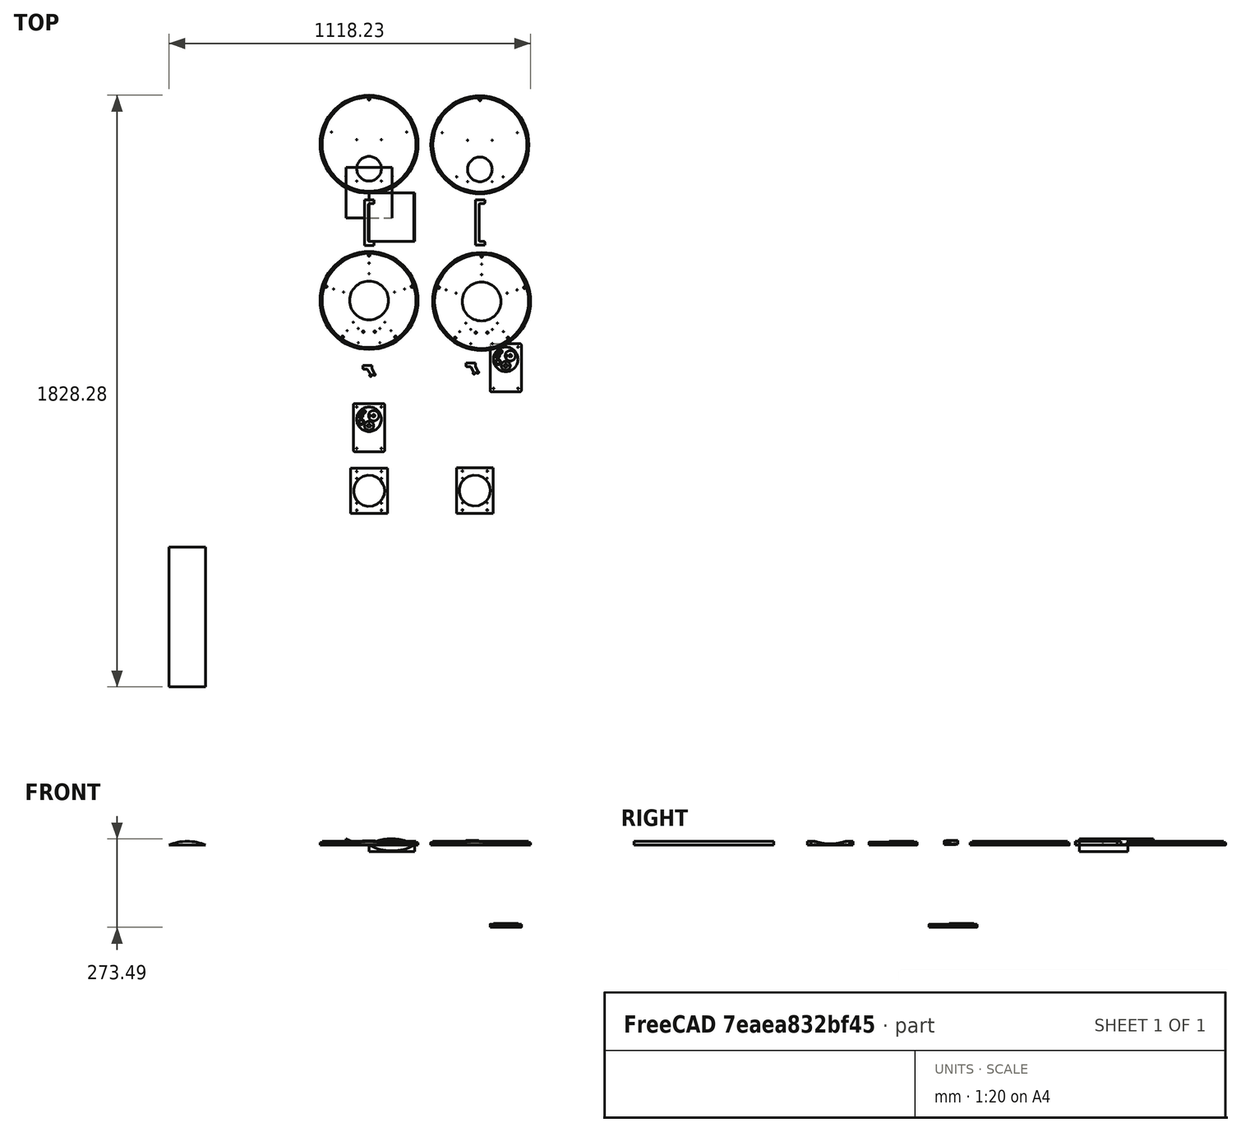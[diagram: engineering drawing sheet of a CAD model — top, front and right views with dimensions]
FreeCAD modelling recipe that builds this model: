
FCSTD DOCUMENT  (FreeCAD 0.19R24291 (Git))
Label: AnywhereAmps_Alpha_A4APR
License: All rights reserved
LicenseURL: http://en.wikipedia.org/wiki/All_rights_reserved
objects: Sketcher::SketchObject×48, Part::Part2DObjectPython×20, PartDesign::Body×18, TechDraw::DrawViewDimension×14, PartDesign::Pad×13, App::Part×8, PartDesign::Pocket×7, Part::FeaturePython×7, TechDraw::DrawProjGroupItem×4, Part::Feature×4, TechDraw::DrawSVGTemplate×2, TechDraw::DrawPage×2, Part::Mirroring×2, PartDesign::FeatureBase×2, Spreadsheet::Sheet×1, TechDraw::DrawViewPart×1, TechDraw::DrawProjGroup×1, TechDraw::DrawViewAnnotation×1, App::LinkGroup×1
note: 141 computed .brp shape members not serialized (recipe doc carries the construction recipe); baked Part::Feature solids carry a one-line shape summary decoded from their .brp
EXTERNAL_REF file=../../../../Zerspanobert/Projekte/Spoilboard/wasteplate_BL_0607.FCStd obj=Spreadsheet

FEATURE [TechDraw::DrawSVGTemplate] Template
  EditableTexts = Designed_by_Name=Designed by Name; Drawing_number=Drawing number; FC-Date=Date; FC-SC=Scale; FC-SH=Sheet; FC-Title=Title; Subtitle=Subtitle; Weight=Weight
  Height = 210
  Orientation = 1
  Width = 297
FEATURE [Sketcher::SketchObject] Sketch  label="master_top_xy"
  FullyConstrained = true
  MapMode = 5
  Support = -> [XY_Plane001]
  expr: Constraints[60] = <<Dimensions>>.predrill_3_rad
  expr: Constraints[37] = <<Dimensions>>.predrill_3_rad
  expr: Constraints[35] = <<Dimensions>>.fastener_dist
  expr: Constraints[50] = <<Dimensions>>.ampcarrier_wid - 2 * <<Dimensions>>.ampcarrier_pre_dist
  expr: Constraints[36] = <<Dimensions>>.fastener_dist
  expr: Constraints[34] = <<Dimensions>>.fastener_dist
  expr: Constraints[49] = <<Dimensions>>.ampcarrier_len - 2 * <<Dimensions>>.ampcarrier_pre_dist
  expr: Constraints[33] = <<Dimensions>>.fastener_dist
  expr: Constraints[55] = <<Dimensions>>.emboss_vdist - <<Dimensions>>.ampcarrier_pre_dist
  expr: Constraints[5] = <<Dimensions>>.shell_thick
  expr: Constraints[11] = <<Dimensions>>.ctrlcutout_rad
  expr: Constraints[64] = <<Dimensions>>.duvel_dist
  expr: Constraints[65] = <<Dimensions>>.duvel_6_rad
  expr: Constraints[1] = Spreadsheet.shell_outer_rad
  expr: Constraints[12] = <<Dimensions>>.ctrlcutout_vdist
  sketch-geometry (24):
    g0: Circle CenterX=0 CenterY=0 CenterZ=0 NormalX=0 NormalY=0 NormalZ=1 AngleXU=0 Radius=151.5
    g1: Circle CenterX=0 CenterY=0 CenterZ=0 NormalX=0 NormalY=0 NormalZ=1 AngleXU=0 Radius=145.3
    g2: LineSegment StartX=-151.5 StartY=0 StartZ=0 EndX=-145.3 EndY=0 EndZ=0
    g3: Circle CenterX=0 CenterY=-75.75 CenterZ=0 NormalX=0 NormalY=0 NormalZ=1 AngleXU=0 Radius=38
    g4: LineSegment StartX=0 StartY=0 StartZ=0 EndX=0 EndY=-75.75 EndZ=0
    g5: LineSegment StartX=0 StartY=0 StartZ=0 EndX=-138.189 EndY=44.9002 EndZ=0
    g6: LineSegment StartX=0 StartY=0 StartZ=0 EndX=0 EndY=145.3 EndZ=0
    g7: LineSegment StartX=0 StartY=0 StartZ=0 EndX=138.189 EndY=44.9002 EndZ=0
    g8: LineSegment StartX=0 StartY=0 StartZ=0 EndX=85.4052 EndY=-117.55 EndZ=0
    g9: LineSegment StartX=0 StartY=0 StartZ=0 EndX=-85.4052 EndY=-117.55 EndZ=0
    g10: Circle CenterX=0 CenterY=139.3 CenterZ=0 NormalX=0 NormalY=0 NormalZ=1 AngleXU=0 Radius=3
    g11: Circle CenterX=116.219 CenterY=37.7619 CenterZ=0 NormalX=0 NormalY=0 NormalZ=1 AngleXU=0 Radius=1
    g12: Circle CenterX=71.8274 CenterY=-98.8619 CenterZ=0 NormalX=0 NormalY=0 NormalZ=1 AngleXU=0 Radius=1
    g13: Circle CenterX=-71.8274 CenterY=-98.8619 CenterZ=0 NormalX=0 NormalY=0 NormalZ=1 AngleXU=0 Radius=1
    g14: Circle CenterX=-116.219 CenterY=37.7619 CenterZ=0 NormalX=0 NormalY=0 NormalZ=1 AngleXU=0 Radius=1
    g15: LineSegment StartX=38 StartY=14.25 StartZ=0 EndX=-38 EndY=14.25 EndZ=0
    g16: LineSegment StartX=-38 StartY=14.25 StartZ=0 EndX=-38 EndY=-113.75 EndZ=0
    g17: LineSegment StartX=-38 StartY=-113.75 StartZ=0 EndX=38 EndY=-113.75 EndZ=0
    g18: LineSegment StartX=38 StartY=-113.75 StartZ=0 EndX=38 EndY=14.25 EndZ=0
    g19: LineSegment StartX=0 StartY=14.25 StartZ=0 EndX=0 EndY=-113.75 EndZ=0
    g20: Circle CenterX=38 CenterY=-113.75 CenterZ=0 NormalX=0 NormalY=0 NormalZ=1 AngleXU=0 Radius=1
    g21: Circle CenterX=-38 CenterY=-113.75 CenterZ=0 NormalX=0 NormalY=0 NormalZ=1 AngleXU=0 Radius=1
    g22: Circle CenterX=-38 CenterY=14.25 CenterZ=0 NormalX=0 NormalY=0 NormalZ=1 AngleXU=0 Radius=1
    g23: Circle CenterX=38 CenterY=14.25 CenterZ=0 NormalX=0 NormalY=0 NormalZ=1 AngleXU=0 Radius=1
  constraints (66):
    c: Coincident(g0,g-1)
    c: Radius(g0) = 151.5
    c: Coincident(g1,g0)
    c: PointOnObject(g2,g0)
    c: PointOnObject(g2,g1)
    c: Distance(g2,g2) = 6.2
    c: PointOnObject(g2,g-1)
    c: Perpendicular(g0,g2)
    c: Coincident(g4,g0)
    c: Vertical(g4)
    c: Coincident(g3,g4)
    c: Radius(g3) = 38
    c: DistanceY(g3,g0) = 75.75
    c: Coincident(g5,g0)
    c: PointOnObject(g5,g1)
    c: Coincident(g6,g0)
    c: PointOnObject(g6,g1)
    c: Coincident(g7,g0)
    c: PointOnObject(g7,g1)
    c: Coincident(g8,g0)
    c: PointOnObject(g8,g1)
    c: Angle(g6,g5) = 1.25664
    c: Angle(g7,g6) = 1.25664
    c: Angle(g8,g7) = 1.25664
    c: PointOnObject(g6,g-2)
    c: Coincident(g9,g0)
    c: PointOnObject(g9,g1)
    c: Angle(g9,g8) = 1.25664
    c: PointOnObject(g10,g6)
    c: PointOnObject(g11,g7)
    c: PointOnObject(g12,g8)
    c: PointOnObject(g13,g9)
    c: PointOnObject(g14,g5)
    c: Distance(g14,g5) = 23.1
    c: Distance(g11,g7) = 23.1
    c: Distance(g12,g8) = 23.1
    c: Distance(g13,g9) = 23.1
    c: Radius(g14) = 1
    c: Equal(g14,g11)
    c: Equal(g14,g12)
    c: Equal(g14,g13)
    c: Coincident(g15,g16)
    c: Coincident(g16,g17)
    c: Coincident(g17,g18)
    c: Coincident(g18,g15)
    c: Horizontal(g15)
    c: Horizontal(g17)
    c: Vertical(g16)
    c: Vertical(g18)
    c: DistanceY(g16,g15) = 128
    c: DistanceX(g15,g15) = 76
    c: PointOnObject(g19,g17)
    c: Vertical(g19)
    c: Symmetric(g15,g15,g19)
    c: PointOnObject(g3,g19)
    c: DistanceY(g19,g3) = 38
    c: Coincident(g20,g17)
    c: Coincident(g21,g16)
    c: Coincident(g22,g15)
    c: Coincident(g23,g15)
    c: Radius(g23) = 1
    c: Equal(g23,g22)
    c: Equal(g23,g21)
    c: Equal(g23,g20)
    c: Distance(g10,g6) = 6
    c: Radius(g10) = 3
FEATURE [Sketcher::SketchObject] Sketch001  label="master_top_xz"
  ExternalGeometry = -> [Sketch]
  FullyConstrained = true
  MapMode = 5
  Placement = pos=(0,0,0) rot=(1,0,0;1.5708rad)
  Support = -> [XZ_Plane001]
  expr: Constraints[32] = <<Dimensions>>.bevel_thick
  expr: Constraints[21] = <<Dimensions>>.bevel_thick
  expr: Constraints[22] = <<Dimensions>>.base_thick
  expr: Constraints[17] = Spreadsheet.shell_outer_rad * 2
  expr: Constraints[19] = <<Dimensions>>.shell_thick
  expr: Constraints[20] = <<Dimensions>>.shell_thick
  sketch-geometry (32):
    g0: LineSegment StartX=-151.5 StartY=0 StartZ=0 EndX=151.5 EndY=0 EndZ=0
    g1: LineSegment StartX=151.5 StartY=0 StartZ=0 EndX=151.5 EndY=8 EndZ=0
    g2: LineSegment StartX=151.5 StartY=8 StartZ=0 EndX=-151.5 EndY=8 EndZ=0
    g3: LineSegment StartX=-151.5 StartY=8 StartZ=0 EndX=-151.5 EndY=0 EndZ=0
    g4: LineSegment StartX=-145.3 StartY=8 StartZ=0 EndX=145.3 EndY=8 EndZ=0
    g5: LineSegment StartX=145.3 StartY=8 StartZ=0 EndX=145.3 EndY=11.8 EndZ=0
    g6: LineSegment StartX=145.3 StartY=11.8 StartZ=0 EndX=-145.3 EndY=11.8 EndZ=0
    g7: LineSegment StartX=-145.3 StartY=11.8 StartZ=0 EndX=-145.3 EndY=8 EndZ=0
    g8: LineSegment StartX=-38 StartY=0 StartZ=0 EndX=-38 EndY=11.8 EndZ=0
    g9: LineSegment StartX=38 StartY=1.69e-14 StartZ=0 EndX=38 EndY=11.8 EndZ=0
    g10: LineSegment StartX=-151.5 StartY=3.8 StartZ=0 EndX=151.5 EndY=3.8 EndZ=0
    g11: LineSegment StartX=-3 StartY=3.8 StartZ=0 EndX=-3 EndY=11.8 EndZ=0
    g12: LineSegment StartX=3 StartY=3.8 StartZ=0 EndX=3 EndY=11.8 EndZ=0
    g13: LineSegment StartX=3 StartY=3.8 StartZ=0 EndX=-3 EndY=3.8 EndZ=0
    g14: LineSegment StartX=-39 StartY=11.8 StartZ=0 EndX=-39 EndY=3.8 EndZ=0
    g15: LineSegment StartX=-39 StartY=3.8 StartZ=0 EndX=-37 EndY=3.8 EndZ=0
    g16: LineSegment StartX=-37 StartY=3.8 StartZ=0 EndX=-37 EndY=11.8 EndZ=0
    g17: LineSegment StartX=37 StartY=11.8 StartZ=0 EndX=37 EndY=3.8 EndZ=0
    g18: LineSegment StartX=37 StartY=3.8 StartZ=0 EndX=39 EndY=3.8 EndZ=0
    g19: LineSegment StartX=39 StartY=3.8 StartZ=0 EndX=39 EndY=11.8 EndZ=0
    g20: LineSegment StartX=-117.219 StartY=11.8 StartZ=0 EndX=-117.219 EndY=3.8 EndZ=0
    g21: LineSegment StartX=-117.219 StartY=3.8 StartZ=0 EndX=-115.219 EndY=3.8 EndZ=0
    g22: LineSegment StartX=-115.219 StartY=3.8 StartZ=0 EndX=-115.219 EndY=11.8 EndZ=0
    g23: LineSegment StartX=-72.8274 StartY=11.8 StartZ=0 EndX=-72.8274 EndY=3.8 EndZ=0
    g24: LineSegment StartX=-70.8274 StartY=11.8 StartZ=0 EndX=-70.8274 EndY=3.8 EndZ=0
    g25: LineSegment StartX=-70.8274 StartY=3.8 StartZ=0 EndX=-72.8274 EndY=3.8 EndZ=0
    g26: LineSegment StartX=70.8274 StartY=11.8 StartZ=0 EndX=70.8274 EndY=3.8 EndZ=0
    g27: LineSegment StartX=72.8274 StartY=11.8 StartZ=0 EndX=72.8274 EndY=3.8 EndZ=0
    g28: LineSegment StartX=72.8274 StartY=3.8 StartZ=0 EndX=70.8274 EndY=3.8 EndZ=0
    g29: LineSegment StartX=115.219 StartY=11.8 StartZ=0 EndX=115.219 EndY=3.8 EndZ=0
    g30: LineSegment StartX=115.219 StartY=3.8 StartZ=0 EndX=117.219 EndY=3.8 EndZ=0
    g31: LineSegment StartX=117.219 StartY=3.8 StartZ=0 EndX=117.219 EndY=11.8 EndZ=0
  constraints (104):
    c: Coincident(g0,g1)
    c: Coincident(g1,g2)
    c: Coincident(g2,g3)
    c: Coincident(g3,g0)
    c: Horizontal(g0)
    c: Horizontal(g2)
    c: Vertical(g1)
    c: Vertical(g3)
    c: Coincident(g4,g5)
    c: Coincident(g5,g6)
    c: Coincident(g6,g7)
    c: Coincident(g7,g4)
    c: Horizontal(g4)
    c: Horizontal(g6)
    c: Vertical(g5)
    c: Vertical(g7)
    c: PointOnObject(g4,g2)
    c: DistanceX(g0,g0) = 303
    c: Symmetric(g0,g0,g-1)
    c: DistanceX(g2,g4) = 6.2
    c: DistanceX(g4,g1) = 6.2
    c: DistanceY(g0,g2) = 8
    c: DistanceY(g0,g6) = 11.8
    c: PointOnObject(g8,g6)
    c: Vertical(g8)
    c: Coincident(g9,g-3)
    c: PointOnObject(g9,g6)
    c: Coincident(g8,g-3)
    c: Vertical(g9)
    c: PointOnObject(g10,g3)
    c: PointOnObject(g10,g1)
    c: Horizontal(g10)
    c: DistanceY(g10,g6) = 8
    c: PointOnObject(g11,g10)
    c: PointOnObject(g11,g6)
    c: Vertical(g11)
    c: PointOnObject(g12,g10)
    c: PointOnObject(g12,g6)
    c: Vertical(g12)
    c: Coincident(g13,g12)
    c: Coincident(g13,g11)
    c: DistanceX(g11,g-4) = 0
    c: DistanceX(g-4,g12) = 0
    c: PointOnObject(g14,g6)
    c: PointOnObject(g14,g10)
    c: Vertical(g14)
    c: PointOnObject(g15,g14)
    c: PointOnObject(g15,g10)
    c: Horizontal(g15)
    c: Coincident(g16,g15)
    c: PointOnObject(g16,g6)
    c: Vertical(g16)
    c: DistanceX(g14,g-5) = 0
    c: DistanceX(g-5,g15) = 0
    c: PointOnObject(g17,g6)
    c: PointOnObject(g17,g10)
    c: Vertical(g17)
    c: Coincident(g18,g17)
    c: Horizontal(g18)
    c: Coincident(g19,g18)
    c: PointOnObject(g19,g6)
    c: Vertical(g19)
    c: DistanceX(g17,g-6) = 0
    c: DistanceX(g-6,g18) = 0
    c: PointOnObject(g20,g6)
    c: PointOnObject(g20,g10)
    c: Vertical(g20)
    c: Coincident(g21,g20)
    c: PointOnObject(g21,g10)
    c: Coincident(g22,g21)
    c: PointOnObject(g22,g6)
    c: Vertical(g22)
    c: DistanceX(g-8,g21) = 0
    c: DistanceX(g20,g-8) = 0
    c: PointOnObject(g23,g6)
    c: PointOnObject(g23,g10)
    c: Vertical(g23)
    c: PointOnObject(g24,g6)
    c: PointOnObject(g24,g10)
    c: Vertical(g24)
    c: Coincident(g25,g24)
    c: Coincident(g25,g23)
    c: DistanceX(g23,g-7) = 0
    c: DistanceX(g-7,g24) = 0
    c: PointOnObject(g26,g6)
    c: PointOnObject(g26,g10)
    c: Vertical(g26)
    c: PointOnObject(g27,g6)
    c: PointOnObject(g27,g10)
    c: Vertical(g27)
    c: Coincident(g28,g27)
    c: Coincident(g28,g26)
    c: DistanceX(g26,g-9) = 0
    c: DistanceX(g27,g-9) = 0
    c: PointOnObject(g29,g6)
    c: PointOnObject(g29,g10)
    c: PointOnObject(g30,g10)
    c: PointOnObject(g31,g6)
    c: Vertical(g31)
    c: Vertical(g29)
    c: Coincident(g29,g30)
    c: DistanceX(g29,g-10) = 0
    c: DistanceX(g-10,g30) = 0
    c: Coincident(g31,g30)
FEATURE [Sketcher::SketchObject] Sketch009  label="master_bottom_xy"
  FullyConstrained = true
  MapMode = 5
  Support = -> [XY_Plane002]
  expr: Constraints[51] = <<Dimensions>>.strut_wid - <<Dimensions>>.base_thick / 2
  expr: .Constraints.shell_thick = <<Dimensions>>.shell_thick
  expr: Constraints[30] = <<Dimensions>>.predrill_3_rad
  expr: Constraints[46] = <<Dimensions>>.duvel_dist
  expr: Constraints[50] = <<Dimensions>>.strut_wid - <<Dimensions>>.base_thick / 2
  expr: Constraints[36] = <<Dimensions>>.strut_wid - <<Dimensions>>.base_thick / 2
  expr: Constraints[34] = <<Dimensions>>.duvel_dist
  expr: Constraints[22] = .Constraints.fastener_angle
  expr: Constraints[70] = <<Dimensions>>.pr_fastener_rad
  expr: Constraints[9] = <<Dimensions>>.pr_cutout_rad
  expr: Constraints[27] = <<Dimensions>>.duvel_dist
  expr: Constraints[68] = <<Dimensions>>.pr_fastener_rad
  expr: Constraints[52] = <<Dimensions>>.strut_wid - <<Dimensions>>.base_thick / 2
  expr: .Constraints.outer_rad = Spreadsheet.shell_outer_rad
  expr: Constraints[23] = .Constraints.fastener_angle
  expr: Constraints[53] = <<Dimensions>>.duvel_dist
  expr: Constraints[71] = <<Dimensions>>.pr_fastener_rad
  expr: Constraints[69] = <<Dimensions>>.pr_fastener_rad
  expr: Constraints[63] = <<Dimensions>>.predrill_3_rad
  expr: Constraints[45] = <<Dimensions>>.duvel_dist
  expr: Constraints[24] = .Constraints.fastener_angle
  expr: Constraints[72] = <<Dimensions>>.pr_fastener_rad
  expr: Constraints[26] = <<Dimensions>>.duvel_6_rad
  expr: Constraints[29] = <<Dimensions>>.strut_wid - <<Dimensions>>.base_thick / 2
  sketch-geometry (25):
    g0: Circle CenterX=0 CenterY=0 CenterZ=0 NormalX=0 NormalY=0 NormalZ=1 AngleXU=0 Radius=151.5
    g1: Circle CenterX=0 CenterY=0 CenterZ=0 NormalX=0 NormalY=0 NormalZ=1 AngleXU=0 Radius=145.3
    g2: LineSegment StartX=-151.5 StartY=0 StartZ=0 EndX=-145.3 EndY=0 EndZ=0
    g3: Circle CenterX=0 CenterY=0 CenterZ=0 NormalX=0 NormalY=0 NormalZ=1 AngleXU=0 Radius=102
    g4: LineSegment StartX=0 StartY=0 StartZ=0 EndX=0 EndY=145.3 EndZ=0
    g5: LineSegment StartX=0 StartY=0 StartZ=0 EndX=138.189 EndY=44.9002 EndZ=0
    g6: LineSegment StartX=0 StartY=0 StartZ=0 EndX=85.4052 EndY=-117.55 EndZ=0
    g7: LineSegment StartX=0 StartY=0 StartZ=0 EndX=-85.4052 EndY=-117.55 EndZ=0
    g8: LineSegment StartX=0 StartY=0 StartZ=0 EndX=-138.189 EndY=44.9002 EndZ=0
    g9: Circle CenterX=0 CenterY=139.3 CenterZ=0 NormalX=0 NormalY=0 NormalZ=1 AngleXU=0 Radius=3
    g10: Circle CenterX=0 CenterY=122.2 CenterZ=0 NormalX=0 NormalY=0 NormalZ=1 AngleXU=0 Radius=1
    g11: Circle CenterX=132.482 CenterY=43.0461 CenterZ=0 NormalX=0 NormalY=0 NormalZ=1 AngleXU=0 Radius=3
    g12: Circle CenterX=116.219 CenterY=37.7619 CenterZ=0 NormalX=0 NormalY=0 NormalZ=1 AngleXU=0 Radius=1
    g13: Circle CenterX=-132.482 CenterY=43.0461 CenterZ=0 NormalX=0 NormalY=0 NormalZ=1 AngleXU=0 Radius=3
    g14: Circle CenterX=-116.219 CenterY=37.7619 CenterZ=0 NormalX=0 NormalY=0 NormalZ=1 AngleXU=0 Radius=1
    g15: Circle CenterX=-81.8785 CenterY=-112.696 CenterZ=0 NormalX=0 NormalY=0 NormalZ=1 AngleXU=0 Radius=3
    g16: Circle CenterX=-71.8274 CenterY=-98.8619 CenterZ=0 NormalX=0 NormalY=0 NormalZ=1 AngleXU=0 Radius=1
    g17: Circle CenterX=81.8785 CenterY=-112.696 CenterZ=0 NormalX=0 NormalY=0 NormalZ=1 AngleXU=0 Radius=3
    g18: Circle CenterX=71.8274 CenterY=-98.8619 CenterZ=0 NormalX=0 NormalY=0 NormalZ=1 AngleXU=0 Radius=1
    g19: LineSegment StartX=0 StartY=0 StartZ=0 EndX=0 EndY=-145.3 EndZ=0
    g20: Circle CenterX=0 CenterY=109 CenterZ=0 NormalX=0 NormalY=0 NormalZ=1 AngleXU=0 Radius=1
    g21: Circle CenterX=103.665 CenterY=33.6829 CenterZ=0 NormalX=0 NormalY=0 NormalZ=1 AngleXU=0 Radius=1
    g22: Circle CenterX=64.0686 CenterY=-88.1829 CenterZ=0 NormalX=0 NormalY=0 NormalZ=1 AngleXU=0 Radius=1
    g23: Circle CenterX=-64.0686 CenterY=-88.1829 CenterZ=0 NormalX=0 NormalY=0 NormalZ=1 AngleXU=0 Radius=1
    g24: Circle CenterX=-103.665 CenterY=33.6829 CenterZ=0 NormalX=0 NormalY=0 NormalZ=1 AngleXU=0 Radius=1
  constraints (70):
    c: Coincident(g0,g-1)
    c: Radius(g0) = 151.5  'outer_rad'
    c: Coincident(g1,g0)
    c: PointOnObject(g2,g0)
    c: PointOnObject(g2,g1)
    c: Distance(g2,g2) = 6.2  'shell_thick'
    c: PointOnObject(g2,g-1)
    c: Perpendicular(g0,g2)
    c: Coincident(g3,g0)
    c: Radius(g3) = 102
    c: Coincident(g4,g0)
    c: PointOnObject(g4,g1)
    c: Vertical(g4)
    c: Coincident(g5,g0)
    c: PointOnObject(g5,g1)
    c: Coincident(g6,g0)
    c: PointOnObject(g6,g1)
    c: Coincident(g7,g0)
    c: PointOnObject(g7,g1)
    c: Coincident(g8,g0)
    c: PointOnObject(g8,g1)
    c: Angle(g5,g4) = 1.25664  'fastener_angle'
    c: Angle(g6,g5) = 1.25664
    c: Angle(g7,g6) = 1.25664
    c: Angle(g8,g7) = 1.25664
    c: PointOnObject(g9,g4)
    c: Radius(g9) = 3
    c: Distance(g9,g4) = 6
    c: PointOnObject(g10,g4)
    c: Distance(g4,g10) = 23.1
    c: Radius(g10) = 1
    c: Equal(g10,g12) = 1.5  'fastener_dia'
    c: Equal(g10,g14) = 1.5  'fastener_dia'
    c: PointOnObject(g17,g6)
    c: Distance(g17,g6) = 6
    c: PointOnObject(g18,g6)
    c: Distance(g18,g6) = 23.1
    c: Equal(g10,g18)
    c: Equal(g9,g13)
    c: Equal(g13,g11)
    c: Equal(g11,g15)
    c: Equal(g15,g17)
    c: PointOnObject(g13,g8)
    c: PointOnObject(g15,g7)
    c: PointOnObject(g11,g5)
    c: Distance(g11,g5) = 6
    c: Distance(g13,g8) = 6
    c: PointOnObject(g14,g8)
    c: PointOnObject(g16,g7)
    c: PointOnObject(g12,g5)
    c: Distance(g14,g8) = 23.1
    c: Distance(g12,g5) = 23.1
    c: Distance(g7,g16) = 23.1
    c: Distance(g15,g7) = 6
    c: Equal(g10,g16)
    c: Coincident(g19,g0)
    c: PointOnObject(g19,g1)
    c: Vertical(g19)
    c: PointOnObject(g20,g4)
    c: PointOnObject(g21,g5)
    c: PointOnObject(g22,g6)
    c: PointOnObject(g23,g7)
    c: PointOnObject(g24,g8)
    c: Radius(g20) = 1
    c: Equal(g20, g21-g24) x4
    c: Distance(g24,g0) = 109
    c: Distance(g20,g0) = 109
    c: Distance(g21,g0) = 109
    c: Distance(g22,g0) = 109
    c: Distance(g0,g23) = 109
FEATURE [Sketcher::SketchObject] Sketch005  label="master_bottom_xz"
  ExternalGeometry = -> [Sketch009]
  FullyConstrained = false
  MapMode = 5
  Placement = pos=(0,0,0) rot=(1,0,0;1.5708rad)
  Support = -> [XZ_Plane002]
  expr: Constraints[203] = <<Dimensions>>.bevel_thick
  expr: Constraints[14] = <<Dimensions>>.base_thick
  expr: Constraints[202] = <<Dimensions>>.bevel_thick
  expr: Constraints[21] = <<Dimensions>>.pr_cutout_rad
  expr: Constraints[13] = <<Dimensions>>.bevel_thick
  expr: Constraints[12] = <<Dimensions>>.shell_thick
  expr: Constraints[195] = <<Dimensions>>.bevel_thick
  expr: Constraints[194] = <<Dimensions>>.bevel_thick
  expr: Constraints[10] = Spreadsheet.shell_outer_rad * 2
  expr: Constraints[196] = <<Dimensions>>.bevel_thick
  sketch-geometry (94):
    g0: LineSegment StartX=-151.5 StartY=0 StartZ=0 EndX=151.5 EndY=0 EndZ=0
    g1: LineSegment StartX=151.5 StartY=0 StartZ=0 EndX=151.5 EndY=8 EndZ=0
    g2: LineSegment StartX=-151.5 StartY=8 StartZ=0 EndX=-151.5 EndY=0 EndZ=0
    g3: LineSegment StartX=145.3 StartY=8 StartZ=0 EndX=145.3 EndY=11.8 EndZ=0
    g4: LineSegment StartX=145.3 StartY=11.8 StartZ=0 EndX=-145.3 EndY=11.8 EndZ=0
    g5: LineSegment StartX=-145.3 StartY=11.8 StartZ=0 EndX=-145.3 EndY=8 EndZ=0
    g6: LineSegment StartX=-102 StartY=11.8 StartZ=0 EndX=102 EndY=11.8 EndZ=0
    g7: LineSegment StartX=102 StartY=11.8 StartZ=0 EndX=102 EndY=0 EndZ=0
    g8: LineSegment StartX=-102 StartY=0 StartZ=0 EndX=-102 EndY=11.8 EndZ=0
    g9: GeomPoint X=0 Y=0 Z=0
    g10: LineSegment StartX=-151.5 StartY=8 StartZ=0 EndX=-145.3 EndY=8 EndZ=0
    g11: LineSegment StartX=145.3 StartY=8 StartZ=0 EndX=151.5 EndY=8 EndZ=0
    g12: GeomPoint X=2.82e-14 Y=11.8 Z=0
    g13: LineSegment StartX=-135.482 StartY=0 StartZ=0 EndX=-129.482 EndY=0 EndZ=0
    g14: LineSegment StartX=-129.482 StartY=0 StartZ=0 EndX=-129.482 EndY=11.8 EndZ=0
    g15: LineSegment StartX=-129.482 StartY=11.8 StartZ=0 EndX=-135.482 EndY=11.8 EndZ=0
    g16: LineSegment StartX=-135.482 StartY=11.8 StartZ=0 EndX=-135.482 EndY=0 EndZ=0
    g17: LineSegment StartX=-110.657 StartY=0 StartZ=0 EndX=-108.657 EndY=0 EndZ=0
    g18: LineSegment StartX=-108.657 StartY=0 StartZ=0 EndX=-108.657 EndY=11.8 EndZ=0
    g19: LineSegment StartX=-108.657 StartY=11.8 StartZ=0 EndX=-110.657 EndY=11.8 EndZ=0
    g20: LineSegment StartX=-110.657 StartY=11.8 StartZ=0 EndX=-110.657 EndY=0 EndZ=0
    g21: LineSegment StartX=-84.8785 StartY=0 StartZ=0 EndX=-78.8785 EndY=0 EndZ=0
    g22: LineSegment StartX=-78.8785 StartY=0 StartZ=0 EndX=-78.8785 EndY=11.8 EndZ=0
    g23: LineSegment StartX=-78.8785 StartY=11.8 StartZ=0 EndX=-84.8785 EndY=11.8 EndZ=0
    g24: LineSegment StartX=-84.8785 StartY=11.8 StartZ=0 EndX=-84.8785 EndY=0 EndZ=0
    g25: LineSegment StartX=-68.7716 StartY=0 StartZ=0 EndX=-66.7716 EndY=0 EndZ=0
    g26: LineSegment StartX=-66.7716 StartY=0 StartZ=0 EndX=-66.7716 EndY=11.8 EndZ=0
    g27: LineSegment StartX=-66.7716 StartY=11.8 StartZ=0 EndX=-68.7716 EndY=11.8 EndZ=0
    g28: LineSegment StartX=-68.7716 StartY=11.8 StartZ=0 EndX=-68.7716 EndY=0 EndZ=0
    g29: LineSegment StartX=-65.0686 StartY=0 StartZ=0 EndX=-63.0686 EndY=0 EndZ=0
    g30: LineSegment StartX=-63.0686 StartY=11.8 StartZ=0 EndX=-65.0686 EndY=11.8 EndZ=0
    g31: LineSegment StartX=-34.5 StartY=0 StartZ=0 EndX=-32.5 EndY=0 EndZ=0
    g32: LineSegment StartX=-32.5 StartY=0 StartZ=0 EndX=-32.5 EndY=11.8 EndZ=0
    g33: LineSegment StartX=-32.5 StartY=11.8 StartZ=0 EndX=-34.5 EndY=11.8 EndZ=0
    g34: LineSegment StartX=-34.5 StartY=11.8 StartZ=0 EndX=-34.5 EndY=0 EndZ=0
    g35: LineSegment StartX=-1 StartY=-1.78e-14 StartZ=0 EndX=1 EndY=-1.82e-14 EndZ=0
    g36: LineSegment StartX=1 StartY=11.8 StartZ=0 EndX=-1 EndY=11.8 EndZ=0
    g37: LineSegment StartX=-1 StartY=-2.66e-14 StartZ=0 EndX=1 EndY=-2.58e-14 EndZ=0
    g38: LineSegment StartX=1 StartY=-2.58e-14 StartZ=0 EndX=1 EndY=11.8 EndZ=0
    g39: LineSegment StartX=1 StartY=11.8 StartZ=0 EndX=-1 EndY=11.8 EndZ=0
    g40: LineSegment StartX=-1 StartY=11.8 StartZ=0 EndX=-1 EndY=-2.66e-14 EndZ=0
    g41: LineSegment StartX=-3 StartY=-3.2e-14 StartZ=0 EndX=3 EndY=-3.1e-14 EndZ=0
    g42: LineSegment StartX=3 StartY=-3.1e-14 StartZ=0 EndX=3 EndY=11.8 EndZ=0
    g43: LineSegment StartX=3 StartY=11.8 StartZ=0 EndX=-3 EndY=11.8 EndZ=0
    g44: LineSegment StartX=-3 StartY=11.8 StartZ=0 EndX=-3 EndY=-3.2e-14 EndZ=0
    g45: LineSegment StartX=15.25 StartY=0 StartZ=0 EndX=20.75 EndY=0 EndZ=0
    g46: LineSegment StartX=20.75 StartY=0 StartZ=0 EndX=20.75 EndY=11.8 EndZ=0
    g47: LineSegment StartX=20.75 StartY=11.8 StartZ=0 EndX=15.25 EndY=11.8 EndZ=0
    g48: LineSegment StartX=15.25 StartY=11.8 StartZ=0 EndX=15.25 EndY=0 EndZ=0
    g49: LineSegment StartX=32.5 StartY=0 StartZ=0 EndX=34.5 EndY=0 EndZ=0
    g50: LineSegment StartX=34.5 StartY=0 StartZ=0 EndX=34.5 EndY=11.8 EndZ=0
    g51: LineSegment StartX=34.5 StartY=11.8 StartZ=0 EndX=32.5 EndY=11.8 EndZ=0
    g52: LineSegment StartX=32.5 StartY=11.8 StartZ=0 EndX=32.5 EndY=0 EndZ=0
    g53: LineSegment StartX=63.0686 StartY=0 StartZ=0 EndX=65.0686 EndY=0 EndZ=0
    g54: LineSegment StartX=65.0686 StartY=11.8 StartZ=0 EndX=63.0686 EndY=11.8 EndZ=0
    g55: LineSegment StartX=66.7716 StartY=0 StartZ=0 EndX=68.7716 EndY=0 EndZ=0
    g56: LineSegment StartX=68.7716 StartY=0 StartZ=0 EndX=68.7716 EndY=11.8 EndZ=0
    g57: LineSegment StartX=68.7716 StartY=11.8 StartZ=0 EndX=66.7716 EndY=11.8 EndZ=0
    g58: LineSegment StartX=66.7716 StartY=11.8 StartZ=0 EndX=66.7716 EndY=0 EndZ=0
    g59: LineSegment StartX=78.8785 StartY=0 StartZ=0 EndX=84.8785 EndY=0 EndZ=0
    g60: LineSegment StartX=84.8785 StartY=0 StartZ=0 EndX=84.8785 EndY=11.8 EndZ=0
    g61: LineSegment StartX=84.8785 StartY=11.8 StartZ=0 EndX=78.8785 EndY=11.8 EndZ=0
    g62: LineSegment StartX=78.8785 StartY=11.8 StartZ=0 EndX=78.8785 EndY=0 EndZ=0
    g63: LineSegment StartX=108.657 StartY=-7.1e-15 StartZ=0 EndX=110.657 EndY=-7.9e-15 EndZ=0
    g64: LineSegment StartX=110.657 StartY=-7.9e-15 StartZ=0 EndX=110.657 EndY=11.8 EndZ=0
    g65: LineSegment StartX=110.657 StartY=11.8 StartZ=0 EndX=108.657 EndY=11.8 EndZ=0
    g66: LineSegment StartX=108.657 StartY=11.8 StartZ=0 EndX=108.657 EndY=-7.1e-15 EndZ=0
    g67: LineSegment StartX=129.482 StartY=0 StartZ=0 EndX=135.482 EndY=0 EndZ=0
    g68: LineSegment StartX=135.482 StartY=0 StartZ=0 EndX=135.482 EndY=11.8 EndZ=0
    g69: LineSegment StartX=135.482 StartY=11.8 StartZ=0 EndX=129.482 EndY=11.8 EndZ=0
    g70: LineSegment StartX=129.482 StartY=11.8 StartZ=0 EndX=129.482 EndY=0 EndZ=0
    g71: LineSegment StartX=-20.75 StartY=2.13e-14 StartZ=0 EndX=-15.25 EndY=2.13e-14 EndZ=0
    g72: LineSegment StartX=-15.25 StartY=2.13e-14 StartZ=0 EndX=-15.25 EndY=11.8 EndZ=0
    g73: LineSegment StartX=-15.25 StartY=11.8 StartZ=0 EndX=-20.75 EndY=11.8 EndZ=0
    g74: LineSegment StartX=-20.75 StartY=11.8 StartZ=0 EndX=-20.75 EndY=2.13e-14 EndZ=0
    g75: LineSegment StartX=-104.665 StartY=-5.3e-15 StartZ=0 EndX=-102.665 EndY=-5.3e-15 EndZ=0
    g76: LineSegment StartX=-102.665 StartY=11.8 StartZ=0 EndX=-104.665 EndY=11.8 EndZ=0
    g77: LineSegment StartX=102.665 StartY=-5.3e-15 StartZ=0 EndX=104.665 EndY=-5.3e-15 EndZ=0
    g78: LineSegment StartX=104.665 StartY=11.8 StartZ=0 EndX=77.9377 EndY=11.8 EndZ=0
    g79: LineSegment StartX=63.0686 StartY=11.8 StartZ=0 EndX=63.0686 EndY=3.8 EndZ=0
    g80: LineSegment StartX=65.0686 StartY=11.8 StartZ=0 EndX=65.0686 EndY=3.8 EndZ=0
    g81: LineSegment StartX=102.665 StartY=11.8 StartZ=0 EndX=102.665 EndY=3.8 EndZ=0
    g82: LineSegment StartX=102.665 StartY=3.8 StartZ=0 EndX=104.665 EndY=3.8 EndZ=0
    g83: LineSegment StartX=104.665 StartY=11.8 StartZ=0 EndX=104.665 EndY=3.8 EndZ=0
    g84: LineSegment StartX=-65.0686 StartY=11.8 StartZ=0 EndX=-65.0686 EndY=3.8 EndZ=0
    g85: LineSegment StartX=-63.0686 StartY=11.8 StartZ=0 EndX=-63.0686 EndY=3.8 EndZ=0
    g86: LineSegment StartX=-102.665 StartY=11.8 StartZ=0 EndX=-102.665 EndY=3.8 EndZ=0
    g87: LineSegment StartX=-104.665 StartY=11.8 StartZ=0 EndX=-104.665 EndY=3.8 EndZ=0
    g88: LineSegment StartX=-104.665 StartY=3.8 StartZ=0 EndX=-102.665 EndY=3.8 EndZ=0
    g89: LineSegment StartX=-1 StartY=11.8 StartZ=0 EndX=-1 EndY=3.8 EndZ=0
    g90: LineSegment StartX=-1 StartY=3.8 StartZ=0 EndX=1 EndY=3.8 EndZ=0
    g91: LineSegment StartX=1 StartY=3.8 StartZ=0 EndX=1 EndY=11.8 EndZ=0
    g92: LineSegment StartX=-65.0686 StartY=3.8 StartZ=0 EndX=-63.0686 EndY=3.8 EndZ=0
    g93: LineSegment StartX=63.0686 StartY=3.8 StartZ=0 EndX=65.0686 EndY=3.8 EndZ=0
  constraints (207):
    c: Coincident(g0,g1)
    c: Coincident(g2,g0)
    c: Horizontal(g0)
    c: Vertical(g1)
    c: Vertical(g2)
    c: Coincident(g3,g4)
    c: Coincident(g4,g5)
    c: Horizontal(g4)
    c: Vertical(g3)
    c: Vertical(g5)
    c: DistanceX(g0,g0) = 303
    c: Symmetric(g0,g0,g-1)
    c: DistanceX(g2,g5) = 6.2
    c: DistanceY(g0,g2) = 8
    c: DistanceY(g0,g4) = 11.8
    c: Coincident(g6,g7)
    c: Coincident(g8,g6)
    c: Horizontal(g6)
    c: Vertical(g7)
    c: Vertical(g8)
    c: Symmetric(g8,g7,g9)
    c: DistanceX(g8,g-1) = 102
    c: PointOnObject(g6,g4)
    c: PointOnObject(g9,g-2)
    c: Coincident(g10,g2)
    c: Coincident(g10,g5)
    c: Horizontal(g10)
    c: Coincident(g11,g3)
    c: Coincident(g11,g1)
    c: Horizontal(g11)
    c: Symmetric(g4,g3,g12)
    c: Equal(g2,g1)
    c: Equal(g11,g10)
    c: Coincident(g13,g14)
    c: Coincident(g14,g15)
    c: Coincident(g15,g16)
    c: Coincident(g16,g13)
    c: Horizontal(g15)
    c: Vertical(g14)
    c: Vertical(g16)
    c: PointOnObject(g14,g4)
    c: Coincident(g17,g18)
    c: Coincident(g18,g19)
    c: Coincident(g19,g20)
    c: Coincident(g20,g17)
    c: Horizontal(g19)
    c: Vertical(g18)
    c: Vertical(g20)
    c: PointOnObject(g18,g4)
    c: Coincident(g21,g22)
    c: Coincident(g22,g23)
    c: Coincident(g23,g24)
    c: Coincident(g24,g21)
    c: Horizontal(g23)
    c: Vertical(g22)
    c: Vertical(g24)
    c: PointOnObject(g22,g4)
    c: Coincident(g25,g26)
    c: Coincident(g26,g27)
    c: Coincident(g27,g28)
    c: Coincident(g28,g25)
    c: Horizontal(g27)
    c: Vertical(g26)
    c: Vertical(g28)
    c: PointOnObject(g26,g4)
    c: Horizontal(g30)
    c: PointOnObject(g30,g4)
    c: Coincident(g31,g32)
    c: Coincident(g32,g33)
    c: Coincident(g33,g34)
    c: Coincident(g34,g31)
    c: Horizontal(g33)
    c: Vertical(g32)
    c: Vertical(g34)
    c: PointOnObject(g32,g4)
    c: Horizontal(g36)
    c: Coincident(g37,g38)
    c: Coincident(g38,g39)
    c: Coincident(g39,g40)
    c: Coincident(g40,g37)
    c: Horizontal(g39)
    c: Vertical(g38)
    c: Vertical(g40)
    c: Coincident(g41,g42)
    c: Coincident(g42,g43)
    c: Coincident(g43,g44)
    c: Coincident(g44,g41)
    c: Horizontal(g43)
    c: Vertical(g42)
    c: Vertical(g44)
    c: PointOnObject(g42,g4)
    c: PointOnObject(g38,g4)
    c: PointOnObject(g36,g4)
    c: Coincident(g45,g46)
    c: Coincident(g46,g47)
    c: Coincident(g47,g48)
    c: Coincident(g48,g45)
    c: Horizontal(g47)
    c: Vertical(g46)
    c: Vertical(g48)
    c: PointOnObject(g46,g4)
    c: Coincident(g49,g50)
    c: Coincident(g50,g51)
    c: Coincident(g51,g52)
    c: Coincident(g52,g49)
    c: Horizontal(g51)
    c: Vertical(g50)
    c: Vertical(g52)
    c: PointOnObject(g50,g4)
    c: Horizontal(g54)
    c: PointOnObject(g54,g4)
    c: Coincident(g55,g56)
    c: Coincident(g56,g57)
    c: Coincident(g57,g58)
    c: Coincident(g58,g55)
    c: Horizontal(g57)
    c: Vertical(g56)
    c: Vertical(g58)
    c: PointOnObject(g56,g4)
    c: Coincident(g59,g60)
    c: Coincident(g60,g61)
    c: Coincident(g61,g62)
    c: Coincident(g62,g59)
    c: Horizontal(g61)
    c: Vertical(g60)
    c: Vertical(g62)
    c: PointOnObject(g60,g4)
    c: Coincident(g63,g64)
    c: Coincident(g64,g65)
    c: Coincident(g65,g66)
    c: Coincident(g66,g63)
    c: Horizontal(g65)
    c: Vertical(g64)
    c: Vertical(g66)
    c: PointOnObject(g64,g4)
    c: Coincident(g67,g68)
    c: Coincident(g68,g69)
    c: Coincident(g69,g70)
    c: Coincident(g70,g67)
    c: Horizontal(g69)
    c: Vertical(g68)
    c: Vertical(g70)
    c: PointOnObject(g68,g4)
    c: Coincident(g71,g72)
    c: Coincident(g72,g73)
    c: Coincident(g73,g74)
    c: Coincident(g74,g71)
    c: Horizontal(g73)
    c: Vertical(g72)
    c: Vertical(g74)
    c: PointOnObject(g72,g4)
    c: Horizontal(g76)
    c: PointOnObject(g76,g4)
    c: Horizontal(g78)
    c: PointOnObject(g78,g4)
    c: Coincident(g79,g54)
    c: Vertical(g79)
    c: Coincident(g80,g54)
    c: Vertical(g80)
    c: DistanceX(g53,g79) = 0
    c: DistanceX(g53,g80) = 0
    c: PointOnObject(g81,g4)
    c: Vertical(g81)
    c: Coincident(g82,g81)
    c: Horizontal(g82)
    c: Coincident(g83,g78)
    c: Coincident(g83,g82)
    c: Vertical(g83)
    c: DistanceX(g77,g81) = 0
    c: DistanceX(g82,g77) = 0
    c: Coincident(g84,g30)
    c: Vertical(g84)
    c: Coincident(g85,g30)
    c: Vertical(g85)
    c: DistanceX(g29,g84) = 0
    c: DistanceX(g29,g85) = 0
    c: Coincident(g86,g76)
    c: Vertical(g86)
    c: Coincident(g87,g76)
    c: Vertical(g87)
    c: Coincident(g88,g87)
    c: Coincident(g88,g86)
    c: Horizontal(g88)
    c: DistanceX(g75,g87) = 0
    c: DistanceX(g75,g86) = 0
    c: Coincident(g89,g36)
    c: Vertical(g89)
    c: Coincident(g90,g89)
    c: Horizontal(g90)
    c: Coincident(g91,g90)
    c: Coincident(g91,g36)
    c: Vertical(g91)
    c: DistanceX(g89,g35) = 0
    c: DistanceX(g90,g35) = 0
    c: DistanceY(g89,g36) = 8
    c: DistanceY(g87,g76) = 8
    c: DistanceY(g81,g78) = 8
    c: PointOnObject(g7,g0)
    c: PointOnObject(g8,g0)
    c: Coincident(g92,g84)
    c: Coincident(g92,g85)
    c: Horizontal(g92)
    c: DistanceY(g84,g30) = 8
    c: DistanceY(g79,g54) = 8
    c: Coincident(g93,g79)
    c: Coincident(g93,g80)
    c: Horizontal(g93)
FEATURE [Sketcher::SketchObject] Sketch011  label="master_bottom_yz"
  ExternalGeometry = -> [Sketch009,Sketch005]
  FullyConstrained = false
  MapMode = 5
  Placement = pos=(0,0,0) rot=(0.57735,0.57735,0.57735;2.0944rad)
  expr: Constraints[137] = <<Dimensions>>.bevel_thick
  expr: Constraints[127] = <<Dimensions>>.bevel_thick
  expr: Constraints[117] = <<Dimensions>>.bevel_thick
  sketch-geometry (66):
    g0: LineSegment StartX=-151.5 StartY=-4.23e-14 StartZ=0 EndX=151.5 EndY=4.23e-14 EndZ=0
    g1: LineSegment StartX=151.5 StartY=4.23e-14 StartZ=0 EndX=151.5 EndY=8 EndZ=0
    g2: LineSegment StartX=151.5 StartY=8 StartZ=0 EndX=145.3 EndY=8 EndZ=0
    g3: LineSegment StartX=145.3 StartY=8 StartZ=0 EndX=145.3 EndY=12 EndZ=0
    g4: LineSegment StartX=-151.5 StartY=-4.23e-14 StartZ=0 EndX=-151.5 EndY=8 EndZ=0
    g5: LineSegment StartX=-151.5 StartY=8 StartZ=0 EndX=-145.3 EndY=8 EndZ=0
    g6: LineSegment StartX=-145.3 StartY=8 StartZ=0 EndX=-145.3 EndY=12 EndZ=0
    g7: LineSegment StartX=-145.3 StartY=12 StartZ=0 EndX=145.3 EndY=12 EndZ=0
    g8: LineSegment StartX=-145.3 StartY=-4.04e-14 StartZ=0 EndX=-145.3 EndY=8 EndZ=0
    g9: LineSegment StartX=145.3 StartY=4.04e-14 StartZ=0 EndX=145.3 EndY=8 EndZ=0
    g10: LineSegment StartX=-145.3 StartY=8 StartZ=0 EndX=145.3 EndY=8 EndZ=0
    g11: LineSegment StartX=-99.1354 StartY=-4.62e-14 StartZ=0 EndX=-93.6354 EndY=-4.62e-14 EndZ=0
    g12: LineSegment StartX=-93.6354 StartY=-4.62e-14 StartZ=0 EndX=-93.6354 EndY=12 EndZ=0
    g13: LineSegment StartX=-93.6354 StartY=12 StartZ=0 EndX=-99.1354 EndY=12 EndZ=0
    g14: LineSegment StartX=-99.1354 StartY=12 StartZ=0 EndX=-99.1354 EndY=-4.62e-14 EndZ=0
    g15: LineSegment StartX=-115.696 StartY=-5.51e-14 StartZ=0 EndX=-109.696 EndY=-5.51e-14 EndZ=0
    g16: LineSegment StartX=-109.696 StartY=-5.51e-14 StartZ=0 EndX=-109.696 EndY=12 EndZ=0
    g17: LineSegment StartX=-109.696 StartY=12 StartZ=0 EndX=-115.696 EndY=12 EndZ=0
    g18: LineSegment StartX=-115.696 StartY=12 StartZ=0 EndX=-115.696 EndY=-5.51e-14 EndZ=0
    g19: LineSegment StartX=32.6829 StartY=-3.2e-14 StartZ=0 EndX=34.6829 EndY=-3.2e-14 EndZ=0
    g20: LineSegment StartX=34.6829 StartY=-3.2e-14 StartZ=0 EndX=34.6829 EndY=12 EndZ=0
    g21: LineSegment StartX=34.6829 StartY=12 StartZ=0 EndX=32.6829 EndY=12 EndZ=0
    g22: LineSegment StartX=32.6829 StartY=12 StartZ=0 EndX=32.6829 EndY=-3.2e-14 EndZ=0
    g23: LineSegment StartX=-94.2797 StartY=-4.44e-14 StartZ=0 EndX=-92.2797 EndY=-4.44e-14 EndZ=0
    g24: LineSegment StartX=-92.2797 StartY=-4.44e-14 StartZ=0 EndX=-92.2797 EndY=12 EndZ=0
    g25: LineSegment StartX=-92.2797 StartY=12 StartZ=0 EndX=-94.2797 EndY=12 EndZ=0
    g26: LineSegment StartX=-94.2797 StartY=12 StartZ=0 EndX=-94.2797 EndY=-4.44e-14 EndZ=0
    g27: LineSegment StartX=-99.1354 StartY=-3.38e-14 StartZ=0 EndX=-93.6354 EndY=-3.38e-14 EndZ=0
    g28: LineSegment StartX=-93.6354 StartY=-3.38e-14 StartZ=0 EndX=-93.6354 EndY=12 EndZ=0
    g29: LineSegment StartX=-93.6354 StartY=12 StartZ=0 EndX=-99.1354 EndY=12 EndZ=0
    g30: LineSegment StartX=-99.1354 StartY=12 StartZ=0 EndX=-99.1354 EndY=-3.38e-14 EndZ=0
    g31: LineSegment StartX=-102 StartY=-2.13e-14 StartZ=0 EndX=102 EndY=-2.13e-14 EndZ=0
    g32: LineSegment StartX=102 StartY=-2.13e-14 StartZ=0 EndX=102 EndY=12 EndZ=0
    g33: LineSegment StartX=102 StartY=12 StartZ=0 EndX=-102 EndY=12 EndZ=0
    g34: LineSegment StartX=-102 StartY=12 StartZ=0 EndX=-102 EndY=-2.13e-14 EndZ=0
    g35: LineSegment StartX=32.6829 StartY=-3.2e-14 StartZ=0 EndX=34.6829 EndY=-3.25e-14 EndZ=0
    g36: LineSegment StartX=34.6829 StartY=12 StartZ=0 EndX=-68.1484 EndY=12 EndZ=0
    g37: LineSegment StartX=-89.1829 StartY=-1.42e-14 StartZ=0 EndX=-87.1829 EndY=-1.42e-14 EndZ=0
    g38: LineSegment StartX=-87.1829 StartY=12 StartZ=0 EndX=-89.1829 EndY=12 EndZ=0
    g39: LineSegment StartX=34.6297 StartY=-2.13e-14 StartZ=0 EndX=36.6297 EndY=-2.13e-14 EndZ=0
    g40: LineSegment StartX=36.6297 StartY=-2.13e-14 StartZ=0 EndX=36.6297 EndY=12 EndZ=0
    g41: LineSegment StartX=36.6297 StartY=12 StartZ=0 EndX=34.6297 EndY=12 EndZ=0
    g42: LineSegment StartX=34.6297 StartY=12 StartZ=0 EndX=34.6297 EndY=-2.13e-14 EndZ=0
    g43: LineSegment StartX=40.0461 StartY=-2.49e-14 StartZ=0 EndX=46.0461 EndY=-2.49e-14 EndZ=0
    g44: LineSegment StartX=46.0461 StartY=-2.49e-14 StartZ=0 EndX=46.0461 EndY=12 EndZ=0
    g45: LineSegment StartX=46.0461 StartY=12 StartZ=0 EndX=40.0461 EndY=12 EndZ=0
    g46: LineSegment StartX=40.0461 StartY=12 StartZ=0 EndX=40.0461 EndY=-2.49e-14 EndZ=0
    g47: LineSegment StartX=-89.1829 StartY=2.31e-14 StartZ=0 EndX=-87.1829 EndY=2.31e-14 EndZ=0
    g48: LineSegment StartX=-87.1829 StartY=12 StartZ=0 EndX=-89.1829 EndY=12 EndZ=0
    g49: LineSegment StartX=114.3 StartY=3.2e-14 StartZ=0 EndX=116.3 EndY=3.2e-14 EndZ=0
    g50: LineSegment StartX=116.3 StartY=3.2e-14 StartZ=0 EndX=116.3 EndY=12 EndZ=0
    g51: LineSegment StartX=116.3 StartY=12 StartZ=0 EndX=114.3 EndY=12 EndZ=0
    g52: LineSegment StartX=114.3 StartY=12 StartZ=0 EndX=114.3 EndY=3.2e-14 EndZ=0
    g53: LineSegment StartX=136.3 StartY=3.73e-14 StartZ=0 EndX=142.3 EndY=3.73e-14 EndZ=0
    g54: LineSegment StartX=142.3 StartY=3.73e-14 StartZ=0 EndX=142.3 EndY=12 EndZ=0
    g55: LineSegment StartX=142.3 StartY=12 StartZ=0 EndX=136.3 EndY=12 EndZ=0
    g56: LineSegment StartX=136.3 StartY=12 StartZ=0 EndX=136.3 EndY=3.73e-14 EndZ=0
    g57: LineSegment StartX=32.6829 StartY=12 StartZ=0 EndX=32.6829 EndY=4 EndZ=0
    g58: LineSegment StartX=34.6829 StartY=12 StartZ=0 EndX=34.6829 EndY=4 EndZ=0
    g59: LineSegment StartX=32.6829 StartY=4 StartZ=0 EndX=34.6829 EndY=4 EndZ=0
    g60: LineSegment StartX=-89.1829 StartY=12 StartZ=0 EndX=-89.1829 EndY=4 EndZ=0
    g61: LineSegment StartX=-87.1829 StartY=12 StartZ=0 EndX=-87.1829 EndY=4 EndZ=0
    g62: LineSegment StartX=-87.1829 StartY=4 StartZ=0 EndX=-89.1829 EndY=4 EndZ=0
    g63: LineSegment StartX=-89.1829 StartY=12 StartZ=0 EndX=-89.1829 EndY=4 EndZ=0
    g64: LineSegment StartX=-87.1829 StartY=12 StartZ=0 EndX=-87.1829 EndY=4 EndZ=0
    g65: LineSegment StartX=-87.1829 StartY=4 StartZ=0 EndX=-89.1829 EndY=4 EndZ=0
  constraints (138):
    c: Vertical(g1)
    c: Coincident(g2,g1)
    c: Horizontal(g2)
    c: Coincident(g3,g2)
    c: Vertical(g3)
    c: Coincident(g4,g0)
    c: Vertical(g4)
    c: Coincident(g5,g4)
    c: Horizontal(g5)
    c: Vertical(g6)
    c: Coincident(g7,g6)
    c: Coincident(g7,g3)
    c: Horizontal(g7)
    c: Vertical(g8)
    c: Coincident(g8,g5)
    c: Coincident(g6,g5)
    c: Vertical(g9)
    c: Coincident(g9,g2)
    c: Horizontal(g10)
    c: Coincident(g2,g10)
    c: Coincident(g5,g10)
    c: Coincident(g0,g1)
    c: Coincident(g11,g12)
    c: Coincident(g12,g13)
    c: Coincident(g13,g14)
    c: Coincident(g14,g11)
    c: Horizontal(g13)
    c: Vertical(g12)
    c: Vertical(g14)
    c: PointOnObject(g12,g7)
    c: Coincident(g15,g16)
    c: Coincident(g16,g17)
    c: Coincident(g17,g18)
    c: Coincident(g18,g15)
    c: Horizontal(g17)
    c: Vertical(g16)
    c: Vertical(g18)
    c: Coincident(g19,g20)
    c: Coincident(g20,g21)
    c: Coincident(g21,g22)
    c: Coincident(g22,g19)
    c: Horizontal(g21)
    c: Vertical(g20)
    c: Vertical(g22)
    c: Coincident(g23,g24)
    c: Coincident(g24,g25)
    c: Coincident(g25,g26)
    c: Coincident(g26,g23)
    c: Horizontal(g25)
    c: Vertical(g24)
    c: Vertical(g26)
    c: PointOnObject(g24,g7)
    c: Coincident(g27,g28)
    c: Coincident(g28,g29)
    c: Coincident(g29,g30)
    c: Coincident(g30,g27)
    c: Horizontal(g29)
    c: Vertical(g28)
    c: Vertical(g30)
    c: PointOnObject(g28,g7)
    c: PointOnObject(g16,g7)
    c: PointOnObject(g20,g7)
    c: Coincident(g31,g32)
    c: Coincident(g32,g33)
    c: Coincident(g33,g34)
    c: Coincident(g34,g31)
    c: Horizontal(g33)
    c: Vertical(g32)
    c: Vertical(g34)
    c: PointOnObject(g32,g7)
    c: Horizontal(g36)
    c: PointOnObject(g36,g7)
    c: Horizontal(g38)
    c: PointOnObject(g38,g7)
    c: Coincident(g39,g40)
    c: Coincident(g40,g41)
    c: Coincident(g41,g42)
    c: Coincident(g42,g39)
    c: Horizontal(g41)
    c: Vertical(g40)
    c: Vertical(g42)
    c: PointOnObject(g40,g7)
    c: Coincident(g43,g44)
    c: Coincident(g44,g45)
    c: Coincident(g45,g46)
    c: Coincident(g46,g43)
    c: Horizontal(g45)
    c: Vertical(g44)
    c: Vertical(g46)
    c: PointOnObject(g44,g7)
    c: Horizontal(g48)
    c: PointOnObject(g48,g7)
    c: Coincident(g49,g50)
    c: Coincident(g50,g51)
    c: Coincident(g51,g52)
    c: Coincident(g52,g49)
    c: Horizontal(g51)
    c: Vertical(g50)
    c: Vertical(g52)
    c: PointOnObject(g50,g7)
    c: Coincident(g53,g54)
    c: Coincident(g54,g55)
    c: Coincident(g55,g56)
    c: Coincident(g56,g53)
    c: Horizontal(g55)
    c: Vertical(g54)
    c: Vertical(g56)
    c: PointOnObject(g54,g7)
    c: PointOnObject(g57,g7)
    c: Vertical(g57)
    c: Coincident(g58,g36)
    c: Vertical(g58)
    c: Coincident(g59,g57)
    c: Coincident(g59,g58)
    c: Horizontal(g59)
    c: DistanceX(g35,g57) = 0
    c: DistanceX(g58,g35) = 0
    c: DistanceY(g57,g36) = 8
    c: Coincident(g60,g38)
    c: Vertical(g60)
    c: Coincident(g61,g38)
    c: Vertical(g61)
    c: Coincident(g62,g61)
    c: Coincident(g62,g60)
    c: Horizontal(g62)
    c: DistanceX(g60,g37) = 0
    c: DistanceX(g61,g37) = 0
    c: DistanceY(g60,g38) = 8
    c: Coincident(g63,g48)
    c: Vertical(g63)
    c: Coincident(g64,g48)
    c: Vertical(g64)
    c: Coincident(g65,g64)
    c: Coincident(g65,g63)
    c: Horizontal(g65)
    c: DistanceX(g63,g47) = 0
    c: DistanceX(g64,g47) = 0
    c: DistanceY(g63,g48) = 8
FEATURE [Spreadsheet::Sheet] Spreadsheet  label="Dimensions"
  cells = A1=Part; B1=Description; C1=Attribute; D1=DimensionName; E1=DimensionValue; A2=any; B2=fastener_3mm_predrill; C2=rad; D2=predrill_3_rad; E2(predrill_3_rad)=1; A3=any; B3=fastener_3mm_drill; C3=rad; D3=drill_3_rad; E3(drill_3_rad)=1.5; A4=any; B4=wood_duvel_drill; C4=rad; D4=duvel_6_rad; E4(duvel_6_rad)=3; A5=bottom; B5=strut_fastener; C5=dist; D5=fastener_dist; E5(fastener_dist)==strut_wid - base_thick / 2; F5=30; A6=bottom; B6=strut_duvel; C6=dist; D6=duvel_dist; E6(duvel_dist)=6; A7=bottom; B7=pr_hole; C7=rad; D7=pr_cutout_rad; E7(pr_cutout_rad)=102; F7=daytonaudio_pm; G7=75; H7=WS200; I7=102; J7=hans_pm; K7=60; A8=bottom; B8=pr_fastener_circle; C8=rad; D8=pr_fastener_rad; E8(pr_fastener_rad)=109; F8=daytonaudio_pm; G8=83; H8=WS200; I8=109; A9=bottom; B9=batcontact; C9=dia; D9=batcontact_dia; E9(batcontact_dia)=5.5; A10=bottom; B10=batholder; C10=length; D10=batholder_len; E10(batholder_len)=70; A11=shell; B11=outer; C11=rad; D11=shell_outer_rad; E11(shell_outer_rad)=151.5; A12=shell; B12=shell; C12=thickness; D12=shell_thick; E12(shell_thick)=6.2; A13=bottom; B13=batholder_fastener; C13=hdist; D13=batholder_fast_hdist; E13(batholder_fast_hdist)=33.5; A14=bottom; B14=batholder_hole; C14=vdist; D14=batholder_fast_vdist; E14(batholder_fast_vdist)=15; A15=bottom; B15=batcontact; C15=vdist; D15=batcontact_vdist; E15(batcontact_vdist)=45; A16=bottom; B16=batcontact; C16=hdist; D16=batcontact_hdist; E16(batcontact_hdist)=18; A17=top; B17=ctrlcutout; C17=vdist; D17=ctrlcutout_vdist; E17(ctrlcutout_vdist)==shell_outer_rad / 2; A18=top; B18=ctrlcutout; C18=rad; D18=ctrlcutout_rad; E18(ctrlcutout_rad)=38; A19=any; B19=base; C19=thickness; D19=base_thick; E19(base_thick)=11.8; A20=top/bottom; B20=bevel; C20=thickness; D20=bevel_thick; E20(bevel_thick)=8; A21=top; B21=drill; C21=depth; D21=drill_depth; E21(drill_depth)=8; A22=bottom; B22=prcutout; C22=depth; D22=prcutout_depth; E22(prcutout_depth)=8; A23=ampcarrier; B23=ampcarrier; C23=length; D23=ampcarrier_len; E23(ampcarrier_len)=148; A24=ampcarrier; B24=ampcarrier; C24=width; D24=ampcarrier_wid; E24(ampcarrier_wid)=96; A25=ampcarrier; B25=emboss; C25=rad; D25=emboss_rad; E25(emboss_rad)==ctrlcutout_rad - 0.05; A26=ampcarrier; B26=emboss; C26=vdist; D26=emboss_vdist; E26(emboss_vdist)=48; A27=ampcarrier; B27=predrill; C27=dist; D27=ampcarrier_pre_dist; E27(ampcarrier_pre_dist)=10; A28=ampcarrier; B28=volume_bevel; C28=rad; D28=volume_bevel_rad; E28(volume_bevel_rad)=16; A29=ampcarrier; B29=volume_hole; C29=rad; D29=volume_hole_rad; E29(volume_hole_rad)=4; A30=ampcarrier; B30=input_bevel; C30=rad; D30=input_bevel_rad; E30(input_bevel_rad)=8.5; A31=ampcarrier; B31=input_hole; C31=rad; D31=input_hole_rad; E31(input_hole_rad)=6; A32=ampcarrier; B32=vout_bevel; C32=rad; D32=vout_bevel_rad; E32(vout_bevel_rad)=6.5; A33=ampcarrier; B33=vout_hole; C33=rad; D33=vout_hole_rad; E33(vout_hole_rad)=4; A34=ampcarrier; B34=auxin_bevel; C34=rad; D34=auxin_bevel_rad; E34(auxin_bevel_rad)=5.5; A35=ampcarrier; B35=auxin_hole; C35=rad; D35=auxin_hole_rad; E35(auxin_hole_rad)=3; A36=ampcarrier; B36=mode_bevel; C36=rad; D36=mode_bevel_rad; E36(mode_bevel_rad)=14; A37=ampcarrier; B37=mode_hole; C37=rad; D37=mode_hole_rad; E37(mode_hole_rad)=5; A38=ampcarrier; B38=controls; C38=dist; D38=controls_dist; +158 more cells
FEATURE [TechDraw::DrawViewPart] View
  CoarseView = false
  Direction = (0,0,1)
  Focus = 100
  HardHidden = false
  IsoCount = 0
  IsoHidden = false
  IsoVisible = false
  LockPosition = false
  Perspective = false
  Rotation = 0
  ScaleType = 0
  SeamHidden = false
  SeamVisible = true
  SmoothHidden = false
  SmoothVisible = true
  Source = -> [Sketch009]
  X = 148.5
  XDirection = (1,0,0)
  Y = 105
FEATURE [TechDraw::DrawPage] Page
  KeepUpdated = true
  NextBalloonIndex = 1
  ProjectionType = 0
  Template = -> Template
  Views = -> [View]
FEATURE [Sketcher::SketchObject] Sketch036  label="master_ampcarrier_xy"
  FullyConstrained = true
  MapMode = 5
  expr: Constraints[114] = <<Dimensions>>.drill_3_rad
  expr: Constraints[112] = <<Dimensions>>.ampcarrier_wid
  expr: Constraints[23] = <<Dimensions>>.ampcarrier_pre_dist
  expr: Constraints[101] = <<Dimensions>>.fillet_rad
  expr: .Constraints.width = <<Dimensions>>.ampcarrier_len
  expr: .Constraints.emboss_dist = <<Dimensions>>.emboss_vdist
  expr: Constraints[111] = <<Dimensions>>.ampcarrier_pre_dist
  expr: Constraints[44] = <<Dimensions>>.vout_hole_rad
  expr: Constraints[47] = <<Dimensions>>.mode_hole_rad
  expr: Constraints[24] = <<Dimensions>>.ampcarrier_pre_dist
  expr: Constraints[43] = <<Dimensions>>.vout_bevel_rad
  expr: Constraints[34] = <<Dimensions>>.volume_bevel_rad
  expr: Constraints[96] = <<Dimensions>>.volume_bevel_rad - 2 * <<Dimensions>>.led_rad
  expr: Constraints[42] = <<Dimensions>>.input_hole_rad
  expr: Constraints[95] = <<Dimensions>>.led_rad
  expr: Constraints[29] = <<Dimensions>>.drill_3_rad
  expr: Constraints[46] = <<Dimensions>>.mode_bevel_rad
  expr: Constraints[39] = <<Dimensions>>.auxin_bevel_rad
  expr: Constraints[110] = <<Dimensions>>.ampcarrier_pre_dist
  expr: Constraints[5] = <<Dimensions>>.emboss_rad
  expr: Constraints[84] = <<Dimensions>>.controls_dist
  expr: Constraints[41] = <<Dimensions>>.input_bevel_rad
  expr: Constraints[40] = <<Dimensions>>.auxin_hole_rad
  expr: .Constraints.InstrumentPot = <<Dimensions>>.volume_hole_rad
  expr: .Constraints.SwitchingPot = <<Dimensions>>.mode_hole_rad
  expr: Constraints[68] = <<Dimensions>>.controls_dist
  sketch-geometry (41):
    g0: LineSegment StartX=-45 StartY=148 StartZ=0 EndX=45 EndY=148 EndZ=0
    g1: LineSegment StartX=48 StartY=145 StartZ=0 EndX=48 EndY=3 EndZ=0
    g2: LineSegment StartX=45 StartY=0 StartZ=0 EndX=-45 EndY=0 EndZ=0
    g3: LineSegment StartX=-48 StartY=3 StartZ=0 EndX=-48 EndY=145 EndZ=0
    g4: Circle CenterX=0 CenterY=100 CenterZ=0 NormalX=0 NormalY=0 NormalZ=1 AngleXU=0 Radius=37.95
    g5: LineSegment StartX=0 StartY=148 StartZ=0 EndX=0 EndY=0 EndZ=0
    g6: LineSegment StartX=-38 StartY=148 StartZ=0 EndX=-38 EndY=0 EndZ=0
    g7: LineSegment StartX=38 StartY=148 StartZ=0 EndX=38 EndY=0 EndZ=0
    g8: LineSegment StartX=-38 StartY=138 StartZ=0 EndX=38 EndY=138 EndZ=0
    g9: LineSegment StartX=-38 StartY=10 StartZ=0 EndX=38 EndY=10 EndZ=0
    g10: Circle CenterX=-38 CenterY=138 CenterZ=0 NormalX=0 NormalY=0 NormalZ=1 AngleXU=0 Radius=1.5
    g11: Circle CenterX=38 CenterY=138 CenterZ=0 NormalX=0 NormalY=0 NormalZ=1 AngleXU=0 Radius=1.5
    g12: Circle CenterX=-38 CenterY=10 CenterZ=0 NormalX=0 NormalY=0 NormalZ=1 AngleXU=0 Radius=1.5
    g13: Circle CenterX=38 CenterY=10 CenterZ=0 NormalX=0 NormalY=0 NormalZ=1 AngleXU=0 Radius=1.5
    g14: Circle CenterX=14.2446 CenterY=110.922 CenterZ=0 NormalX=0 NormalY=0 NormalZ=1 AngleXU=0 Radius=16
    g15: Circle CenterX=14.2446 CenterY=110.922 CenterZ=0 NormalX=0 NormalY=0 NormalZ=1 AngleXU=0 Radius=4
    g16: Circle CenterX=-16.1884 CenterY=123.395 CenterZ=0 NormalX=0 NormalY=0 NormalZ=1 AngleXU=0 Radius=5.5
    g17: Circle CenterX=-16.1884 CenterY=123.395 CenterZ=0 NormalX=0 NormalY=0 NormalZ=1 AngleXU=0 Radius=3
    g18: Circle CenterX=-23.9501 CenterY=91.3921 CenterZ=0 NormalX=0 NormalY=0 NormalZ=1 AngleXU=0 Radius=8.5
    g19: Circle CenterX=-23.9501 CenterY=91.3921 CenterZ=0 NormalX=0 NormalY=0 NormalZ=1 AngleXU=0 Radius=6
    g20: Circle CenterX=-25.4304 CenterY=110.334 CenterZ=0 NormalX=0 NormalY=0 NormalZ=1 AngleXU=0 Radius=6.5
    g21: Circle CenterX=-25.4304 CenterY=110.334 CenterZ=0 NormalX=0 NormalY=0 NormalZ=1 AngleXU=0 Radius=4
    g22: Circle CenterX=0 CenterY=80.05 CenterZ=0 NormalX=0 NormalY=0 NormalZ=1 AngleXU=0 Radius=14
    g23: Circle CenterX=0 CenterY=80.05 CenterZ=0 NormalX=0 NormalY=0 NormalZ=1 AngleXU=0 Radius=5
    g24: LineSegment StartX=-21.5941 StartY=131.207 StartZ=0 EndX=-19.318 EndY=127.918 EndZ=0
    g25: LineSegment StartX=-31.4521 StartY=112.781 StartZ=0 EndX=-35.1578 EndY=114.287 EndZ=0
    g26: LineSegment StartX=26.9417 StartY=120.658 StartZ=0 EndX=30.116 EndY=123.092 EndZ=0
    g27: LineSegment StartX=-31.9491 StartY=88.5172 StartZ=0 EndX=-35.7134 EndY=87.1643 EndZ=0
    g28: LineSegment StartX=0 StartY=66.05 StartZ=0 EndX=0 EndY=62.05 EndZ=0
    g29: LineSegment StartX=-19.3653 StartY=118.906 StartZ=0 EndX=-21.6758 EndY=115.64 EndZ=0
    g30: LineSegment StartX=-24.924 StartY=103.854 StartZ=0 EndX=-24.6123 EndY=99.8663 EndZ=0
    g31: LineSegment StartX=-16.268 StartY=87.7541 StartZ=0 EndX=-12.6529 EndY=86.0421 EndZ=0
    g32: LineSegment StartX=5.86542 StartY=92.7621 StartZ=0 EndX=7.54126 EndY=96.3941 EndZ=0
    g33: Circle CenterX=14.2446 CenterY=110.922 CenterZ=0 NormalX=0 NormalY=0 NormalZ=1 AngleXU=0 Radius=5
    g34: LineSegment StartX=3.04459 StartY=110.922 StartZ=0 EndX=14.2446 EndY=110.922 EndZ=0
    g35: Circle CenterX=3.04459 CenterY=110.922 CenterZ=0 NormalX=0 NormalY=0 NormalZ=1 AngleXU=0 Radius=2.4
    g36: ArcOfCircle CenterX=-45 CenterY=145 CenterZ=0 NormalX=0 NormalY=0 NormalZ=1 AngleXU=0 Radius=3 StartAngle=1.5708 EndAngle=3.14159
    g37: ArcOfCircle CenterX=-45 CenterY=3 CenterZ=0 NormalX=0 NormalY=0 NormalZ=1 AngleXU=0 Radius=3 StartAngle=3.14159 EndAngle=4.71239
    g38: ArcOfCircle CenterX=45 CenterY=3 CenterZ=0 NormalX=0 NormalY=0 NormalZ=1 AngleXU=0 Radius=3 StartAngle=4.71239 EndAngle=6.28319
    g39: ArcOfCircle CenterX=45 CenterY=145 CenterZ=0 NormalX=0 NormalY=0 NormalZ=1 AngleXU=0 Radius=3 StartAngle=4.7e-15 EndAngle=1.5708
    g40: Circle CenterX=0 CenterY=70.55 CenterZ=0 NormalX=0 NormalY=0 NormalZ=1 AngleXU=0 Radius=1.5
  constraints (116):
    c: Horizontal(g0)
    c: Horizontal(g2)
    c: Vertical(g1)
    c: Vertical(g3)
    c: DistanceY(g2,g0) = 148  'width'
    c: Radius(g4) = 37.95
    c: PointOnObject(g5,g2)
    c: Vertical(g5)
    c: Symmetric(g0,g0,g5)
    c: PointOnObject(g4,g5)
    c: DistanceY(g4,g0) = 48  'emboss_dist'
    c: PointOnObject(g6,g0)
    c: Vertical(g6)
    c: PointOnObject(g7,g0)
    c: PointOnObject(g7,g2)
    c: Vertical(g7)
    c: PointOnObject(g8,g6)
    c: PointOnObject(g8,g7)
    c: Horizontal(g8)
    c: PointOnObject(g9,g6)
    c: PointOnObject(g9,g7)
    c: Horizontal(g9)
    c: PointOnObject(g6,g2)
    c: DistanceY(g8,g6) = 10
    c: DistanceY(g6,g9) = 10
    c: Coincident(g10,g8)
    c: Coincident(g11,g8)
    c: Coincident(g12,g9)
    c: Coincident(g13,g9)
    c: Radius(g10) = 1.5
    c: Equal(g10,g11)
    c: Equal(g10,g13)
    c: Equal(g10,g12)
    c: Coincident(g15,g14)
    c: Radius(g14) = 16
    c: Radius(g15) = 4  'InstrumentPot'
    c: Coincident(g17,g16)
    c: Coincident(g19,g18)
    c: Coincident(g21,g20)
    c: Radius(g16) = 5.5
    c: Radius(g17) = 3
    c: Radius(g18) = 8.5
    c: Radius(g19) = 6
    c: Radius(g20) = 6.5
    c: Radius(g21) = 4
    c: Coincident(g23,g22)
    c: Radius(g22) = 14
    c: Radius(g23) = 5
    c: PointOnObject(g24,g4)
    c: Perpendicular(g4,g24)
    c: Perpendicular(g24,g16) = 4.71239
    c: PointOnObject(g26,g14)
    c: PointOnObject(g27,g4)
    c: PointOnObject(g28,g22)
    c: PointOnObject(g28,g4)
    c: PointOnObject(g26,g4)
    c: Perpendicular(g25,g4) = 1.5708
    c: Perpendicular(g25,g20) = 1.5708
    c: Perpendicular(g4,g27)
    c: Perpendicular(g4,g28)
    c: Perpendicular(g27,g18) = 1.5708
    c: Perpendicular(g22,g28)
    c: Perpendicular(g4,g26)
    c: Perpendicular(g14,g26)
    c: Equal(g24,g25)
    c: Equal(g25,g26)
    c: Equal(g26,g27)
    c: Equal(g27,g28)
    c: Distance(g24,g24) = 4
    c: PointOnObject(g29,g16)
    c: PointOnObject(g29,g20)
    c: PointOnObject(g30,g20)
    c: PointOnObject(g30,g18)
    c: Perpendicular(g16,g29)
    c: Perpendicular(g20,g30)
    c: PointOnObject(g31,g18)
    c: PointOnObject(g31,g22)
    c: Perpendicular(g18,g31)
    c: PointOnObject(g32,g22)
    c: PointOnObject(g32,g14)
    c: Perpendicular(g22,g32)
    c: Equal(g29,g30)
    c: Equal(g30,g31)
    c: Equal(g31,g32)
    c: Distance(g29,g29) = 4
    c: Perpendicular(g18,g30)
    c: Perpendicular(g20,g29)
    c: Perpendicular(g22,g31)
    c: Perpendicular(g14,g32)
    c: PointOnObject(g22,g5)
    c: Coincident(g5,g-1)
    c: Coincident(g33,g14)
    c: Radius(g33) = 5  'SwitchingPot'
    c: Coincident(g34,g14)
    c: Horizontal(g34)
    c: Radius(g35) = 2.4
    c: DistanceX(g34,g14) = 11.2
    c: Coincident(g35,g34)
    c: Equal(g39,g36)
    c: Equal(g36,g37)
    c: Equal(g37,g38)
    c: Radius(g38) = 3
    c: Tangent(g38,g2) = 1.5708
    c: Tangent(g38,g1) = 1.5708
    c: Tangent(g37,g2) = 1.5708
    c: Tangent(g37,g3) = 1.5708
    c: Tangent(g36,g3) = 1.5708
    c: Tangent(g36,g0) = 1.5708
    c: Tangent(g39,g1) = 1.5708
    c: Tangent(g39,g0) = 1.5708
    c: DistanceX(g3,g6) = 10
    c: DistanceX(g7,g1) = 10
    c: DistanceX(g3,g1) = 96
    c: PointOnObject(g40,g5)
    c: Radius(g40) = 1.5
    c: DistanceY(g40,g22) = 9.5
FEATURE [Sketcher::SketchObject] Sketch037  label="master_ampcarrier_xz"
  ExternalGeometry = -> [Sketch036]
  FullyConstrained = true
  MapMode = 5
  Placement = pos=(0,0,0) rot=(1,0,0;1.5708rad)
  Support = -> [XZ_Plane003]
  expr: Constraints[9] = <<Dimensions>>.base_thick
  sketch-geometry (4):
    g0: LineSegment StartX=-48 StartY=-1.6e-14 StartZ=0 EndX=48 EndY=-1.42e-14 EndZ=0
    g1: LineSegment StartX=48 StartY=-1.42e-14 StartZ=0 EndX=48 EndY=11.8 EndZ=0
    g2: LineSegment StartX=48 StartY=11.8 StartZ=0 EndX=-48 EndY=11.8 EndZ=0
    g3: LineSegment StartX=-48 StartY=11.8 StartZ=0 EndX=-48 EndY=-1.6e-14 EndZ=0
  constraints (10):
    c: Coincident(g0,g1)
    c: Coincident(g1,g2)
    c: Coincident(g2,g3)
    c: Coincident(g3,g0)
    c: Horizontal(g2)
    c: Vertical(g1)
    c: Vertical(g3)
    c: Coincident(g0,g-4)
    c: Coincident(g0,g-5)
    c: DistanceY(g0,g2) = 11.8
FEATURE [Sketcher::SketchObject] Sketch038  label="master_ampcarrier_yz"
  ExternalGeometry = -> [Sketch036]
  FullyConstrained = true
  MapMode = 5
  Placement = pos=(0,0,0) rot=(0.57735,0.57735,0.57735;2.0944rad)
  Support = -> [YZ_Plane003]
  expr: Constraints[9] = <<Dimensions>>.base_thick
  sketch-geometry (4):
    g0: LineSegment StartX=0 StartY=0 StartZ=0 EndX=148 EndY=0 EndZ=0
    g1: LineSegment StartX=148 StartY=0 StartZ=0 EndX=148 EndY=-11.8 EndZ=0
    g2: LineSegment StartX=148 StartY=-11.8 StartZ=0 EndX=0 EndY=-11.8 EndZ=0
    g3: LineSegment StartX=0 StartY=-11.8 StartZ=0 EndX=0 EndY=0 EndZ=0
  constraints (10):
    c: Coincident(g0,g1)
    c: Coincident(g1,g2)
    c: Coincident(g2,g3)
    c: Coincident(g3,g0)
    c: Horizontal(g2)
    c: Vertical(g1)
    c: Vertical(g3)
    c: Coincident(g0,g-1)
    c: Coincident(g0,g-4)
    c: DistanceY(g2,g0) = 11.8
FEATURE [Sketcher::SketchObject] Sketch039  label="master_top_yz"
  ExternalGeometry = -> [Sketch,Sketch001]
  FullyConstrained = true
  MapMode = 5
  Placement = pos=(0,0,0) rot=(0.57735,0.57735,0.57735;2.0944rad)
  Support = -> [YZ_Plane001]
  expr: Constraints[27] = <<Dimensions>>.bevel_thick
  sketch-geometry (25):
    g0: LineSegment StartX=-151.5 StartY=-4.26e-14 StartZ=0 EndX=151.5 EndY=4.2e-14 EndZ=0
    g1: LineSegment StartX=151.5 StartY=4.2e-14 StartZ=0 EndX=151.5 EndY=8 EndZ=0
    g2: LineSegment StartX=145.3 StartY=8 StartZ=0 EndX=145.3 EndY=11.8 EndZ=0
    g3: LineSegment StartX=145.3 StartY=11.8 StartZ=0 EndX=-145.3 EndY=11.8 EndZ=0
    g4: LineSegment StartX=-145.3 StartY=11.8 StartZ=0 EndX=-145.3 EndY=8 EndZ=0
    g5: LineSegment StartX=-151.5 StartY=8 StartZ=0 EndX=-151.5 EndY=-4.26e-14 EndZ=0
    g6: LineSegment StartX=-151.5 StartY=8 StartZ=0 EndX=151.5 EndY=8 EndZ=0
    g7: LineSegment StartX=-113.75 StartY=-3.17e-14 StartZ=0 EndX=-113.75 EndY=11.8 EndZ=0
    g8: LineSegment StartX=-37.75 StartY=-1.06e-14 StartZ=0 EndX=-37.75 EndY=11.8 EndZ=0
    g9: LineSegment StartX=-151.5 StartY=3.8 StartZ=0 EndX=151.5 EndY=3.8 EndZ=0
    g10: LineSegment StartX=-114.75 StartY=11.8 StartZ=0 EndX=-114.75 EndY=3.8 EndZ=0
    g11: LineSegment StartX=-114.75 StartY=3.8 StartZ=0 EndX=-112.75 EndY=3.8 EndZ=0
    g12: LineSegment StartX=-112.75 StartY=3.8 StartZ=0 EndX=-112.75 EndY=11.8 EndZ=0
    g13: LineSegment StartX=-99.8619 StartY=11.8 StartZ=0 EndX=-99.8619 EndY=3.8 EndZ=0
    g14: LineSegment StartX=-99.8619 StartY=3.8 StartZ=0 EndX=-97.8619 EndY=3.8 EndZ=0
    g15: LineSegment StartX=-97.8619 StartY=3.8 StartZ=0 EndX=-97.8619 EndY=11.8 EndZ=0
    g16: LineSegment StartX=36.7619 StartY=11.8 StartZ=0 EndX=36.7619 EndY=3.8 EndZ=0
    g17: LineSegment StartX=36.7619 StartY=3.8 StartZ=0 EndX=38.7619 EndY=3.8 EndZ=0
    g18: LineSegment StartX=38.7619 StartY=3.8 StartZ=0 EndX=38.7619 EndY=11.8 EndZ=0
    g19: LineSegment StartX=136.3 StartY=3.8 StartZ=0 EndX=136.3 EndY=11.8 EndZ=0
    g20: LineSegment StartX=136.3 StartY=3.8 StartZ=0 EndX=142.3 EndY=3.8 EndZ=0
    g21: LineSegment StartX=142.3 StartY=3.8 StartZ=0 EndX=142.3 EndY=11.8 EndZ=0
    g22: LineSegment StartX=13.25 StartY=11.8 StartZ=0 EndX=13.25 EndY=3.8 EndZ=0
    g23: LineSegment StartX=13.25 StartY=3.8 StartZ=0 EndX=15.25 EndY=3.8 EndZ=0
    g24: LineSegment StartX=15.25 StartY=3.8 StartZ=0 EndX=15.25 EndY=11.8 EndZ=0
  constraints (80):
    c: Coincident(g0,g-3)
    c: Coincident(g0,g-3)
    c: Coincident(g1,g0)
    c: Coincident(g3,g2)
    c: Horizontal(g3)
    c: Coincident(g4,g3)
    c: Vertical(g4)
    c: Coincident(g5,g0)
    c: Vertical(g5)
    c: Coincident(g6,g5)
    c: Coincident(g6,g1)
    c: Horizontal(g6)
    c: PointOnObject(g2,g6)
    c: Vertical(g2)
    c: Vertical(g1)
    c: PointOnObject(g4,g6)
    c: DistanceX(g-4,g4) = 0
    c: DistanceX(g2,g-4) = 0
    c: Coincident(g7,g-5)
    c: PointOnObject(g7,g3)
    c: Vertical(g7)
    c: Coincident(g8,g-5)
    c: PointOnObject(g8,g3)
    c: Vertical(g8)
    c: PointOnObject(g9,g5)
    c: PointOnObject(g9,g1)
    c: Horizontal(g9)
    c: DistanceY(g9,g3) = 8
    c: PointOnObject(g10,g3)
    c: PointOnObject(g10,g9)
    c: Vertical(g10)
    c: PointOnObject(g11,g9)
    c: PointOnObject(g12,g3)
    c: Vertical(g12)
    c: PointOnObject(g13,g3)
    c: PointOnObject(g13,g9)
    c: Vertical(g13)
    c: PointOnObject(g14,g9)
    c: Coincident(g15,g14)
    c: PointOnObject(g15,g3)
    c: Vertical(g15)
    c: PointOnObject(g16,g3)
    c: PointOnObject(g16,g9)
    c: Vertical(g16)
    c: Coincident(g17,g16)
    c: PointOnObject(g17,g9)
    c: PointOnObject(g18,g3)
    c: PointOnObject(g19,g9)
    c: PointOnObject(g19,g3)
    c: Vertical(g19)
    c: Coincident(g20,g19)
    c: PointOnObject(g20,g9)
    c: Coincident(g21,g20)
    c: PointOnObject(g21,g3)
    c: Vertical(g21)
    c: DistanceX(g20,g-9) = 0
    c: DistanceX(g19,g-9) = 0
    c: Vertical(g18)
    c: DistanceX(g16,g-8) = 0
    c: DistanceX(g17,g-8) = 0
    c: Coincident(g18,g17)
    c: DistanceX(g13,g-7) = 0
    c: DistanceX(g14,g-7) = 0
    c: Coincident(g14,g13)
    c: DistanceX(g10,g-6) = 0
    c: DistanceX(g11,g-6) = 0
    c: Coincident(g11,g10)
    c: Coincident(g12,g11)
    c: PointOnObject(g22,g3)
    c: PointOnObject(g22,g9)
    c: Vertical(g22)
    c: Coincident(g23,g22)
    c: PointOnObject(g23,g9)
    c: Coincident(g24,g23)
    c: PointOnObject(g24,g3)
    c: Vertical(g24)
    c: DistanceX(g-10,g22) = 0
    c: DistanceX(g-10,g23) = 0
    c: PointOnObject(g-12,g3)
    c: PointOnObject(g-11,g6)
FEATURE [Sketcher::SketchObject] Sketch041
  ExternalGeometry = -> [Sketch037,Sketch036]
  FullyConstrained = true
  MapMode = 5
  Support = -> [XY_Plane003]
  expr: Constraints[7] = <<Dimensions>>.fillet_rad
  sketch-geometry (8):
    g0: LineSegment StartX=-48 StartY=145 StartZ=0 EndX=-48 EndY=3 EndZ=0
    g1: LineSegment StartX=-45 StartY=148 StartZ=0 EndX=45 EndY=148 EndZ=0
    g2: LineSegment StartX=-45 StartY=0 StartZ=0 EndX=45 EndY=0 EndZ=0
    g3: LineSegment StartX=48 StartY=145 StartZ=0 EndX=48 EndY=3 EndZ=0
    g4: ArcOfCircle CenterX=-45 CenterY=3 CenterZ=0 NormalX=0 NormalY=0 NormalZ=1 AngleXU=0 Radius=3 StartAngle=3.14159 EndAngle=4.71239
    g5: ArcOfCircle CenterX=45 CenterY=3 CenterZ=0 NormalX=0 NormalY=0 NormalZ=1 AngleXU=0 Radius=3 StartAngle=4.71239 EndAngle=6.28319
    g6: ArcOfCircle CenterX=45 CenterY=145 CenterZ=0 NormalX=0 NormalY=0 NormalZ=1 AngleXU=0 Radius=3 StartAngle=-4.4e-15 EndAngle=1.5708
    g7: ArcOfCircle CenterX=-45 CenterY=145 CenterZ=0 NormalX=0 NormalY=0 NormalZ=1 AngleXU=0 Radius=3 StartAngle=1.5708 EndAngle=3.14159
  constraints (18):
    c: Vertical(g0)
    c: Horizontal(g1)
    c: Vertical(g3)
    c: Horizontal(g2)
    c: Equal(g7,g6)
    c: Equal(g6,g5)
    c: Equal(g5,g4)
    c: Radius(g7) = 3
    c: Tangent(g7,g1) = 1.5708
    c: Tangent(g7,g0) = -1.5708
    c: Tangent(g6,g1) = 1.5708
    c: Tangent(g6,g3) = 1.5708
    c: Tangent(g4,g0) = -1.5708
    c: Tangent(g4,g2) = -1.5708
    c: Tangent(g5,g3) = 1.5708
    c: Tangent(g5,g2) = -1.5708
    c: Coincident(g7,g-4)
    c: Coincident(g5,g-5)
FEATURE [PartDesign::Pad] Pad004  label="ampc_plate"
  Direction = (1,1,1)
  Length = 9.8
  Length2 = 100
  Profile = -> Sketch041
  Type = 0
  expr: Length = <<Dimensions>>.base_thick - <<Dimensions>>.emboss_depth
FEATURE [Sketcher::SketchObject] Sketch045  label="b_plate"
  ExternalGeometry = -> [Sketch009]
  FullyConstrained = true
  MapMode = 5
  Support = -> [XY_Plane002]
  sketch-geometry (1):
    g0: Circle CenterX=0 CenterY=0 CenterZ=0 NormalX=0 NormalY=0 NormalZ=1 AngleXU=0 Radius=151.5
  constraints (2):
    c: Coincident(g0,g-1)
    c: Tangent(g0,g-3)
FEATURE [PartDesign::Pad] Pad006  label="bottom_plate"
  Direction = (1,1,1)
  Length = 8
  Length2 = 100
  Profile = -> Sketch045
  Type = 0
  expr: Length = <<Dimensions>>.bevel_thick
FEATURE [Sketcher::SketchObject] Sketch046
  ExternalGeometry = -> [Sketch009]
  FullyConstrained = true
  MapMode = 5
  Placement = pos=(0,0,8) rot=(0,0,1;0rad)
  Support = -> [Pad006]
  sketch-geometry (1):
    g0: Circle CenterX=0 CenterY=0 CenterZ=0 NormalX=0 NormalY=0 NormalZ=1 AngleXU=0 Radius=145.3
  constraints (2):
    c: Coincident(g0,g-1)
    c: Tangent(g0,g-3)
FEATURE [PartDesign::Pad] Pad007  label="bottom_bevel"
  BaseFeature = -> Pad006
  Direction = (1,1,1)
  Length = 3.8
  Length2 = 100
  Profile = -> Sketch046
  Type = 0
  expr: Length = <<Dimensions>>.base_thick - <<Dimensions>>.bevel_thick
FEATURE [Sketcher::SketchObject] Sketch047
  ExternalGeometry = -> [Sketch009]
  FullyConstrained = false
  MapMode = 5
  Placement = pos=(0,0,11.8) rot=(0,0,1;0rad)
  Support = -> [Pad007]
  sketch-geometry (17):
    g0: Circle CenterX=0 CenterY=139.3 CenterZ=0 NormalX=0 NormalY=0 NormalZ=1 AngleXU=0 Radius=3
    g1: Circle CenterX=0 CenterY=115.3 CenterZ=0 NormalX=0 NormalY=0 NormalZ=1 AngleXU=0 Radius=1
    g2: Circle CenterX=-132.482 CenterY=43.0461 CenterZ=0 NormalX=0 NormalY=0 NormalZ=1 AngleXU=0 Radius=3
    g3: Circle CenterX=-109.657 CenterY=35.6297 CenterZ=0 NormalX=0 NormalY=0 NormalZ=1 AngleXU=0 Radius=1
    g4: Circle CenterX=-81.8785 CenterY=-112.696 CenterZ=0 NormalX=0 NormalY=0 NormalZ=1 AngleXU=0 Radius=3
    g5: Circle CenterX=-67.7716 CenterY=-93.2797 CenterZ=0 NormalX=0 NormalY=0 NormalZ=1 AngleXU=0 Radius=1
    g6: Circle CenterX=18 CenterY=-96.3854 CenterZ=0 NormalX=0 NormalY=0 NormalZ=1 AngleXU=0 Radius=2.75
    g7: Circle CenterX=-64.0686 CenterY=-88.1829 CenterZ=0 NormalX=0 NormalY=0 NormalZ=1 AngleXU=0 Radius=1
    g8: Circle CenterX=0 CenterY=109 CenterZ=0 NormalX=0 NormalY=0 NormalZ=1 AngleXU=0 Radius=1
    g9: Circle CenterX=-103.665 CenterY=33.6829 CenterZ=0 NormalX=0 NormalY=0 NormalZ=1 AngleXU=0 Radius=1
    g10: Circle CenterX=103.665 CenterY=33.6829 CenterZ=0 NormalX=0 NormalY=0 NormalZ=1 AngleXU=0 Radius=1
    g11: Circle CenterX=64.0686 CenterY=-88.1829 CenterZ=0 NormalX=0 NormalY=0 NormalZ=1 AngleXU=0 Radius=1
    g12: Circle CenterX=67.7716 CenterY=-93.2797 CenterZ=0 NormalX=0 NormalY=0 NormalZ=1 AngleXU=0 Radius=1
    g13: Circle CenterX=81.8785 CenterY=-112.696 CenterZ=0 NormalX=0 NormalY=0 NormalZ=1 AngleXU=0 Radius=3
    g14: Circle CenterX=109.657 CenterY=35.6297 CenterZ=0 NormalX=0 NormalY=0 NormalZ=1 AngleXU=0 Radius=1
    g15: Circle CenterX=132.482 CenterY=43.0461 CenterZ=0 NormalX=0 NormalY=0 NormalZ=1 AngleXU=0 Radius=3
    g16: Circle CenterX=0 CenterY=0 CenterZ=0 NormalX=0 NormalY=0 NormalZ=1 AngleXU=0 Radius=102
  constraints (1):
    c: Coincident(g16,g-1)
FEATURE [PartDesign::Pocket] Pocket003  label="bottom_holes"
  BaseFeature = -> Pad007
  Length = 5
  Length2 = 100
  Profile = -> Sketch047
  Type = 1
FEATURE [Sketcher::SketchObject] Sketch048
  FullyConstrained = false
  MapMode = 5
  Placement = pos=(0,0,11.8) rot=(0,0,1;0rad)
  Support = -> [Pad007]
  sketch-geometry (5):
    g0: Circle CenterX=0 CenterY=109 CenterZ=0 NormalX=0 NormalY=0 NormalZ=1 AngleXU=0 Radius=1
    g1: Circle CenterX=-103.665 CenterY=33.6829 CenterZ=0 NormalX=0 NormalY=0 NormalZ=1 AngleXU=0 Radius=1
    g2: Circle CenterX=-64.0686 CenterY=-88.1829 CenterZ=0 NormalX=0 NormalY=0 NormalZ=1 AngleXU=0 Radius=1
    g3: Circle CenterX=64.0686 CenterY=-88.1829 CenterZ=0 NormalX=0 NormalY=0 NormalZ=1 AngleXU=0 Radius=1
    g4: Circle CenterX=103.665 CenterY=33.6829 CenterZ=0 NormalX=0 NormalY=0 NormalZ=1 AngleXU=0 Radius=1
FEATURE [PartDesign::Pocket] Pocket004  label="bottom_pockets"
  BaseFeature = -> Pocket003
  Length = 8
  Length2 = 100
  Profile = -> Sketch048
  Type = 0
  expr: Length = <<Dimensions>>.bevel_thick
FEATURE [Sketcher::SketchObject] Sketch049
  ExternalGeometry = -> [Sketch]
  FullyConstrained = true
  MapMode = 5
  Support = -> [XY_Plane001]
  sketch-geometry (1):
    g0: Circle CenterX=0 CenterY=0 CenterZ=0 NormalX=0 NormalY=0 NormalZ=1 AngleXU=0 Radius=151.5
  constraints (2):
    c: Coincident(g0,g-1)
    c: Equal(g-3,g0)
FEATURE [PartDesign::Pad] Pad  label="top_plate"
  Direction = (1,1,1)
  Length = 8
  Length2 = 100
  Profile = -> Sketch049
  Type = 0
  expr: Length = <<Dimensions>>.bevel_thick
FEATURE [Sketcher::SketchObject] Sketch050
  ExternalGeometry = -> [Sketch]
  FullyConstrained = true
  MapMode = 5
  Placement = pos=(0,0,8) rot=(0,0,1;0rad)
  Support = -> [Pad]
  sketch-geometry (1):
    g0: Circle CenterX=0 CenterY=0 CenterZ=0 NormalX=0 NormalY=0 NormalZ=1 AngleXU=0 Radius=145.3
  constraints (2):
    c: Coincident(g0,g-1)
    c: Equal(g0,g-3)
FEATURE [PartDesign::Pad] Pad008  label="top_bevel"
  BaseFeature = -> Pad
  Direction = (1,1,1)
  Length = 3.8
  Length2 = 100
  Profile = -> Sketch050
  Type = 0
  expr: Length = <<Dimensions>>.base_thick - <<Dimensions>>.bevel_thick
FEATURE [Sketcher::SketchObject] Sketch051
  ExternalGeometry = -> [Sketch]
  FullyConstrained = true
  MapMode = 5
  Placement = pos=(0,0,11.8) rot=(0,0,1;0rad)
  Support = -> [Pad008]
  sketch-geometry (9):
    g0: Circle CenterX=-38 CenterY=-113.75 CenterZ=0 NormalX=0 NormalY=0 NormalZ=1 AngleXU=0 Radius=1
    g1: Circle CenterX=-71.8274 CenterY=-98.8619 CenterZ=0 NormalX=0 NormalY=0 NormalZ=1 AngleXU=0 Radius=1
    g2: Circle CenterX=38 CenterY=-113.75 CenterZ=0 NormalX=0 NormalY=0 NormalZ=1 AngleXU=0 Radius=1
    g3: Circle CenterX=71.8274 CenterY=-98.8619 CenterZ=0 NormalX=0 NormalY=0 NormalZ=1 AngleXU=0 Radius=1
    g4: Circle CenterX=38 CenterY=14.25 CenterZ=0 NormalX=0 NormalY=0 NormalZ=1 AngleXU=0 Radius=1
    g5: Circle CenterX=-38 CenterY=14.25 CenterZ=0 NormalX=0 NormalY=0 NormalZ=1 AngleXU=0 Radius=1
    g6: Circle CenterX=-116.219 CenterY=37.7619 CenterZ=0 NormalX=0 NormalY=0 NormalZ=1 AngleXU=0 Radius=1
    g7: Circle CenterX=116.219 CenterY=37.7619 CenterZ=0 NormalX=0 NormalY=0 NormalZ=1 AngleXU=0 Radius=1
    g8: Circle CenterX=0 CenterY=139.3 CenterZ=0 NormalX=0 NormalY=0 NormalZ=1 AngleXU=0 Radius=3
  constraints (18):
    c: Coincident(g0,g-9)
    c: Coincident(g1,g-8)
    c: Coincident(g2,g-10)
    c: Coincident(g3,g-11)
    c: Coincident(g4,g-5)
    c: Coincident(g5,g-6)
    c: Coincident(g6,g-7)
    c: Coincident(g7,g-4)
    c: Coincident(g8,g-3)
    c: Equal(g6,g-7)
    c: Equal(g-3,g8)
    c: Equal(g-6,g5)
    c: Equal(g-5,g4)
    c: Equal(g-4,g7)
    c: Equal(g-8,g1)
    c: Equal(g0,g-9)
    c: Equal(g2,g-10)
    c: Equal(g-11,g3)
FEATURE [PartDesign::Pocket] Pocket  label="top_pockets"
  BaseFeature = -> Pad008
  Length = 8
  Length2 = 100
  Profile = -> Sketch051
  Type = 0
  expr: Length = <<Dimensions>>.bevel_thick
FEATURE [Sketcher::SketchObject] Sketch052
  ExternalGeometry = -> [Sketch]
  FullyConstrained = true
  MapMode = 5
  Placement = pos=(0,0,11.8) rot=(0,0,1;0rad)
  Support = -> [Pad008]
  sketch-geometry (1):
    g0: Circle CenterX=0 CenterY=-75.75 CenterZ=0 NormalX=0 NormalY=0 NormalZ=1 AngleXU=0 Radius=38
  constraints (2):
    c: Coincident(g0,g-3)
    c: Equal(g0,g-3)
FEATURE [PartDesign::Pocket] Pocket005  label="top_holes"
  BaseFeature = -> Pocket
  Length = 5
  Length2 = 100
  Profile = -> Sketch052
  Type = 1
FEATURE [Part::FeaturePython] Clone001  label="part_top"  # Draft clone (typed FeaturePython)
  AttacherType = Attacher::AttachEngine3D
  Fuse = false
  Objects = -> [Pocket005]
  Placement = pos=(342.547,148.129,0) rot=(0,0,1;0rad)
  Scale = (1,1,1)
FEATURE [Part::FeaturePython] Clone002  label="part_bottom"  # Draft clone (typed FeaturePython)
  AttacherType = Attacher::AttachEngine3D
  Fuse = false
  Objects = -> [Pocket004]
  Placement = pos=(347.838,-335.934,0) rot=(0,0,1;0rad)
  Scale = (1,1,1)
FEATURE [Sketcher::SketchObject] Sketch053  label="master_sc_xy"
  FullyConstrained = true
  MapMode = 5
  Support = -> [XY_Plane004]
  expr: Constraints[79] = <<Dimensions>>.sc_pz_grl_wid
  expr: Constraints[59] = <<Dimensions>>.predrill_3_rad
  expr: Constraints[42] = <<Dimensions>>.sc_mounting_rad
  expr: Constraints[20] = <<Dimensions>>.sc_cutout_rad
  expr: Constraints[10] = <<Dimensions>>.sc_wid
  expr: Constraints[37] = <<Dimensions>>.drill_3_rad
  expr: Constraints[9] = <<Dimensions>>.sc_len
  expr: Constraints[65] = <<Dimensions>>.ampcarrier_pre_dist
  expr: Constraints[81] = <<Dimensions>>.predrill_3_rad + <<Dimensions>>.sc_pz_grl_wid
  expr: Constraints[66] = <<Dimensions>>.ampcarrier_pre_dist
  sketch-geometry (43):
    g0: LineSegment StartX=57 StartY=0 StartZ=0 EndX=-57 EndY=0 EndZ=0
    g1: LineSegment StartX=-57 StartY=0 StartZ=0 EndX=-57 EndY=140.4 EndZ=0
    g2: LineSegment StartX=-57 StartY=140.4 StartZ=0 EndX=57 EndY=140.4 EndZ=0
    g3: LineSegment StartX=57 StartY=140.4 StartZ=0 EndX=57 EndY=0 EndZ=0
    g4: LineSegment StartX=2.9e-15 StartY=140.4 StartZ=0 EndX=2.9e-15 EndY=0 EndZ=0
    g5: LineSegment StartX=-57 StartY=70.2 StartZ=0 EndX=57 EndY=70.2 EndZ=0
    g6: GeomPoint X=2.9e-15 Y=70.2 Z=0
    g7: Circle CenterX=2.9e-15 CenterY=70.2 CenterZ=0 NormalX=0 NormalY=0 NormalZ=1 AngleXU=0 Radius=48
    g8: LineSegment StartX=-38.1838 StartY=140.4 StartZ=0 EndX=-38.1838 EndY=0 EndZ=0
    g9: LineSegment StartX=38.1838 StartY=140.4 StartZ=0 EndX=38.1838 EndY=0 EndZ=0
    g10: LineSegment StartX=38.1838 StartY=130.4 StartZ=0 EndX=-38.1838 EndY=130.4 EndZ=0
    g11: LineSegment StartX=-38.1838 StartY=10 StartZ=0 EndX=38.1838 EndY=10 EndZ=0
    g12: Circle CenterX=-38.1838 CenterY=130.4 CenterZ=0 NormalX=0 NormalY=0 NormalZ=1 AngleXU=0 Radius=1.5
    g13: Circle CenterX=38.1838 CenterY=130.4 CenterZ=0 NormalX=0 NormalY=0 NormalZ=1 AngleXU=0 Radius=1.5
    g14: Circle CenterX=-38.1838 CenterY=10 CenterZ=0 NormalX=0 NormalY=0 NormalZ=1 AngleXU=0 Radius=1.5
    g15: Circle CenterX=38.1838 CenterY=10 CenterZ=0 NormalX=0 NormalY=0 NormalZ=1 AngleXU=0 Radius=1.5
    g16: Circle CenterX=2.9e-15 CenterY=70.2 CenterZ=0 NormalX=0 NormalY=0 NormalZ=1 AngleXU=0 Radius=54
    g17: LineSegment StartX=-38.1838 StartY=108.384 StartZ=0 EndX=38.1838 EndY=108.384 EndZ=0
    g18: LineSegment StartX=38.1838 StartY=108.384 StartZ=0 EndX=38.1838 EndY=32.0162 EndZ=0
    g19: LineSegment StartX=38.1838 StartY=32.0162 StartZ=0 EndX=-38.1838 EndY=32.0162 EndZ=0
    g20: LineSegment StartX=-38.1838 StartY=32.0162 StartZ=0 EndX=-38.1838 EndY=108.384 EndZ=0
    g21: Circle CenterX=-38.1838 CenterY=108.384 CenterZ=0 NormalX=0 NormalY=0 NormalZ=1 AngleXU=0 Radius=1
    g22: Circle CenterX=38.1838 CenterY=108.384 CenterZ=0 NormalX=0 NormalY=0 NormalZ=1 AngleXU=0 Radius=1
    g23: Circle CenterX=38.1838 CenterY=32.0162 CenterZ=0 NormalX=0 NormalY=0 NormalZ=1 AngleXU=0 Radius=1
    g24: Circle CenterX=-38.1838 CenterY=32.0162 CenterZ=0 NormalX=0 NormalY=0 NormalZ=1 AngleXU=0 Radius=1
    g25: LineSegment StartX=-38.1838 StartY=32.0162 StartZ=0 EndX=38.1838 EndY=108.384 EndZ=0
    g26: LineSegment StartX=-38.1838 StartY=108.384 StartZ=0 EndX=38.1838 EndY=32.0162 EndZ=0
    g27: LineSegment StartX=-34.6409 StartY=36.9733 StartZ=0 EndX=-36.7696 EndY=34.8447 EndZ=0
    g28: LineSegment StartX=-36.7696 StartY=34.8447 StartZ=0 EndX=-35.3553 EndY=33.4304 EndZ=0
    g29: LineSegment StartX=-35.3553 StartY=33.4304 StartZ=0 EndX=-33.2267 EndY=35.5591 EndZ=0
    g30: GeomPoint X=-36.0624 Y=34.1376 Z=0
    g31: LineSegment StartX=34.6409 StartY=36.9733 StartZ=0 EndX=36.7696 EndY=34.8447 EndZ=0
    g32: LineSegment StartX=33.2267 StartY=35.5591 StartZ=0 EndX=35.3553 EndY=33.4304 EndZ=0
    g33: LineSegment StartX=35.3553 StartY=33.4304 StartZ=0 EndX=36.7696 EndY=34.8447 EndZ=0
    g34: GeomPoint X=36.0624 Y=34.1376 Z=0
    g35: LineSegment StartX=-34.6409 StartY=103.427 StartZ=0 EndX=-36.7696 EndY=105.555 EndZ=0
    g36: LineSegment StartX=-33.2267 StartY=104.841 StartZ=0 EndX=-35.3553 EndY=106.97 EndZ=0
    g37: LineSegment StartX=-35.3553 StartY=106.97 StartZ=0 EndX=-36.7696 EndY=105.555 EndZ=0
    g38: GeomPoint X=-36.0624 Y=106.262 Z=0
    g39: LineSegment StartX=33.2267 StartY=104.841 StartZ=0 EndX=35.3553 EndY=106.97 EndZ=0
    g40: LineSegment StartX=34.6409 StartY=103.427 StartZ=0 EndX=36.7696 EndY=105.555 EndZ=0
    g41: LineSegment StartX=36.7696 StartY=105.555 StartZ=0 EndX=35.3553 EndY=106.97 EndZ=0
    g42: GeomPoint X=36.0624 Y=106.262 Z=0
  constraints (115):
    c: Coincident(g0,g1)
    c: Coincident(g1,g2)
    c: Coincident(g2,g3)
    c: Coincident(g3,g0)
    c: Horizontal(g0)
    c: Horizontal(g2)
    c: Vertical(g1)
    c: Vertical(g3)
    c: Symmetric(g0,g0,g-1)
    c: DistanceY(g0,g1) = 140.4
    c: DistanceX(g1,g2) = 114
    c: PointOnObject(g4,g0)
    c: Vertical(g4)
    c: Symmetric(g1,g2,g4)
    c: PointOnObject(g5,g3)
    c: Horizontal(g5)
    c: Symmetric(g1,g0,g5)
    c: PointOnObject(g6,g5)
    c: PointOnObject(g6,g4)
    c: Coincident(g7,g6)
    c: Radius(g7) = 48
    c: PointOnObject(g8,g2)
    c: PointOnObject(g8,g0)
    c: Vertical(g8)
    c: PointOnObject(g9,g2)
    c: PointOnObject(g9,g0)
    c: Vertical(g9)
    c: PointOnObject(g10,g9)
    c: PointOnObject(g10,g8)
    c: Horizontal(g10)
    c: PointOnObject(g11,g8)
    c: PointOnObject(g11,g9)
    c: Horizontal(g11)
    c: Coincident(g12,g10)
    c: Coincident(g13,g10)
    c: Coincident(g14,g11)
    c: Coincident(g15,g11)
    c: Radius(g12) = 1.5
    c: Equal(g12,g13)
    c: Equal(g12,g15)
    c: Equal(g12,g14)
    c: Coincident(g16,g7)
    c: Radius(g16) = 54
    c: Coincident(g17,g18)
    c: Coincident(g18,g19)
    c: Coincident(g19,g20)
    c: Coincident(g20,g17)
    c: Horizontal(g17)
    c: Horizontal(g19)
    c: Vertical(g18)
    c: Vertical(g20)
    c: PointOnObject(g17,g16)
    c: PointOnObject(g18,g16)
    c: PointOnObject(g17,g16)
    c: Equal(g17,g20)
    c: Coincident(g21,g17)
    c: Coincident(g22,g17)
    c: Coincident(g23,g18)
    c: Coincident(g24,g19)
    c: Radius(g22) = 1
    c: Equal(g22,g21)
    c: Equal(g22,g24)
    c: Equal(g22,g23)
    c: PointOnObject(g21,g8)
    c: PointOnObject(g22,g9)
    c: DistanceY(g12,g8) = 10
    c: DistanceY(g8,g14) = 10
    c: Coincident(g25,g24)
    c: Coincident(g25,g22)
    c: Coincident(g26,g21)
    c: Coincident(g26,g23)
    c: PointOnObject(g27,g7)
    c: Coincident(g28,g27)
    c: Coincident(g29,g28)
    c: PointOnObject(g29,g7)
    c: PointOnObject(g30,g25)
    c: Symmetric(g27,g28,g30)
    c: Parallel(g29,g25)
    c: Parallel(g25,g27)
    c: Distance(g28,g27) = 2
    c: Equal(g29,g27)
    c: Distance(g24,g30) = 3
    c: PointOnObject(g31,g7)
    c: PointOnObject(g32,g7)
    c: Coincident(g33,g32)
    c: Coincident(g33,g31)
    c: PointOnObject(g34,g26)
    c: Symmetric(g32,g31,g34)
    c: Parallel(g31,g32)
    c: Parallel(g32,g26)
    c: Equal(g31,g32)
    c: Equal(g32,g29)
    c: Equal(g28,g33)
    c: PointOnObject(g35,g7)
    c: PointOnObject(g36,g7)
    c: Coincident(g37,g36)
    c: Coincident(g37,g35)
    c: Parallel(g35,g36)
    c: Parallel(g36,g26)
    c: PointOnObject(g38,g26)
    c: Symmetric(g35,g36,g38)
    c: Equal(g35,g36)
    c: Equal(g36,g27)
    c: Equal(g28,g37)
    c: PointOnObject(g39,g7)
    c: PointOnObject(g40,g7)
    c: Coincident(g41,g40)
    c: Coincident(g41,g39)
    c: PointOnObject(g42,g25)
    c: Parallel(g39,g40)
    c: Parallel(g40,g25)
    c: Symmetric(g39,g40,g42)
    c: Equal(g39,g40)
    c: Equal(g40,g29)
    c: Equal(g28,g41)
FEATURE [Sketcher::SketchObject] Sketch054  label="master_sc_xz"
  ExternalGeometry = -> [Sketch053]
  FullyConstrained = true
  MapMode = 5
  Placement = pos=(0,0,0) rot=(1,0,0;1.5708rad)
  Support = -> [XZ_Plane004]
  expr: Constraints[5] = Spreadsheet.shell_outer_rad - <<Dimensions>>.shell_thick
  expr: Constraints[4] = <<Dimensions>>.base_thick
  sketch-geometry (15):
    g0: LineSegment StartX=-57 StartY=0 StartZ=0 EndX=57 EndY=0 EndZ=0
    g1: LineSegment StartX=0 StartY=11.8 StartZ=0 EndX=0 EndY=-133.5 EndZ=0
    g2: ArcOfCircle CenterX=0 CenterY=-133.5 CenterZ=0 NormalX=0 NormalY=0 NormalZ=1 AngleXU=0 Radius=145.3 StartAngle=1.16767 EndAngle=1.97392
    g3: LineSegment StartX=-57 StartY=0 StartZ=0 EndX=-57 EndY=0.152871 EndZ=0
    g4: LineSegment StartX=57 StartY=0 StartZ=0 EndX=57 EndY=0.152871 EndZ=0
    g5: LineSegment StartX=-48 StartY=1.64e-14 StartZ=0 EndX=-48 EndY=3.64259 EndZ=0
    g6: LineSegment StartX=48 StartY=1.64e-14 StartZ=0 EndX=48 EndY=3.64259 EndZ=0
    g7: LineSegment StartX=-39.1838 StartY=8e-15 StartZ=0 EndX=-39.1838 EndY=6.41684 EndZ=0
    g8: LineSegment StartX=-37.1838 StartY=8e-15 StartZ=0 EndX=-37.1838 EndY=6.96159 EndZ=0
    g9: LineSegment StartX=37.1838 StartY=8e-15 StartZ=0 EndX=37.1838 EndY=6.96159 EndZ=0
    g10: LineSegment StartX=39.1838 StartY=8e-15 StartZ=0 EndX=39.1838 EndY=6.41684 EndZ=0
    g11: LineSegment StartX=39.6838 StartY=2.2e-15 StartZ=0 EndX=39.6838 EndY=6.27585 EndZ=0
    g12: LineSegment StartX=36.6838 StartY=2.2e-15 StartZ=0 EndX=36.6838 EndY=7.093 EndZ=0
    g13: LineSegment StartX=-36.6838 StartY=2.2e-15 StartZ=0 EndX=-36.6838 EndY=7.093 EndZ=0
    g14: LineSegment StartX=-39.6838 StartY=2.2e-15 StartZ=0 EndX=-39.6838 EndY=6.27585 EndZ=0
  constraints (44):
    c: Coincident(g0,g-3)
    c: Coincident(g0,g-3)
    c: Vertical(g1)
    c: PointOnObject(g-1,g1)
    c: DistanceY(g-1,g1) = 11.8
    c: DistanceY(g1,g1) = 145.3
    c: Coincident(g2,g1)
    c: Coincident(g3,g0)
    c: Vertical(g3)
    c: Coincident(g2,g3)
    c: Coincident(g4,g0)
    c: Vertical(g4)
    c: Coincident(g2,g4)
    c: PointOnObject(g1,g2)
    c: Coincident(g5,g-4)
    c: PointOnObject(g5,g2)
    c: Vertical(g5)
    c: Coincident(g6,g-4)
    c: PointOnObject(g6,g2)
    c: Vertical(g6)
    c: Coincident(g7,g-5)
    c: PointOnObject(g7,g2)
    c: Vertical(g7)
    c: Coincident(g8,g-5)
    c: PointOnObject(g8,g2)
    c: Vertical(g8)
    c: Coincident(g9,g-6)
    c: PointOnObject(g9,g2)
    c: Vertical(g9)
    c: Coincident(g10,g-6)
    c: PointOnObject(g10,g2)
    c: Vertical(g10)
    c: Coincident(g11,g-7)
    c: PointOnObject(g11,g2)
    c: Vertical(g11)
    c: Coincident(g12,g-7)
    c: PointOnObject(g12,g2)
    c: Vertical(g12)
    c: Coincident(g13,g-8)
    c: PointOnObject(g13,g2)
    c: Vertical(g13)
    c: Coincident(g14,g-8)
    c: PointOnObject(g14,g2)
    c: Vertical(g14)
FEATURE [Sketcher::SketchObject] Sketch055  label="master_sc_yz"
  ExternalGeometry = -> [Sketch053,Sketch054]
  FullyConstrained = true
  MapMode = 5
  Placement = pos=(0,0,0) rot=(0.57735,0.57735,0.57735;2.0944rad)
  Support = -> [YZ_Plane004]
  expr: Constraints[81] = <<Dimensions>>.base_thick
  expr: Constraints[5] = <<Dimensions>>.base_thick
  sketch-geometry (55):
    g0: LineSegment StartX=0 StartY=2.31e-14 StartZ=0 EndX=140.4 EndY=2.31e-14 EndZ=0
    g1: LineSegment StartX=0 StartY=2.31e-14 StartZ=0 EndX=0 EndY=11.8 EndZ=0
    g2: LineSegment StartX=140.4 StartY=11.8 StartZ=0 EndX=140.4 EndY=2.31e-14 EndZ=0
    g3: LineSegment StartX=22.2 StartY=0 StartZ=0 EndX=22.2 EndY=11.8 EndZ=0
    g4: LineSegment StartX=118.2 StartY=0 StartZ=0 EndX=118.2 EndY=11.8 EndZ=0
    g5: Ellipse CenterX=10 CenterY=6.68443 CenterZ=0 NormalX=0 NormalY=0 NormalZ=1 MajorRadius=1.5 MinorRadius=0.408574 AngleXU=0
    g6: LineSegment StartX=11.5 StartY=6.68443 StartZ=0 EndX=8.5 EndY=6.68443 EndZ=0
    g7: LineSegment StartX=10 StartY=7.093 StartZ=0 EndX=10 EndY=6.27585 EndZ=0
    g8: GeomPoint X=11.4433 Y=6.68443 Z=0
    g9: GeomPoint X=8.55672 Y=6.68443 Z=0
    g10: LineSegment StartX=8.5 StartY=6.68443 StartZ=0 EndX=8.5 EndY=-1.07e-14 EndZ=0
    g11: LineSegment StartX=11.5 StartY=6.68443 StartZ=0 EndX=11.5 EndY=-9.8e-15 EndZ=0
    g12: LineSegment StartX=5.9e-15 StartY=6.41684 StartZ=0 EndX=140.4 EndY=6.41684 EndZ=0
    g13: LineSegment StartX=33.0162 StartY=0 StartZ=0 EndX=33.0162 EndY=6.96159 EndZ=0
    g14: LineSegment StartX=31.0162 StartY=-1.8e-15 StartZ=0 EndX=31.0162 EndY=6.96159 EndZ=0
    g15: GeomPoint X=31.0162 Y=6.41684 Z=0
    g16: Ellipse CenterX=32.0162 CenterY=6.68921 CenterZ=0 NormalX=0 NormalY=0 NormalZ=1 MajorRadius=1 MinorRadius=0.272373 AngleXU=-2.8e-15
    g17: LineSegment StartX=33.0162 StartY=6.68921 StartZ=0 EndX=31.0162 EndY=6.68921 EndZ=0
    g18: LineSegment StartX=32.0162 StartY=6.96159 StartZ=0 EndX=32.0162 EndY=6.41684 EndZ=0
    g19: GeomPoint X=32.9784 Y=6.68921 Z=0
    g20: GeomPoint X=31.054 Y=6.68921 Z=0
    g21: LineSegment StartX=33.0162 StartY=6.68921 StartZ=0 EndX=33.0162 EndY=0 EndZ=0
    g22: LineSegment StartX=31.0162 StartY=6.68921 StartZ=0 EndX=31.0162 EndY=-1.8e-15 EndZ=0
    g23: LineSegment StartX=5.2e-15 StartY=6.96159 StartZ=0 EndX=140.4 EndY=6.96159 EndZ=0
    g24: LineSegment StartX=107.384 StartY=2.13e-14 StartZ=0 EndX=107.384 EndY=6.41684 EndZ=0
    g25: LineSegment StartX=109.384 StartY=1.95e-14 StartZ=0 EndX=109.384 EndY=6.96159 EndZ=0
    g26: Ellipse CenterX=108.384 CenterY=6.68921 CenterZ=0 NormalX=0 NormalY=0 NormalZ=1 MajorRadius=1 MinorRadius=0.272373 AngleXU=1.29e-14
    g27: LineSegment StartX=109.384 StartY=6.68921 StartZ=0 EndX=107.384 EndY=6.68921 EndZ=0
    g28: LineSegment StartX=108.384 StartY=6.96159 StartZ=0 EndX=108.384 EndY=6.41684 EndZ=0
    g29: GeomPoint X=109.346 Y=6.68921 Z=0
    g30: GeomPoint X=107.422 Y=6.68921 Z=0
    g31: LineSegment StartX=107.384 StartY=6.68921 StartZ=0 EndX=107.384 EndY=2.13e-14 EndZ=0
    g32: GeomPoint X=109.384 Y=6.41684 Z=0
    g33: LineSegment StartX=109.384 StartY=6.68921 StartZ=0 EndX=109.384 EndY=1.95e-14 EndZ=0
    g34: LineSegment StartX=128.9 StartY=0 StartZ=0 EndX=128.9 EndY=6.68443 EndZ=0
    g35: LineSegment StartX=128.9 StartY=7.093 StartZ=0 EndX=128.9 EndY=6.27585 EndZ=0
    g36: LineSegment StartX=131.9 StartY=2.57e-14 StartZ=0 EndX=131.9 EndY=6.68443 EndZ=0
    g37: Ellipse CenterX=130.4 CenterY=6.68443 CenterZ=0 NormalX=0 NormalY=0 NormalZ=1 MajorRadius=1.5 MinorRadius=0.408574 AngleXU=0
    g38: LineSegment StartX=131.9 StartY=6.68443 StartZ=0 EndX=128.9 EndY=6.68443 EndZ=0
    g39: LineSegment StartX=130.4 StartY=7.093 StartZ=0 EndX=130.4 EndY=6.27585 EndZ=0
    g40: GeomPoint X=131.843 Y=6.68443 Z=0
    g41: GeomPoint X=128.957 Y=6.68443 Z=0
    g42: GeomPoint X=131.9 Y=6.27585 Z=0
    g43: LineSegment StartX=0 StartY=11.8 StartZ=0 EndX=22.2 EndY=11.8 EndZ=0
    g44: LineSegment StartX=118.2 StartY=11.8 StartZ=0 EndX=140.4 EndY=11.8 EndZ=0
    g45: LineSegment StartX=-1.13e-14 StartY=7.093 StartZ=0 EndX=140.4 EndY=7.093 EndZ=0
    g46: LineSegment StartX=70.2 StartY=7.2e-15 StartZ=0 EndX=70.2 EndY=11.8 EndZ=0
    g47: ArcOfEllipse CenterX=70.2 CenterY=11.8 CenterZ=0 NormalX=0 NormalY=0 NormalZ=1 MajorRadius=48 MinorRadius=4.70701 AngleXU=-1.11164e-08 StartAngle=3.14159 EndAngle=6.28318
    g48: LineSegment StartX=118.2 StartY=11.8 StartZ=0 EndX=22.2 EndY=11.8 EndZ=0
    g49: LineSegment StartX=70.2 StartY=16.507 StartZ=0 EndX=70.2 EndY=7.093 EndZ=0
    g50: GeomPoint X=117.969 Y=11.8 Z=0
    g51: GeomPoint X=22.4313 Y=11.8 Z=0
    g52: LineSegment StartX=22.2 StartY=11.8 StartZ=0 EndX=118.2 EndY=11.8 EndZ=0
    g53: LineSegment StartX=6e-15 StartY=6.27585 StartZ=0 EndX=140.4 EndY=6.27585 EndZ=0
    g54: LineSegment StartX=8.5 StartY=7.093 StartZ=0 EndX=8.5 EndY=6.27585 EndZ=0
  constraints (100):
    c: PointOnObject(g0,g-2)
    c: Coincident(g0,g-3)
    c: Horizontal(g0)
    c: Coincident(g1,g0)
    c: PointOnObject(g1,g-2)
    c: DistanceY(g0,g1) = 11.8
    c: Coincident(g2,g0)
    c: Vertical(g2)
    c: Coincident(g3,g-4)
    c: Vertical(g3)
    c: Coincident(g4,g-4)
    c: Vertical(g4)
    c: InternalAlignment(g6-g9 -> g5) x4
    c: Coincident(g10,g6)
    c: Coincident(g11,g6)
    c: Coincident(g12,g-7)
    c: Vertical(g13)
    c: Coincident(g13,g-9)
    c: Horizontal(g12)
    c: Coincident(g14,g-9)
    c: Vertical(g14)
    c: PointOnObject(g15,g14)
    c: PointOnObject(g15,g12)
    c: InternalAlignment(g17-g20 -> g16) x4
    c: Symmetric(g15,g13,g16)
    c: Symmetric(g15,g14,g17)
    c: PointOnObject(g18,g12)
    c: Coincident(g21,g17)
    c: Coincident(g21,g13)
    c: Coincident(g22,g17)
    c: Coincident(g22,g14)
    c: PointOnObject(g12,g2)
    c: Coincident(g23,g-8)
    c: PointOnObject(g23,g2)
    c: Horizontal(g23)
    c: PointOnObject(g14,g23)
    c: PointOnObject(g13,g23)
    c: Coincident(g24,g-12)
    c: Vertical(g24)
    c: Coincident(g25,g-12)
    c: Vertical(g25)
    c: InternalAlignment(g27-g30 -> g26) x4
    c: PointOnObject(g27,g25)
    c: Symmetric(g24,g25,g26)
    c: Coincident(g31,g27)
    c: Coincident(g31,g24)
    c: PointOnObject(g24,g12)
    c: PointOnObject(g25,g23)
    c: PointOnObject(g32,g12)
    c: PointOnObject(g32,g25)
    c: Symmetric(g32,g24,g28)
    c: Coincident(g33,g25)
    c: Coincident(g33,g27)
    c: Coincident(g34,g-13)
    c: Vertical(g34)
    c: Vertical(g35)
    c: Symmetric(g35,g35,g34)
    c: Coincident(g36,g-13)
    c: Vertical(g36)
    c: InternalAlignment(g38-g41 -> g37) x4
    c: Coincident(g38,g34)
    c: Coincident(g38,g36)
    c: Symmetric(g42,g35,g39)
    c: Coincident(g43,g1)
    c: Coincident(g43,g3)
    c: Horizontal(g43)
    c: Coincident(g44,g4)
    c: Coincident(g44,g2)
    c: Horizontal(g44)
    c: DistanceY(g0,g2) = 11.8
    c: Coincident(g-15,g45)
    c: PointOnObject(g45,g2)
    c: Horizontal(g45)
    c: Coincident(g46,g-14)
    c: Vertical(g46)
    c: InternalAlignment(g48-g51 -> g47) x4
    c: Coincident(g47,g46)
    c: Coincident(g47,g3)
    c: Coincident(g47,g4)
    c: PointOnObject(g49,g45)
    c: Coincident(g52,g3)
    c: Coincident(g52,g4)
    c: Equal(g48,g52)
    c: PointOnObject(g35,g45)
    c: Coincident(g53,g-11)
    c: PointOnObject(g53,g2)
    c: Horizontal(g53)
    c: PointOnObject(g7,g45)
    c: PointOnObject(g7,g53)
    c: Vertical(g11)
    c: Vertical(g10)
    c: PointOnObject(g54,g45)
    c: PointOnObject(g54,g53)
    c: Vertical(g54)
    c: Symmetric(g54,g54,g10)
    c: Coincident(g10,g-5)
    c: Coincident(g-5,g11)
    c: PointOnObject(g35,g53)
    c: PointOnObject(g39,g45)
    c: PointOnObject(g39,g53)
FEATURE [Sketcher::SketchObject] Sketch056
  ExternalGeometry = -> [Sketch053,Sketch054]
  FullyConstrained = true
  MapMode = 5
  Placement = pos=(0,0,0) rot=(1,0,0;1.5708rad)
  Support = -> [XZ_Plane004]
  expr: Constraints[8] = Spreadsheet.shell_outer_rad - <<Dimensions>>.shell_thick
  sketch-geometry (4):
    g0: LineSegment StartX=57 StartY=0 StartZ=0 EndX=-57 EndY=0 EndZ=0
    g1: LineSegment StartX=-57 StartY=0 StartZ=0 EndX=-57 EndY=0.152871 EndZ=0
    g2: LineSegment StartX=57 StartY=0 StartZ=0 EndX=57 EndY=0.152871 EndZ=0
    g3: ArcOfCircle CenterX=1.57e-14 CenterY=-133.5 CenterZ=0 NormalX=0 NormalY=0 NormalZ=1 AngleXU=0 Radius=145.3 StartAngle=1.16767 EndAngle=1.97392
  constraints (9):
    c: Coincident(g0,g-3)
    c: Coincident(g0,g-3)
    c: Coincident(g1,g0)
    c: Coincident(g2,g0)
    c: Coincident(g2,g3)
    c: Coincident(g2,g-4)
    c: Coincident(g1,g3)
    c: Coincident(g3,g-4)
    c: Radius(g3) = 145.3
FEATURE [PartDesign::Pad] Pad009  label="sc_plate"
  Direction = (1,1,1)
  Length = 140.4
  Length2 = 100
  Placement = pos=(0,0,0) rot=(1,0,0;1.5708rad)
  Profile = -> Sketch056
  Reversed = true
  Type = 0
  expr: Length = <<Dimensions>>.sc_len
FEATURE [Sketcher::SketchObject] Sketch057
  ExternalGeometry = -> [Sketch053]
  FullyConstrained = true
  MapMode = 5
  Placement = pos=(0,0,0) rot=(1,0,0;3.14159rad)
  Support = -> [Pad009]
  sketch-geometry (9):
    g0: Circle CenterX=0 CenterY=-70.2 CenterZ=0 NormalX=0 NormalY=0 NormalZ=1 AngleXU=0 Radius=48
    g1: Circle CenterX=38.1838 CenterY=-108.384 CenterZ=0 NormalX=0 NormalY=0 NormalZ=1 AngleXU=0 Radius=1
    g2: Circle CenterX=-38.1838 CenterY=-108.384 CenterZ=0 NormalX=0 NormalY=0 NormalZ=1 AngleXU=0 Radius=1
    g3: Circle CenterX=-38.1838 CenterY=-130.4 CenterZ=0 NormalX=0 NormalY=0 NormalZ=1 AngleXU=0 Radius=1.5
    g4: Circle CenterX=38.1838 CenterY=-130.4 CenterZ=0 NormalX=0 NormalY=0 NormalZ=1 AngleXU=0 Radius=1.5
    g5: Circle CenterX=-38.1838 CenterY=-32.0162 CenterZ=0 NormalX=0 NormalY=0 NormalZ=1 AngleXU=0 Radius=1
    g6: Circle CenterX=-38.1838 CenterY=-10 CenterZ=0 NormalX=0 NormalY=0 NormalZ=1 AngleXU=0 Radius=1.5
    g7: Circle CenterX=38.1838 CenterY=-10 CenterZ=0 NormalX=0 NormalY=0 NormalZ=1 AngleXU=0 Radius=1.5
    g8: Circle CenterX=38.1838 CenterY=-32.0162 CenterZ=0 NormalX=0 NormalY=0 NormalZ=1 AngleXU=0 Radius=1
  constraints (18):
    c: Coincident(g0,g-3)
    c: Coincident(g1,g-7)
    c: Coincident(g2,g-5)
    c: Coincident(g3,g-4)
    c: Coincident(g4,g-6)
    c: Coincident(g5,g-11)
    c: Coincident(g6,g-10)
    c: Coincident(g7,g-9)
    c: Coincident(g8,g-8)
    c: Equal(g0,g-3)
    c: Equal(g3,g-4)
    c: Equal(g4,g-6)
    c: Equal(g-5,g2)
    c: Equal(g1,g-7)
    c: Equal(g5,g-11)
    c: Equal(g6,g-10)
    c: Equal(g8,g-8)
    c: Equal(g7,g-9)
FEATURE [PartDesign::Pocket] Pocket006  label="sc_cutouts"
  BaseFeature = -> Pad009
  Length = 5
  Length2 = 100
  Placement = pos=(0,0,0) rot=(1,0,0;1.5708rad)
  Profile = -> Sketch057
  Type = 1
FEATURE [PartDesign::Body] Body003  label="alpha4-carrier"
  Group = -> [Sketch053,Sketch054,Sketch055,Sketch056,Pad009,Sketch057,Pocket006]
  Origin = -> Origin004
  Placement = pos=(0.0547037,-991.373,0) rot=(0,0,1;0rad)
  Tip = -> Pocket006
FEATURE [Part::FeaturePython] Clone003  label="part_speakercarrier"  # Draft clone (typed FeaturePython)
  AttacherType = Attacher::AttachEngine3D
  Fuse = false
  Objects = -> [Pocket006]
  Placement = pos=(327.048,-990.523,0) rot=(1,0,0;1.5708rad)
  Scale = (1,1,1)
FEATURE [Sketcher::SketchObject] Sketch058  label="master_strut_xy"
  FullyConstrained = true
  MapMode = 5
  Support = -> [XY_Plane005]
  expr: Constraints[52] = <<Dimensions>>.sc_len
  expr: Constraints[16] = <<Dimensions>>.fillet_rad
  expr: Constraints[51] = <<Dimensions>>.strut_wid
  expr: Constraints[54] = <<Dimensions>>.strut_cutout_len
  sketch-geometry (22):
    g0: LineSegment StartX=0 StartY=70.2 StartZ=0 EndX=0 EndY=-70.2 EndZ=0
    g1: LineSegment StartX=-14.5 StartY=70.2 StartZ=0 EndX=-14.5 EndY=-70.2 EndZ=0
    g2: LineSegment StartX=-14.5 StartY=-70.2 StartZ=0 EndX=14.5 EndY=-70.2 EndZ=0
    g3: LineSegment StartX=-14.5 StartY=70.2 StartZ=0 EndX=14.5 EndY=70.2 EndZ=0
    g4: ArcOfCircle CenterX=0 CenterY=55.4 CenterZ=0 NormalX=0 NormalY=0 NormalZ=1 AngleXU=0 Radius=3 StartAngle=1.5708 EndAngle=3.14159
    g5: ArcOfCircle CenterX=-6e-16 CenterY=-55.4 CenterZ=0 NormalX=0 NormalY=0 NormalZ=1 AngleXU=0 Radius=3 StartAngle=3.14159 EndAngle=4.71239
    g6: LineSegment StartX=-3 StartY=55.4 StartZ=0 EndX=-3 EndY=-55.4 EndZ=0
    g7: LineSegment StartX=14.5 StartY=70.2 StartZ=0 EndX=14.5 EndY=61.4 EndZ=0
    g8: LineSegment StartX=14.5 StartY=-70.2 StartZ=0 EndX=14.5 EndY=-61.4 EndZ=0
    g9: ArcOfCircle CenterX=11.5 CenterY=-61.4 CenterZ=0 NormalX=0 NormalY=0 NormalZ=1 AngleXU=0 Radius=3 StartAngle=0 EndAngle=1.5708
    g10: ArcOfCircle CenterX=11.5 CenterY=61.4 CenterZ=0 NormalX=0 NormalY=0 NormalZ=1 AngleXU=0 Radius=3 StartAngle=4.71239 EndAngle=6.28319
    g11: LineSegment StartX=11.5 StartY=61.4 StartZ=0 EndX=14.5 EndY=61.4 EndZ=0
    g12: LineSegment StartX=11.5 StartY=61.4 StartZ=0 EndX=11.5 EndY=58.4 EndZ=0
    g13: LineSegment StartX=0 StartY=55.4 StartZ=0 EndX=-3 EndY=55.4 EndZ=0
    g14: LineSegment StartX=0 StartY=55.4 StartZ=0 EndX=0 EndY=58.4 EndZ=0
    g15: LineSegment StartX=11.5 StartY=-61.4 StartZ=0 EndX=14.5 EndY=-61.4 EndZ=0
    g16: LineSegment StartX=11.5 StartY=-61.4 StartZ=0 EndX=11.5 EndY=-58.4 EndZ=0
    g17: LineSegment StartX=-6e-16 StartY=-55.4 StartZ=0 EndX=-6e-16 EndY=-58.4 EndZ=0
    g18: LineSegment StartX=-6e-16 StartY=-55.4 StartZ=0 EndX=-3 EndY=-55.4 EndZ=0
    g19: LineSegment StartX=11.5 StartY=-58.4 StartZ=0 EndX=0 EndY=-58.4 EndZ=0
    g20: LineSegment StartX=11.5 StartY=58.4 StartZ=0 EndX=0 EndY=58.4 EndZ=0
    g21: GeomPoint X=0 Y=0 Z=0
  constraints (58):
    c: Vertical(g0)
    c: Vertical(g1)
    c: Coincident(g2,g1)
    c: Horizontal(g2)
    c: Coincident(g3,g1)
    c: Horizontal(g3)
    c: Symmetric(g1,g3,g0)
    c: Coincident(g6,g4)
    c: Coincident(g6,g5)
    c: Vertical(g6)
    c: Coincident(g7,g3)
    c: Vertical(g7)
    c: Coincident(g8,g2)
    c: Vertical(g8)
    c: Coincident(g9,g8)
    c: Coincident(g10,g7)
    c: Radius(g10) = 3
    c: Equal(g10,g9)
    c: Equal(g10,g5)
    c: Equal(g10,g4)
    c: Coincident(g11,g10)
    c: Coincident(g11,g7)
    c: Horizontal(g11)
    c: Coincident(g12,g10)
    c: Coincident(g12,g10)
    c: Vertical(g12)
    c: Coincident(g13,g4)
    c: Horizontal(g13)
    c: Coincident(g14,g4)
    c: Vertical(g14)
    c: Coincident(g15,g9)
    c: Coincident(g16,g9)
    c: Vertical(g16)
    c: Coincident(g17,g5)
    c: Vertical(g17)
    c: Coincident(g18,g5)
    c: Horizontal(g18)
    c: Horizontal(g15)
    c: Coincident(g13,g4)
    c: Coincident(g14,g4)
    c: Coincident(g17,g5)
    c: Coincident(g5,g18)
    c: Coincident(g16,g9)
    c: Coincident(g15,g8)
    c: Coincident(g19,g9)
    c: Horizontal(g19)
    c: Coincident(g20,g10)
    c: Horizontal(g20)
    c: Coincident(g20,g4)
    c: Coincident(g5,g19)
    c: PointOnObject(g4,g0)
    c: DistanceX(g1,g2) = 29
    c: DistanceY(g1,g1) = 140.4
    c: Equal(g7,g8)
    c: DistanceY(g9,g10) = 116.8
    c: Symmetric(g1,g2,g0)
    c: Symmetric(g0,g0,g21)
    c: Coincident(g21,g-1)
FEATURE [Sketcher::SketchObject] Sketch059  label="master_strut_xz"
  ExternalGeometry = -> [Sketch058]
  FullyConstrained = true
  MapMode = 5
  Placement = pos=(0,0,0) rot=(1,0,0;1.5708rad)
  Support = -> [XZ_Plane005]
  expr: Constraints[16] = <<Dimensions>>.base_thick
  sketch-geometry (7):
    g0: LineSegment StartX=-14.5 StartY=1.56e-14 StartZ=0 EndX=-14.5 EndY=11.8 EndZ=0
    g1: LineSegment StartX=-14.5 StartY=11.8 StartZ=0 EndX=14.5 EndY=11.8 EndZ=0
    g2: LineSegment StartX=14.5 StartY=0 StartZ=0 EndX=14.5 EndY=11.8 EndZ=0
    g3: LineSegment StartX=11.5 StartY=-1.38e-14 StartZ=0 EndX=11.5 EndY=11.8 EndZ=0
    g4: LineSegment StartX=-3 StartY=0 StartZ=0 EndX=-3 EndY=11.8 EndZ=0
    g5: LineSegment StartX=0 StartY=0 StartZ=0 EndX=0 EndY=11.8 EndZ=0
    g6: LineSegment StartX=-14.5 StartY=1.56e-14 StartZ=0 EndX=14.5 EndY=0 EndZ=0
  constraints (19):
    c: Coincident(g0,g-3)
    c: Vertical(g0)
    c: Coincident(g1,g0)
    c: Horizontal(g1)
    c: Coincident(g2,g-3)
    c: Coincident(g2,g1)
    c: Vertical(g2)
    c: Coincident(g3,g-6)
    c: PointOnObject(g3,g1)
    c: Vertical(g3)
    c: Coincident(g4,g-4)
    c: PointOnObject(g4,g1)
    c: Vertical(g4)
    c: Coincident(g5,g-1)
    c: PointOnObject(g5,g1)
    c: Vertical(g5)
    c: DistanceY(g0,g0) = 11.8
    c: Coincident(g6,g0)
    c: Coincident(g6,g2)
FEATURE [Sketcher::SketchObject] Sketch060  label="master_strut_yz"
  ExternalGeometry = -> [Sketch058]
  FullyConstrained = true
  MapMode = 5
  Placement = pos=(0,0,0) rot=(0.57735,0.57735,0.57735;2.0944rad)
  Support = -> [YZ_Plane005]
  expr: Constraints[25] = <<Dimensions>>.base_thick
  sketch-geometry (10):
    g0: LineSegment StartX=70.2 StartY=2.36e-14 StartZ=0 EndX=70.2 EndY=11.8 EndZ=0
    g1: LineSegment StartX=61.4 StartY=1.3e-14 StartZ=0 EndX=61.4 EndY=11.8 EndZ=0
    g2: LineSegment StartX=58.4 StartY=1.3e-14 StartZ=0 EndX=58.4 EndY=11.8 EndZ=0
    g3: LineSegment StartX=55.4 StartY=1.72e-14 StartZ=0 EndX=55.4 EndY=11.8 EndZ=0
    g4: LineSegment StartX=-70.2 StartY=-1.55e-14 StartZ=0 EndX=-70.2 EndY=11.8 EndZ=0
    g5: LineSegment StartX=-61.4 StartY=-2.3e-14 StartZ=0 EndX=-61.4 EndY=11.8 EndZ=0
    g6: LineSegment StartX=-58.4 StartY=-2.14e-14 StartZ=0 EndX=-58.4 EndY=11.8 EndZ=0
    g7: LineSegment StartX=-55.4 StartY=-1.55e-14 StartZ=0 EndX=-55.4 EndY=11.8 EndZ=0
    g8: LineSegment StartX=-70.2 StartY=11.8 StartZ=0 EndX=70.2 EndY=11.8 EndZ=0
    g9: LineSegment StartX=-70.2 StartY=-1.55e-14 StartZ=0 EndX=70.2 EndY=2.36e-14 EndZ=0
  constraints (28):
    c: Coincident(g0,g-3)
    c: Vertical(g0)
    c: Coincident(g1,g-8)
    c: Vertical(g1)
    c: Coincident(g2,g-8)
    c: Vertical(g2)
    c: Coincident(g3,g-9)
    c: Vertical(g3)
    c: Coincident(g4,g-3)
    c: Vertical(g4)
    c: Coincident(g5,g-4)
    c: Vertical(g5)
    c: Coincident(g6,g-5)
    c: Vertical(g6)
    c: Coincident(g7,g-6)
    c: Vertical(g7)
    c: Coincident(g8,g4)
    c: Coincident(g8,g0)
    c: Horizontal(g8)
    c: PointOnObject(g5,g8)
    c: PointOnObject(g6,g8)
    c: PointOnObject(g7,g8)
    c: PointOnObject(g1,g8)
    c: PointOnObject(g2,g8)
    c: PointOnObject(g3,g8)
    c: DistanceY(g0,g0) = 11.8
    c: Coincident(g9,g4)
    c: Coincident(g9,g0)
FEATURE [Sketcher::SketchObject] Sketch061
  ExternalGeometry = -> [Sketch058]
  FullyConstrained = true
  MapMode = 5
  Support = -> [XY_Plane005]
  expr: Constraints[25] = <<Dimensions>>.fillet_rad
  expr: Constraints[18] = <<Dimensions>>.fillet_rad
  sketch-geometry (12):
    g0: LineSegment StartX=-14.5 StartY=70.2 StartZ=0 EndX=14.5 EndY=70.2 EndZ=0
    g1: LineSegment StartX=-14.5 StartY=70.2 StartZ=0 EndX=-14.5 EndY=-70.2 EndZ=0
    g2: LineSegment StartX=-14.5 StartY=-70.2 StartZ=0 EndX=14.5 EndY=-70.2 EndZ=0
    g3: LineSegment StartX=14.5 StartY=-70.2 StartZ=0 EndX=14.5 EndY=-61.4 EndZ=0
    g4: LineSegment StartX=11.5 StartY=-58.4 StartZ=0 EndX=0 EndY=-58.4 EndZ=0
    g5: LineSegment StartX=-3 StartY=-55.4 StartZ=0 EndX=-3 EndY=55.4 EndZ=0
    g6: LineSegment StartX=3e-16 StartY=58.4 StartZ=0 EndX=11.5 EndY=58.4 EndZ=0
    g7: LineSegment StartX=14.5 StartY=70.2 StartZ=0 EndX=14.5 EndY=61.4 EndZ=0
    g8: ArcOfCircle CenterX=3.58301e-11 CenterY=55.4 CenterZ=0 NormalX=0 NormalY=0 NormalZ=1 AngleXU=0 Radius=3 StartAngle=1.5708 EndAngle=3.14159
    g9: ArcOfCircle CenterX=11.5 CenterY=61.4 CenterZ=0 NormalX=0 NormalY=0 NormalZ=1 AngleXU=0 Radius=3 StartAngle=4.71239 EndAngle=6.28319
    g10: ArcOfCircle CenterX=-2e-16 CenterY=-55.4 CenterZ=0 NormalX=0 NormalY=0 NormalZ=1 AngleXU=0 Radius=3 StartAngle=3.14159 EndAngle=4.71239
    g11: ArcOfCircle CenterX=11.5 CenterY=-61.4 CenterZ=0 NormalX=0 NormalY=0 NormalZ=1 AngleXU=0 Radius=3 StartAngle=4.469e-13 EndAngle=1.5708
  constraints (28):
    c: Coincident(g0,g-4)
    c: Coincident(g0,g-5)
    c: Coincident(g1,g0)
    c: Coincident(g1,g-12)
    c: Coincident(g2,g1)
    c: Coincident(g2,g-12)
    c: Coincident(g3,g2)
    c: Coincident(g3,g-11)
    c: Coincident(g4,g-9)
    c: Coincident(g4,g-9)
    c: Coincident(g5,g-8)
    c: Coincident(g6,g-6)
    c: Coincident(g6,g-6)
    c: Coincident(g7,g0)
    c: Coincident(g5,g-8)
    c: Coincident(g7,g-5)
    c: Coincident(g8,g5)
    c: Coincident(g8,g6)
    c: Radius(g8) = 3
    c: Coincident(g9,g7)
    c: Coincident(g9,g6)
    c: Coincident(g10,g5)
    c: Coincident(g10,g4)
    c: Coincident(g11,g4)
    c: Coincident(g11,g3)
    c: Radius(g11) = 3
    c: Equal(g11,g10)
    c: Equal(g11,g9)
FEATURE [PartDesign::Pad] Pad010  label="strut_plate"
  Direction = (1,1,1)
  Length = 11.8
  Length2 = 100
  Profile = -> Sketch061
  Type = 0
  expr: Length = <<Dimensions>>.base_thick
FEATURE [PartDesign::Body] Body004  label="strut"
  Group = -> [Sketch058,Sketch059,Sketch060,Sketch061,Pad010]
  Origin = -> Origin005
  Placement = pos=(1.05983,-92.2072,0) rot=(0,0,1;0rad)
  Tip = -> Pad010
FEATURE [Part::FeaturePython] Clone004  label="part_strut"  # Draft clone (typed FeaturePython)
  AttacherType = Attacher::AttachEngine3D
  Fuse = false
  Objects = -> [Pad010]
  Placement = pos=(343.102,-91.7047,0) rot=(0,0,1;0rad)
  Scale = (1,1,1)
FEATURE [Sketcher::SketchObject] Sketch062  label="master_stand_xy"
  FullyConstrained = true
  MapMode = 5
  Support = -> [XY_Plane006]
  expr: Constraints[45] = <<Dimensions>>.strut_wid
  expr: Constraints[33] = <<Dimensions>>.stand_wid
  expr: Constraints[44] = <<Dimensions>>.base_thick
  expr: Constraints[43] = <<Dimensions>>.fillet_rad
  expr: Constraints[34] = <<Dimensions>>.base_thick
  expr: Constraints[60] = <<Dimensions>>.base_thick
  expr: Constraints[35] = <<Dimensions>>.base_thick
  expr: Constraints[29] = <<Dimensions>>.fillet_rad
  expr: Constraints[28] = <<Dimensions>>.stand_hei
  sketch-geometry (21):
    g0: LineSegment StartX=-14.5 StartY=0 StartZ=0 EndX=14.5 EndY=0 EndZ=0
    g1: LineSegment StartX=-14.5 StartY=0 StartZ=0 EndX=-14.5 EndY=-8.8 EndZ=0
    g2: LineSegment StartX=-11.5 StartY=-11.8 StartZ=0 EndX=-2.7 EndY=-11.8 EndZ=0
    g3: LineSegment StartX=14.7978 StartY=-11.8 StartZ=0 EndX=21.5 EndY=-25.6968 EndZ=0
    g4: LineSegment StartX=18.7978 StartY=-30 StartZ=0 EndX=12.2271 EndY=-30 EndZ=0
    g5: LineSegment StartX=9.7 StartY=-28.6166 StartZ=0 EndX=-0.172855 EndY=-13.1834 EndZ=0
    g6: ArcOfCircle CenterX=18.7978 CenterY=-27 CenterZ=0 NormalX=0 NormalY=0 NormalZ=1 AngleXU=0 Radius=3 StartAngle=4.71239 EndAngle=6.73255
    g7: ArcOfCircle CenterX=12.2271 CenterY=-27 CenterZ=0 NormalX=0 NormalY=0 NormalZ=1 AngleXU=0 Radius=3 StartAngle=3.7107 EndAngle=4.71239
    g8: ArcOfCircle CenterX=-2.7 CenterY=-14.8 CenterZ=0 NormalX=0 NormalY=0 NormalZ=1 AngleXU=0 Radius=3 StartAngle=0.569109 EndAngle=1.5708
    g9: LineSegment StartX=-2.7 StartY=-11.8 StartZ=0 EndX=-2.7 EndY=-14.8 EndZ=0
    g10: LineSegment StartX=12.2271 StartY=-27 StartZ=0 EndX=12.2271 EndY=-30 EndZ=0
    g11: LineSegment StartX=18.7978 StartY=-27 StartZ=0 EndX=18.7978 EndY=-30 EndZ=0
    g12: ArcOfCircle CenterX=-11.5 CenterY=-8.8 CenterZ=0 NormalX=0 NormalY=0 NormalZ=1 AngleXU=0 Radius=3 StartAngle=3.14159 EndAngle=4.71239
    g13: LineSegment StartX=-14.5 StartY=-8.8 StartZ=0 EndX=-11.5 EndY=-8.8 EndZ=0
    g14: LineSegment StartX=-11.5 StartY=-8.8 StartZ=0 EndX=-11.5 EndY=-11.8 EndZ=0
    g15: LineSegment StartX=14.5 StartY=0 StartZ=0 EndX=14.5 EndY=-10.4968 EndZ=0
    g16: ArcOfCircle CenterX=17.5 CenterY=-10.4968 CenterZ=0 NormalX=0 NormalY=0 NormalZ=1 AngleXU=0 Radius=3 StartAngle=3.14159 EndAngle=3.59096
    g17: LineSegment StartX=14.5 StartY=-10.4968 StartZ=0 EndX=17.5 EndY=-10.4968 EndZ=0
    g18: LineSegment StartX=10.5849 StartY=-30 StartZ=0 EndX=-8.6064 EndY=0 EndZ=0
    g19: LineSegment StartX=9.10692 StartY=0 StartZ=0 EndX=23.5753 EndY=-30 EndZ=0
    g20: LineSegment StartX=10.5849 StartY=-30 StartZ=0 EndX=23.5753 EndY=-30 EndZ=0
  constraints (61):
    c: PointOnObject(g0,g-1)
    c: Coincident(g1,g0)
    c: Vertical(g1)
    c: Horizontal(g2)
    c: Horizontal(g4)
    c: Coincident(g6,g4)
    c: Coincident(g6,g3)
    c: Coincident(g7,g5)
    c: Coincident(g7,g4)
    c: Coincident(g8,g2)
    c: Coincident(g8,g5)
    c: Coincident(g9,g2)
    c: Coincident(g9,g8)
    c: Vertical(g9)
    c: Coincident(g10,g7)
    c: Coincident(g10,g4)
    c: Coincident(g11,g6)
    c: Coincident(g11,g4)
    c: Vertical(g10)
    c: Vertical(g11)
    c: Coincident(g12,g1)
    c: Coincident(g12,g2)
    c: Coincident(g13,g1)
    c: Coincident(g13,g12)
    c: Coincident(g14,g12)
    c: Coincident(g14,g2)
    c: Horizontal(g13)
    c: Vertical(g14)
    c: DistanceY(g4,g0) = 30
    c: Radius(g8) = 3
    c: Equal(g8,g12)
    c: Equal(g8,g7)
    c: Equal(g8,g6)
    c: DistanceX(g0,g3) = 36
    c: DistanceX(g5,g3) = 11.8
    c: DistanceY(g2,g0) = 11.8
    c: Coincident(g15,g0)
    c: Vertical(g15)
    c: Coincident(g16,g15)
    c: Coincident(g16,g3)
    c: Coincident(g17,g15)
    c: Coincident(g17,g16)
    c: Horizontal(g17)
    c: Radius(g16) = 3
    c: DistanceY(g3,g0) = 11.8
    c: DistanceX(g0,g0) = 29
    c: PointOnObject(g18,g0)
    c: Tangent(g18,g5)
    c: Tangent(g8,g18)
    c: Tangent(g7,g18)
    c: Coincident(g20,g18)
    c: Coincident(g20,g19)
    c: Parallel(g20,g4)
    c: PointOnObject(g4,g20)
    c: Parallel(g19,g3)
    c: PointOnObject(g3,g19)
    c: Tangent(g6,g19)
    c: Tangent(g19,g16)
    c: PointOnObject(g19,g0)
    c: Symmetric(g0,g0,g-1)
    c: DistanceX(g1,g2) = 11.8
FEATURE [Sketcher::SketchObject] Sketch063
  ExternalGeometry = -> [Sketch062]
  FullyConstrained = true
  MapMode = 5
  Support = -> [XY_Plane006]
  expr: Constraints[29] = <<Dimensions>>.fillet_rad
  expr: Constraints[25] = <<Dimensions>>.fillet_rad
  sketch-geometry (12):
    g0: LineSegment StartX=-14.5 StartY=0 StartZ=0 EndX=14.5 EndY=0 EndZ=0
    g1: LineSegment StartX=14.5 StartY=0 StartZ=0 EndX=14.5 EndY=-10.4968 EndZ=0
    g2: LineSegment StartX=-14.5 StartY=0 StartZ=0 EndX=-14.5 EndY=-8.8 EndZ=0
    g3: LineSegment StartX=-11.5 StartY=-11.8 StartZ=0 EndX=-2.7 EndY=-11.8 EndZ=0
    g4: LineSegment StartX=-0.172855 StartY=-13.1834 StartZ=0 EndX=9.7 EndY=-28.6166 EndZ=0
    g5: LineSegment StartX=12.2271 StartY=-30 StartZ=0 EndX=18.7978 EndY=-30 EndZ=0
    g6: LineSegment StartX=21.5 StartY=-25.6968 StartZ=0 EndX=14.7978 EndY=-11.8 EndZ=0
    g7: ArcOfCircle CenterX=-11.5 CenterY=-8.8 CenterZ=0 NormalX=0 NormalY=0 NormalZ=1 AngleXU=0 Radius=3 StartAngle=3.14159 EndAngle=4.71239
    g8: ArcOfCircle CenterX=-2.7 CenterY=-14.8 CenterZ=0 NormalX=0 NormalY=0 NormalZ=1 AngleXU=0 Radius=3 StartAngle=0.569109 EndAngle=1.5708
    g9: ArcOfCircle CenterX=17.5 CenterY=-10.4968 CenterZ=0 NormalX=0 NormalY=0 NormalZ=1 AngleXU=0 Radius=3 StartAngle=3.14159 EndAngle=3.59096
    g10: ArcOfCircle CenterX=9.7 CenterY=-31.6166 CenterZ=0 NormalX=0 NormalY=0 NormalZ=1 AngleXU=0 Radius=3 StartAngle=1.5708 EndAngle=6.85229
    g11: ArcOfCircle CenterX=21.5 CenterY=-28.6968 CenterZ=0 NormalX=0 NormalY=0 NormalZ=1 AngleXU=0 Radius=3 StartAngle=3.59096 EndAngle=7.85398
  constraints (30):
    c: Coincident(g0,g-4)
    c: Coincident(g0,g-5)
    c: Coincident(g1,g0)
    c: Coincident(g1,g-10)
    c: Coincident(g2,g0)
    c: Coincident(g2,g-6)
    c: Coincident(g3,g-7)
    c: Coincident(g3,g-8)
    c: Coincident(g4,g-9)
    c: Coincident(g4,g-14)
    c: Coincident(g5,g-14)
    c: Coincident(g5,g-13)
    c: Coincident(g6,g-12)
    c: Coincident(g6,g-11)
    c: Coincident(g7,g2)
    c: Coincident(g7,g3)
    c: Coincident(g8,g3)
    c: Coincident(g8,g4)
    c: Coincident(g9,g1)
    c: Coincident(g9,g6)
    c: Coincident(g10,g4)
    c: Coincident(g10,g5)
    c: Coincident(g11,g6)
    c: Coincident(g11,g5)
    c: Radius(g-14) = 3
    c: Radius(g11) = 3
    c: Equal(g11,g9)
    c: Equal(g11,g8)
    c: Equal(g11,g7)
    c: Radius(g10) = 3
FEATURE [PartDesign::Pad] Pad011  label="stand_plate"
  Direction = (1,1,1)
  Length = 11.8
  Length2 = 100
  Profile = -> Sketch063
  Type = 0
  expr: Length = <<Dimensions>>.base_thick
FEATURE [Sketcher::SketchObject] Sketch064  label="master_stand_xz"
  ExternalGeometry = -> [Sketch062]
  FullyConstrained = true
  MapMode = 5
  Placement = pos=(0,0,0) rot=(1,0,0;1.5708rad)
  Support = -> [XZ_Plane006]
  expr: Constraints[32] = <<Dimensions>>.base_thick
  sketch-geometry (12):
    g0: LineSegment StartX=-14.5 StartY=2e-15 StartZ=0 EndX=-14.5 EndY=11.8 EndZ=0
    g1: LineSegment StartX=-14.5 StartY=11.8 StartZ=0 EndX=21.7978 EndY=11.8 EndZ=0
    g2: LineSegment StartX=21.7978 StartY=11.8 StartZ=0 EndX=21.7978 EndY=0 EndZ=0
    g3: LineSegment StartX=18.7978 StartY=-1.11e-14 StartZ=0 EndX=18.7978 EndY=11.8 EndZ=0
    g4: LineSegment StartX=12.2271 StartY=-1.11e-14 StartZ=0 EndX=12.2271 EndY=11.8 EndZ=0
    g5: LineSegment StartX=9.7 StartY=-1.08e-14 StartZ=0 EndX=9.7 EndY=11.8 EndZ=0
    g6: LineSegment StartX=14.7978 StartY=-2.7e-15 StartZ=0 EndX=14.7978 EndY=11.8 EndZ=0
    g7: LineSegment StartX=14.5 StartY=-1.2e-15 StartZ=0 EndX=14.5 EndY=11.8 EndZ=0
    g8: LineSegment StartX=-11.5 StartY=-2.7e-15 StartZ=0 EndX=-11.5 EndY=11.8 EndZ=0
    g9: LineSegment StartX=-2.7 StartY=-2.7e-15 StartZ=0 EndX=-2.7 EndY=11.8 EndZ=0
    g10: LineSegment StartX=-0.172855 StartY=-3e-15 StartZ=0 EndX=-0.172855 EndY=11.8 EndZ=0
    g11: LineSegment StartX=-14.5 StartY=2e-15 StartZ=0 EndX=21.7978 EndY=0 EndZ=0
  constraints (34):
    c: Coincident(g0,g-4)
    c: Vertical(g0)
    c: Coincident(g1,g0)
    c: Horizontal(g1)
    c: Vertical(g2)
    c: Coincident(g2,g-10)
    c: Coincident(g2,g1)
    c: Coincident(g3,g-10)
    c: PointOnObject(g3,g1)
    c: Vertical(g3)
    c: Coincident(g4,g-9)
    c: PointOnObject(g4,g1)
    c: Coincident(g5,g-8)
    c: PointOnObject(g5,g1)
    c: Vertical(g5)
    c: Vertical(g4)
    c: Coincident(g6,g-11)
    c: PointOnObject(g6,g1)
    c: Vertical(g6)
    c: Coincident(g7,g-12)
    c: Vertical(g7)
    c: PointOnObject(g7,g1)
    c: Coincident(g8,g-5)
    c: PointOnObject(g8,g1)
    c: Vertical(g8)
    c: Coincident(g9,g-6)
    c: PointOnObject(g9,g1)
    c: Vertical(g9)
    c: Coincident(g10,g-7)
    c: PointOnObject(g10,g1)
    c: Vertical(g10)
    c: Coincident(g11,g0)
    c: DistanceY(g0,g0) = 11.8
    c: Coincident(g11,g2)
FEATURE [Sketcher::SketchObject] Sketch065  label="master_stand_yz"
  ExternalGeometry = -> [Sketch062,Sketch064]
  FullyConstrained = true
  MapMode = 5
  Placement = pos=(0,0,0) rot=(0.57735,0.57735,0.57735;2.0944rad)
  Support = -> [YZ_Plane006]
  sketch-geometry (8):
    g0: LineSegment StartX=-4e-16 StartY=11.8 StartZ=0 EndX=-30 EndY=11.8 EndZ=0
    g1: LineSegment StartX=-8.8 StartY=2.5e-15 StartZ=0 EndX=-8.8 EndY=11.8 EndZ=0
    g2: LineSegment StartX=-10.4968 StartY=-8e-15 StartZ=0 EndX=-10.4968 EndY=11.8 EndZ=0
    g3: LineSegment StartX=-11.8 StartY=8e-16 StartZ=0 EndX=-11.8 EndY=11.8 EndZ=0
    g4: LineSegment StartX=-13.1834 StartY=-2.7e-15 StartZ=0 EndX=-13.1834 EndY=11.8 EndZ=0
    g5: LineSegment StartX=-30 StartY=-2.01e-14 StartZ=0 EndX=-30 EndY=11.8 EndZ=0
    g6: LineSegment StartX=-28.6166 StartY=-1.91e-14 StartZ=0 EndX=-28.6166 EndY=11.8 EndZ=0
    g7: LineSegment StartX=-25.6968 StartY=-2.16e-14 StartZ=0 EndX=-25.6968 EndY=11.8 EndZ=0
  constraints (23):
    c: Coincident(g0,g-4)
    c: Horizontal(g0)
    c: Coincident(g1,g-5)
    c: PointOnObject(g1,g0)
    c: Vertical(g1)
    c: Coincident(g2,g-6)
    c: PointOnObject(g2,g0)
    c: Vertical(g2)
    c: Coincident(g3,g-5)
    c: PointOnObject(g3,g0)
    c: Vertical(g3)
    c: Coincident(g4,g-7)
    c: PointOnObject(g4,g0)
    c: Vertical(g4)
    c: Coincident(g5,g-10)
    c: Vertical(g5)
    c: Coincident(g6,g-10)
    c: PointOnObject(g6,g0)
    c: Vertical(g6)
    c: Coincident(g7,g-9)
    c: PointOnObject(g7,g0)
    c: Vertical(g7)
    c: Coincident(g0,g5)
FEATURE [PartDesign::Body] Body005  label="stand"
  Group = -> [Sketch062,Sketch064,Sketch065,Sketch063,Pad011]
  Origin = -> Origin006
  Placement = pos=(-4.97532,-533.161,1.39431) rot=(0,0,1;0rad)
  Tip = -> Pad011
FEATURE [Part::FeaturePython] Clone005  label="part_stand"  # Draft clone (typed FeaturePython)
  AttacherType = Attacher::AttachEngine3D
  Fuse = false
  Objects = -> [Pad011]
  Placement = pos=(314.693,-526.079,3.07444) rot=(0,0,1;0rad)
  Scale = (1,1,1)
FEATURE [TechDraw::DrawSVGTemplate] Template001
  EditableTexts = Designed_by_Name=<owner>; Drawing_number=Drawing number; FC-Date=20-Nov-2021; FC-SC=0,33; FC-SH=Sheet; FC-Title=AnywereAmps Alpha 1.2; Subtitle=Top; Weight=Weight
  Height = 210
  Orientation = 1
  Width = 297
FEATURE [TechDraw::DrawProjGroupItem] ProjItem  label="Front"
  CoarseView = false
  Direction = (0,0,1)
  Focus = 100
  HardHidden = false
  IsoCount = 0
  IsoHidden = false
  IsoVisible = false
  LockPosition = true
  Perspective = false
  Rotation = 0
  RotationVector = (1,0,0)
  Scale = 0.33
  ScaleType = 2
  SeamHidden = false
  SeamVisible = true
  SmoothHidden = false
  SmoothVisible = true
  Source = -> [Pocket005]
  Type = 0
  X = 0
  XDirection = (1,0,0)
  Y = 0
FEATURE [TechDraw::DrawProjGroupItem] ProjItem001  label="FrontBottomRight"
  CoarseView = false
  Direction = (0.57735,-0.57735,0.57735)
  Focus = 100
  HardHidden = false
  IsoCount = 0
  IsoHidden = false
  IsoVisible = false
  LockPosition = false
  Perspective = false
  Rotation = 0
  RotationVector = (1,0,0)
  Scale = 0.33
  ScaleType = 2
  SeamHidden = false
  SeamVisible = true
  SmoothHidden = false
  SmoothVisible = true
  Source = -> [Pocket005]
  Type = 9
  X = -101.28
  XDirection = (0.707107,0,-0.707107)
  Y = 111.173
FEATURE [TechDraw::DrawProjGroupItem] ProjItem002  label="Top"
  CoarseView = false
  Direction = (0,1,0)
  Focus = 100
  HardHidden = false
  IsoCount = 0
  IsoHidden = false
  IsoVisible = false
  LockPosition = false
  Perspective = false
  Rotation = 0
  RotationVector = (1,0,0)
  Scale = 0.33
  ScaleType = 2
  SeamHidden = false
  SeamVisible = true
  SmoothHidden = false
  SmoothVisible = true
  Source = -> [Pocket005]
  Type = 4
  X = 0
  XDirection = (1,0,0)
  Y = -163.038
FEATURE [TechDraw::DrawProjGroupItem] ProjItem003  label="Right"
  CoarseView = false
  Direction = (1,0,1e-16)
  Focus = 100
  HardHidden = false
  IsoCount = 0
  IsoHidden = false
  IsoVisible = false
  LockPosition = false
  Perspective = false
  Rotation = 0
  RotationVector = (1,0,0)
  Scale = 0.33
  ScaleType = 2
  SeamHidden = false
  SeamVisible = true
  SmoothHidden = false
  SmoothVisible = true
  Source = -> [Pocket005]
  Type = 2
  X = -66.942
  XDirection = (1e-16,0,-1)
  Y = 0
FEATURE [TechDraw::DrawProjGroup] ProjGroup
  Anchor = -> ProjItem
  AutoDistribute = true
  LockPosition = false
  ProjectionType = 0
  Rotation = 0
  Scale = 0.33
  ScaleType = 2
  Source = -> [Pocket005]
  Views = -> [ProjItem,ProjItem001,ProjItem002,ProjItem003]
  X = 89.5413
  Y = 139.646
  spacingX = 15
  spacingY = 15
FEATURE [TechDraw::DrawViewDimension] Dimension
  Arbitrary = false
  ArbitraryTolerances = false
  EqualTolerance = true
  FormatSpec = R%.2f
  FormatSpecOverTolerance = %+.2f
  FormatSpecUnderTolerance = %+.2f
  Inverted = false
  LockPosition = false
  MeasureType = 1
  OverTolerance = 0
  References2D = -> [ProjItem]
  Rotation = 0
  Scale = 0.5
  ScaleType = 0
  TheoreticalExact = false
  Type = 4
  UnderTolerance = 0
  X = -54.9607
  Y = -19.5077
FEATURE [TechDraw::DrawViewDimension] Dimension001
  Arbitrary = false
  ArbitraryTolerances = false
  EqualTolerance = true
  FormatSpec = R%.2f
  FormatSpecOverTolerance = %+.2f
  FormatSpecUnderTolerance = %+.2f
  Inverted = false
  LockPosition = false
  MeasureType = 1
  OverTolerance = 0
  References2D = -> [ProjItem]
  Rotation = 0
  Scale = 0.5
  ScaleType = 0
  TheoreticalExact = false
  Type = 4
  UnderTolerance = 0
  X = 21.9843
  Y = 17.9131
FEATURE [TechDraw::DrawViewDimension] Dimension002
  Arbitrary = false
  ArbitraryTolerances = false
  EqualTolerance = true
  FormatSpec = R%.2f
  FormatSpecOverTolerance = %+.2f
  FormatSpecUnderTolerance = %+.2f
  Inverted = false
  LockPosition = false
  MeasureType = 1
  OverTolerance = 0
  References2D = -> [ProjItem]
  Rotation = 0
  Scale = 0.5
  ScaleType = 0
  TheoreticalExact = false
  Type = 4
  UnderTolerance = 0
  X = 16.0811
  Y = 24.0199
FEATURE [TechDraw::DrawViewDimension] Dimension003
  Arbitrary = false
  ArbitraryTolerances = false
  EqualTolerance = true
  FormatSpec = ⌀%.2f
  FormatSpecOverTolerance = %+.2f
  FormatSpecUnderTolerance = %+.2f
  Inverted = false
  LockPosition = false
  MeasureType = 1
  OverTolerance = 0
  References2D = -> [ProjItem]
  Rotation = 0
  Scale = 0.5
  ScaleType = 0
  TheoreticalExact = false
  Type = 5
  UnderTolerance = 0
  X = 30.8664
  Y = 51.7134
FEATURE [TechDraw::DrawViewDimension] Dimension005
  Arbitrary = false
  ArbitraryTolerances = false
  EqualTolerance = true
  FormatSpec = %.2f
  FormatSpecOverTolerance = %+.2f
  FormatSpecUnderTolerance = %+.2f
  Inverted = false
  LockPosition = false
  MeasureType = 1
  OverTolerance = 0
  References2D = -> [ProjItem003]
  Rotation = 0
  Scale = 0.5
  ScaleType = 0
  TheoreticalExact = false
  Type = 1
  UnderTolerance = 0
  X = 6.47361
  Y = -60.6406
FEATURE [TechDraw::DrawViewDimension] Dimension006
  Arbitrary = false
  ArbitraryTolerances = false
  EqualTolerance = true
  FormatSpec = %.2f
  FormatSpecOverTolerance = %+.2f
  FormatSpecUnderTolerance = %+.2f
  Inverted = false
  LockPosition = false
  MeasureType = 1
  OverTolerance = 0
  References2D = -> [ProjItem003]
  Rotation = 0
  Scale = 0.5
  ScaleType = 0
  TheoreticalExact = false
  Type = 1
  UnderTolerance = 0
  X = 7.27804
  Y = -70.5716
FEATURE [TechDraw::DrawViewAnnotation] Annotation
  Font = osifont
  LineSpace = 80
  LockPosition = false
  MaxWidth = -1
  Rotation = 0
  Scale = 0.5
  ScaleType = 0
  Text = Predrill sink:  | diameter: 2mm | depth: 8mm
  TextSize = 5
  TextStyle = 0
  X = 36.7304
  Y = 41.6575
FEATURE [TechDraw::DrawViewDimension] Dimension015
  Arbitrary = false
  ArbitraryTolerances = false
  EqualTolerance = true
  FormatSpec = %.2f
  FormatSpecOverTolerance = %+.2f
  FormatSpecUnderTolerance = %+.2f
  Inverted = false
  LockPosition = false
  MeasureType = 1
  OverTolerance = 0
  References2D = -> [ProjItem]
  Rotation = 0
  Scale = 0.5
  ScaleType = 0
  TheoreticalExact = false
  Type = 1
  UnderTolerance = 0
  X = -6.52472
  Y = -5.43661
FEATURE [TechDraw::DrawViewDimension] Dimension016
  Arbitrary = false
  ArbitraryTolerances = false
  EqualTolerance = true
  FormatSpec = %.2f
  FormatSpecOverTolerance = %+.2f
  FormatSpecUnderTolerance = %+.2f
  Inverted = false
  LockPosition = false
  MeasureType = 1
  OverTolerance = 0
  References2D = -> [ProjItem]
  Rotation = 0
  Scale = 0.5
  ScaleType = 0
  TheoreticalExact = false
  Type = 2
  UnderTolerance = 0
  X = -25.8873
  Y = -15.4384
FEATURE [TechDraw::DrawViewDimension] Dimension017
  Arbitrary = false
  ArbitraryTolerances = false
  EqualTolerance = true
  FormatSpec = %.2f
  FormatSpecOverTolerance = %+.2f
  FormatSpecUnderTolerance = %+.2f
  Inverted = false
  LockPosition = false
  MeasureType = 1
  OverTolerance = 0
  References2D = -> [ProjItem]
  Rotation = 0
  Scale = 0.5
  ScaleType = 0
  TheoreticalExact = false
  Type = 2
  UnderTolerance = 0
  X = -15.8352
  Y = -18.0681
FEATURE [TechDraw::DrawViewDimension] Dimension018
  Arbitrary = false
  ArbitraryTolerances = false
  EqualTolerance = true
  FormatSpec = %.2f
  FormatSpecOverTolerance = %+.2f
  FormatSpecUnderTolerance = %+.2f
  Inverted = false
  LockPosition = false
  MeasureType = 1
  OverTolerance = 0
  References2D = -> [ProjItem]
  Rotation = 0
  Scale = 0.5
  ScaleType = 0
  TheoreticalExact = false
  Type = 2
  UnderTolerance = 0
  X = 4.73868
  Y = -5.12208
FEATURE [TechDraw::DrawViewDimension] Dimension019
  Arbitrary = false
  ArbitraryTolerances = false
  EqualTolerance = true
  FormatSpec = %.2f
  FormatSpecOverTolerance = %+.2f
  FormatSpecUnderTolerance = %+.2f
  Inverted = false
  LockPosition = false
  MeasureType = 1
  OverTolerance = 0
  References2D = -> [ProjItem]
  Rotation = 0
  Scale = 0.5
  ScaleType = 0
  TheoreticalExact = false
  Type = 2
  UnderTolerance = 0
  X = -17.6895
  Y = 7.95258
FEATURE [TechDraw::DrawViewDimension] Dimension020
  Arbitrary = false
  ArbitraryTolerances = false
  EqualTolerance = true
  FormatSpec = %.2f
  FormatSpecOverTolerance = %+.2f
  FormatSpecUnderTolerance = %+.2f
  Inverted = false
  LockPosition = false
  MeasureType = 1
  OverTolerance = 0
  References2D = -> [ProjItem]
  Rotation = 0
  Scale = 0.5
  ScaleType = 0
  TheoreticalExact = false
  Type = 2
  UnderTolerance = 0
  X = -28.8175
  Y = 7.40426
FEATURE [TechDraw::DrawViewDimension] Dimension021
  Arbitrary = false
  ArbitraryTolerances = false
  EqualTolerance = true
  FormatSpec = %.2f
  FormatSpecOverTolerance = %+.2f
  FormatSpecUnderTolerance = %+.2f
  Inverted = false
  LockPosition = false
  MeasureType = 1
  OverTolerance = 0
  References2D = -> [ProjItem]
  Rotation = 0
  Scale = 0.5
  ScaleType = 0
  TheoreticalExact = false
  Type = 2
  UnderTolerance = 0
  X = -3.05645
  Y = 24.5533
FEATURE [TechDraw::DrawViewDimension] Dimension022
  Arbitrary = false
  ArbitraryTolerances = false
  EqualTolerance = true
  FormatSpec = %.2f
  FormatSpecOverTolerance = %+.2f
  FormatSpecUnderTolerance = %+.2f
  Inverted = false
  LockPosition = false
  MeasureType = 1
  OverTolerance = 0
  References2D = -> [ProjItem]
  Rotation = 0
  Scale = 0.5
  ScaleType = 0
  TheoreticalExact = false
  Type = 1
  UnderTolerance = 0
  X = -17.9182
  Y = 17.6369
FEATURE [TechDraw::DrawPage] Page001  label="Drawing_top"
  KeepUpdated = true
  NextBalloonIndex = 1
  ProjectionType = 0
  Scale = 0.5
  Template = -> Template001
  Views = -> [ProjGroup,Dimension,Dimension001,Dimension002,Dimension003,Dimension005,Dimension006,Annotation,Dimension015,Dimension016,Dimension017,Dimension018,Dimension019,Dimension020,Dimension021,Dimension022]
FEATURE [Sketcher::SketchObject] Sketch067
  FullyConstrained = true
  MapMode = 5
  Support = -> [XY_Plane008]
  expr: Constraints[114] = <<Dimensions>>.drill_3_rad
  expr: Constraints[84] = <<Dimensions>>.predrill_3_rad
  expr: Constraints[83] = <<Dimensions>>.duvel_6_rad
  expr: Constraints[77] = <<Dimensions>>.base_thick
  expr: Constraints[85] = <<Dimensions>>.duvel_dist
  expr: Constraints[64] = <<Dimensions>>.base_thick
  expr: Constraints[40] = <<Dimensions>>.stand_hei + 0.2
  expr: Constraints[86] = <<Dimensions>>.fastener_dist
  expr: Constraints[37] = <<Dimensions>>.strut_wid / 2 + 0.1
  expr: Constraints[28] = <<Dimensions>>.sc_len + 0.2
  expr: Constraints[95] = <<Dimensions>>.base_thick
  expr: Constraints[29] = <<Dimensions>>.strut_wid + 0.2
  expr: Constraints[27] = 12.1
  expr: Constraints[24] = <<Dimensions>>.fillet_rad - 0.05
  sketch-geometry (52):
    g0: LineSegment StartX=0 StartY=0 StartZ=0 EndX=29.2 EndY=0 EndZ=0
    g1: LineSegment StartX=29.2 StartY=0 StartZ=0 EndX=29.2 EndY=-10 EndZ=0
    g2: LineSegment StartX=0 StartY=0 StartZ=0 EndX=0 EndY=-12.1 EndZ=0
    g3: LineSegment StartX=0 StartY=-12.1 StartZ=0 EndX=11.9506 EndY=-12.1 EndZ=0
    g4: LineSegment StartX=29.2 StartY=-10 StartZ=0 EndX=33.2 EndY=-10 EndZ=0
    g5: LineSegment StartX=33.2 StartY=-10 StartZ=0 EndX=33.2 EndY=-30.2 EndZ=0
    g6: LineSegment StartX=33.2 StartY=-30.2 StartZ=0 EndX=29.2 EndY=-30.2 EndZ=0
    g7: LineSegment StartX=29.2 StartY=-30.2 StartZ=0 EndX=29.2 EndY=-140.6 EndZ=0
    g8: LineSegment StartX=29.2 StartY=-140.6 StartZ=0 EndX=0 EndY=-140.6 EndZ=0
    g9: LineSegment StartX=0 StartY=-140.6 StartZ=0 EndX=0 EndY=-128.5 EndZ=0
    g10: LineSegment StartX=0 StartY=-128.5 StartZ=0 EndX=11.65 EndY=-128.5 EndZ=0
    g11: ArcOfCircle CenterX=11.9506 CenterY=-15.05 CenterZ=0 NormalX=0 NormalY=0 NormalZ=1 AngleXU=0 Radius=2.95 StartAngle=6.26331 EndAngle=7.85398
    g12: ArcOfCircle CenterX=11.65 CenterY=-125.55 CenterZ=0 NormalX=0 NormalY=0 NormalZ=1 AngleXU=0 Radius=2.95 StartAngle=4.71239 EndAngle=6.28319
    g13: LineSegment StartX=14.9 StartY=-15.1086 StartZ=0 EndX=14.6 EndY=-30.2 EndZ=0
    g14: LineSegment StartX=14.6 StartY=-30.2 StartZ=0 EndX=14.6 EndY=-125.55 EndZ=0
    g15: LineSegment StartX=14.6 StartY=-30.2 StartZ=0 EndX=29.2 EndY=-30.2 EndZ=0
    g16: LineSegment StartX=-18 StartY=6 StartZ=0 EndX=47.2 EndY=6 EndZ=0
    g17: LineSegment StartX=47.2 StartY=6 StartZ=0 EndX=47.2 EndY=-146.6 EndZ=0
    g18: LineSegment StartX=47.2 StartY=-146.6 StartZ=0 EndX=-18 EndY=-146.6 EndZ=0
    g19: LineSegment StartX=-18 StartY=-146.6 StartZ=0 EndX=-18 EndY=6 EndZ=0
    g20: LineSegment StartX=-29.8 StartY=29.6 StartZ=0 EndX=59 EndY=29.6 EndZ=0
    g21: LineSegment StartX=59 StartY=29.6 StartZ=0 EndX=59 EndY=17.8 EndZ=0
    g22: LineSegment StartX=59 StartY=17.8 StartZ=0 EndX=-29.8 EndY=17.8 EndZ=0
    g23: LineSegment StartX=-29.8 StartY=17.8 StartZ=0 EndX=-29.8 EndY=29.6 EndZ=0
    g24: LineSegment StartX=14.6 StartY=17.8 StartZ=0 EndX=14.6 EndY=6 EndZ=0
    g25: LineSegment StartX=-18 StartY=17.8 StartZ=0 EndX=-18 EndY=29.6 EndZ=0
    g26: LineSegment StartX=47.2 StartY=17.8 StartZ=0 EndX=47.2 EndY=29.6 EndZ=0
    g27: LineSegment StartX=-18 StartY=17.8 StartZ=0 EndX=-18 EndY=6 EndZ=0
    g28: LineSegment StartX=-29.8 StartY=23.7 StartZ=0 EndX=59 EndY=23.7 EndZ=0
    g29: Circle CenterX=23.2 CenterY=23.7 CenterZ=0 NormalX=0 NormalY=0 NormalZ=1 AngleXU=0 Radius=3
    g30: Circle CenterX=6.1 CenterY=23.7 CenterZ=0 NormalX=0 NormalY=0 NormalZ=1 AngleXU=0 Radius=1
    g31: LineSegment StartX=59 StartY=53.2 StartZ=0 EndX=-29.8 EndY=53.2 EndZ=0
    g32: LineSegment StartX=-29.8 StartY=53.2 StartZ=0 EndX=-29.8 EndY=41.4 EndZ=0
    g33: LineSegment StartX=-29.8 StartY=41.4 StartZ=0 EndX=59 EndY=41.4 EndZ=0
    g34: LineSegment StartX=59 StartY=41.4 StartZ=0 EndX=59 EndY=53.2 EndZ=0
    g35: LineSegment StartX=59 StartY=47.3 StartZ=0 EndX=-29.8 EndY=47.3 EndZ=0
    g36: Circle CenterX=23.2 CenterY=47.3 CenterZ=0 NormalX=0 NormalY=0 NormalZ=1 AngleXU=0 Radius=3
    g37: Circle CenterX=6.1 CenterY=47.3 CenterZ=0 NormalX=0 NormalY=0 NormalZ=1 AngleXU=0 Radius=1.5
    g38: LineSegment StartX=14.6 StartY=41.4 StartZ=0 EndX=14.6 EndY=17.8 EndZ=0
    g39: LineSegment StartX=23.2 StartY=47.3 StartZ=0 EndX=23.2 EndY=23.7 EndZ=0
    g40: LineSegment StartX=-29.8 StartY=41.4 StartZ=0 EndX=-29.8 EndY=29.6 EndZ=0
    g41: LineSegment StartX=6.1 StartY=47.3 StartZ=0 EndX=6.1 EndY=23.7 EndZ=0
    g42: LineSegment StartX=-18 StartY=41.4 StartZ=0 EndX=-18 EndY=29.6 EndZ=0
    g43: LineSegment StartX=-18 StartY=41.4 StartZ=0 EndX=-18 EndY=53.2 EndZ=0
    g44: LineSegment StartX=47.2 StartY=41.4 StartZ=0 EndX=47.2 EndY=53.2 EndZ=0
    g45: Circle CenterX=-12 CenterY=47.3 CenterZ=0 NormalX=0 NormalY=0 NormalZ=1 AngleXU=0 Radius=1.5
    g46: Circle CenterX=-12 CenterY=23.7 CenterZ=0 NormalX=0 NormalY=0 NormalZ=1 AngleXU=0 Radius=1.5
    g47: Circle CenterX=41.2 CenterY=47.3 CenterZ=0 NormalX=0 NormalY=0 NormalZ=1 AngleXU=0 Radius=1.5
    g48: Circle CenterX=41.2 CenterY=23.7 CenterZ=0 NormalX=0 NormalY=0 NormalZ=1 AngleXU=0 Radius=1.5
    g49: LineSegment StartX=41.2 StartY=47.3 StartZ=0 EndX=41.2 EndY=23.7 EndZ=0
    g50: LineSegment StartX=-12 StartY=47.3 StartZ=0 EndX=-12 EndY=23.7 EndZ=0
    g51: GeomPoint X=14.6 Y=23.7 Z=0
  constraints (143):
    c: Horizontal(g0)
    c: Coincident(g1,g0)
    c: Vertical(g1)
    c: Coincident(g2,g0)
    c: Vertical(g2)
    c: Coincident(g3,g2)
    c: Horizontal(g3)
    c: Coincident(g4,g1)
    c: Coincident(g5,g4)
    c: Vertical(g5)
    c: Horizontal(g4)
    c: Coincident(g6,g5)
    c: Horizontal(g6)
    c: Coincident(g7,g6)
    c: Vertical(g7)
    c: Coincident(g8,g7)
    c: Horizontal(g8)
    c: Coincident(g9,g8)
    c: Vertical(g9)
    c: Coincident(g10,g9)
    c: Horizontal(g10)
    c: Tangent(g12,g10) = -1.5708
    c: Tangent(g11,g3) = 1.5708
    c: Equal(g11,g12)
    c: Radius(g12) = 2.95
    c: Equal(g6,g4)
    c: Equal(g2,g9)
    c: DistanceY(g2,g0) = 12.1
    c: DistanceY(g8,g0) = 140.6
    c: DistanceX(g8,g7) = 29.2
    c: Tangent(g11,g13) = 1.5708
    c: Equal(g0,g8)
    c: DistanceY(g1,g0) = 10
    c: DistanceX(g6,g5) = 4
    c: DistanceX(g2,g11) = 14.9
    c: Vertical(g14)
    c: Tangent(g14,g12) = 1.5708
    c: DistanceX(g14,g6) = 14.6
    c: Horizontal(g15)
    c: Coincident(g15,g6)
    c: DistanceY(g13,g0) = 30.2
    c: Coincident(g13,g14)
    c: Coincident(g15,g13)
    c: Coincident(g0,g-1)
    c: Coincident(g16,g17)
    c: Coincident(g17,g18)
    c: Coincident(g18,g19)
    c: Coincident(g19,g16)
    c: Horizontal(g16)
    c: Horizontal(g18)
    c: Vertical(g17)
    c: Vertical(g19)
    c: DistanceX(g16,g0) = 18
    c: DistanceX(g0,g16) = 18
    c: DistanceY(g0,g16) = 6
    c: DistanceY(g18,g8) = 6
    c: Coincident(g20,g21)
    c: Coincident(g21,g22)
    c: Coincident(g22,g23)
    c: Coincident(g23,g20)
    c: Horizontal(g20)
    c: Horizontal(g22)
    c: Vertical(g21)
    c: Vertical(g23)
    c: DistanceY(g22,g20) = 11.8
    c: Vertical(g24)
    c: Symmetric(g22,g21,g24)
    c: Symmetric(g16,g16,g24)
    c: PointOnObject(g25,g20)
    c: Vertical(g25)
    c: PointOnObject(g26,g20)
    c: Vertical(g26)
    c: Symmetric(g26,g25,g24)
    c: Vertical(g27)
    c: Coincident(g27,g16)
    c: Coincident(g27,g25)
    c: PointOnObject(g26,g22)
    c: DistanceX(g22,g25) = 11.8
    c: Horizontal(g28)
    c: PointOnObject(g28,g21)
    c: Symmetric(g20,g22,g28)
    c: PointOnObject(g29,g28)
    c: PointOnObject(g30,g28)
    c: Radius(g29) = 3
    c: Radius(g30) = 1
    c: DistanceX(g29,g0) = 6
    c: DistanceX(g30,g0) = 23.1
    c: Coincident(g31,g32)
    c: Coincident(g32,g33)
    c: Coincident(g33,g34)
    c: Coincident(g34,g31)
    c: Horizontal(g31)
    c: Horizontal(g33)
    c: Vertical(g32)
    c: Vertical(g34)
    c: DistanceY(g33,g31) = 11.8
    c: Horizontal(g35)
    c: PointOnObject(g35,g32)
    c: Symmetric(g31,g33,g35)
    c: PointOnObject(g36,g35)
    c: PointOnObject(g37,g35)
    c: Equal(g29,g36) = 3
    c: Vertical(g38)
    c: Symmetric(g32,g33,g38)
    c: Coincident(g38,g24)
    c: Vertical(g39)
    c: Coincident(g39,g36)
    c: Coincident(g39,g29)
    c: Vertical(g40)
    c: Coincident(g40,g32)
    c: Coincident(g40,g20)
    c: Vertical(g41)
    c: Coincident(g41,g37)
    c: Coincident(g41,g30)
    c: Radius(g37) = 1.5
    c: Vertical(g42)
    c: Coincident(g42,g25)
    c: PointOnObject(g42,g33)
    c: Coincident(g43,g42)
    c: PointOnObject(g43,g31)
    c: Vertical(g43)
    c: PointOnObject(g44,g31)
    c: Vertical(g44)
    c: Symmetric(g43,g44,g38)
    c: Equal(g40,g32)
    c: Equal(g27,g23)
    c: PointOnObject(g45,g35)
    c: PointOnObject(g46,g28)
    c: PointOnObject(g47,g35)
    c: PointOnObject(g48,g28)
    c: Equal(g48,g47)
    c: Equal(g47,g45)
    c: Equal(g45,g46)
    c: Equal(g46,g37)
    c: Vertical(g49)
    c: Vertical(g50)
    c: Coincident(g50,g45)
    c: Coincident(g50,g46)
    c: Coincident(g49,g48)
    c: Coincident(g49,g47)
    c: PointOnObject(g51,g38)
    c: Symmetric(g46,g48,g51)
    c: DistanceX(g16,g46) = 6
FEATURE [PartDesign::Body] Body007  label="fixture_stand_struts"
  Group = -> [Sketch067]
  Origin = -> Origin008
  Placement = pos=(-298.165,-28.5084,16.8837) rot=(0,0,1;0rad)
FEATURE [Sketcher::SketchObject] Sketch069  label="master_nutzen"
  FullyConstrained = true
  MapMode = 5
  Placement = pos=(-410.585,-1457.78,0) rot=(0,0,1;0rad)
  Support = -> [XY_Plane009]
  expr: Constraints[8] = <<Dimensions>>.nutz_wid
  expr: Constraints[9] = <<Dimensions>>.nutz_length
  sketch-geometry (6):
    g0: LineSegment StartX=-311 StartY=-1075.81 StartZ=0 EndX=311 EndY=-1075.81 EndZ=0
    g1: LineSegment StartX=311 StartY=-1075.81 StartZ=0 EndX=311 EndY=-1697.81 EndZ=0
    g2: LineSegment StartX=311 StartY=-1697.81 StartZ=0 EndX=-311 EndY=-1697.81 EndZ=0
    g3: LineSegment StartX=-311 StartY=-1697.81 StartZ=0 EndX=-311 EndY=-1075.81 EndZ=0
    g4: LineSegment StartX=0 StartY=-1075.81 StartZ=0 EndX=0 EndY=-1697.81 EndZ=0
    g5: LineSegment StartX=-311 StartY=-1386.81 StartZ=0 EndX=311 EndY=-1386.81 EndZ=0
  constraints (18):
    c: Coincident(g0,g1)
    c: Coincident(g1,g2)
    c: Coincident(g2,g3)
    c: Coincident(g3,g0)
    c: Horizontal(g0)
    c: Horizontal(g2)
    c: Vertical(g1)
    c: Vertical(g3)
    c: DistanceX(g0,g0) = 622
    c: DistanceY(g2,g0) = 622
    c: DistanceY(g0,g-1) = 1075.81
    c: PointOnObject(g4,g0)
    c: Vertical(g4)
    c: PointOnObject(g5,g1)
    c: Horizontal(g5)
    c: Symmetric(g0,g2,g5)
    c: Symmetric(g2,g1,g4)
    c: PointOnObject(g4,g-2)
FEATURE [Sketcher::SketchObject] Sketch070  label="top_xy"
  ExternalGeometry = -> [Sketch]
  FullyConstrained = true
  MapMode = 5
  Support = -> [XY_Plane001]
  sketch-geometry (12):
    g0: Circle CenterX=0 CenterY=0 CenterZ=0 NormalX=0 NormalY=0 NormalZ=1 AngleXU=0 Radius=151.5
    g1: Circle CenterX=0 CenterY=0 CenterZ=0 NormalX=0 NormalY=0 NormalZ=1 AngleXU=0 Radius=145.3
    g2: Circle CenterX=0 CenterY=-75.75 CenterZ=0 NormalX=0 NormalY=0 NormalZ=1 AngleXU=0 Radius=38
    g3: Circle CenterX=-71.8274 CenterY=-98.8619 CenterZ=0 NormalX=0 NormalY=0 NormalZ=1 AngleXU=0 Radius=1
    g4: Circle CenterX=-38 CenterY=-113.75 CenterZ=0 NormalX=0 NormalY=0 NormalZ=1 AngleXU=0 Radius=1
    g5: Circle CenterX=38 CenterY=-113.75 CenterZ=0 NormalX=0 NormalY=0 NormalZ=1 AngleXU=0 Radius=1
    g6: Circle CenterX=71.8274 CenterY=-98.8619 CenterZ=0 NormalX=0 NormalY=0 NormalZ=1 AngleXU=0 Radius=1
    g7: Circle CenterX=38 CenterY=14.25 CenterZ=0 NormalX=0 NormalY=0 NormalZ=1 AngleXU=0 Radius=1
    g8: Circle CenterX=116.219 CenterY=37.7619 CenterZ=0 NormalX=0 NormalY=0 NormalZ=1 AngleXU=0 Radius=1
    g9: Circle CenterX=-38 CenterY=14.25 CenterZ=0 NormalX=0 NormalY=0 NormalZ=1 AngleXU=0 Radius=1
    g10: Circle CenterX=-116.219 CenterY=37.7619 CenterZ=0 NormalX=0 NormalY=0 NormalZ=1 AngleXU=0 Radius=1
    g11: Circle CenterX=0 CenterY=139.3 CenterZ=0 NormalX=0 NormalY=0 NormalZ=1 AngleXU=0 Radius=3
  constraints (24):
    c: Coincident(g0,g-1)
    c: Coincident(g1,g0)
    c: Coincident(g2,g-11)
    c: Coincident(g8,g-9)
    c: Coincident(g9,g-7)
    c: Coincident(g10,g-6)
    c: Coincident(g11,g-5)
    c: Equal(g11,g-5)
    c: Equal(g-3,g0)
    c: Equal(g-4,g1)
    c: Equal(g-9,g8)
    c: Equal(g2,g-11)
    c: Equal(g9,g-7)
    c: Equal(g-6,g10)
    c: Coincident(g-15,g7)
    c: Equal(g7,g-15)
    c: Equal(g3,g-16)
    c: Coincident(g-16,g3)
    c: Coincident(g4,g-17)
    c: Equal(g4,g-17)
    c: Coincident(g5,g-18)
    c: Equal(g-18,g5)
    c: Coincident(g6,g-19)
    c: Equal(g6,g-19)
FEATURE [PartDesign::Body] Body  label="top"
  Group = -> [Sketch,Sketch001,Sketch039,Sketch049,Pad,Sketch050,Pad008,Sketch051,Pocket,Sketch052,Pocket005,Sketch070]
  Origin = -> Origin001
  Placement = pos=(0,150,0) rot=(0,0,1;0rad)
  Tip = -> Pocket005
FEATURE [Part::Part2DObjectPython] Clone2D  label="top_xy (2D)"  # Draft 2D object (typed FeaturePython)
  Fuse = false
  Objects = -> [Sketch070]
  Placement = pos=(330,-1237.86,0) rot=(0,0,1;0rad)
  Scale = (1,1,1)
FEATURE [Part::Part2DObjectPython] Clone2D001  label="master_bottom_xy (2D)"  # Draft 2D object (typed FeaturePython)
  Fuse = false
  Objects = -> [Sketch009]
  Placement = pos=(450,-1535,0) rot=(0,0,1;0rad)
  Scale = (1,1,1)
FEATURE [Part::Part2DObjectPython] Clone2D002  label="ampcarrier001"  # Draft 2D object (typed FeaturePython)
  Fuse = false
  Objects = -> [Sketch036]
  Placement = pos=(228,-1550,0) rot=(0,0,1;0rad)
  Scale = (1,1,1)
FEATURE [Part::Part2DObjectPython] Clone2D003  label="strut_2"  # Draft 2D object (typed FeaturePython)
  Fuse = false
  Objects = -> [Sketch058]
  Placement = pos=(585,-1157,0) rot=(0,0,1;3.14159rad)
  Scale = (1,1,1)
FEATURE [Part::Part2DObjectPython] Clone2D004  label="strut_1"  # Draft 2D object (typed FeaturePython)
  Fuse = false
  Objects = -> [Clone2D003]
  Placement = pos=(585,-1315,0) rot=(0,0,1;3.14159rad)
  Scale = (1,1,1)
FEATURE [Part::Part2DObjectPython] Clone2D005  label="strut_3"  # Draft 2D object (typed FeaturePython)
  Fuse = false
  Objects = -> [Clone2D003]
  Placement = pos=(530,-1315,0) rot=(0,0,1;0rad)
  Scale = (1,1,1)
FEATURE [Part::Part2DObjectPython] Clone2D006  label="strut_4"  # Draft 2D object (typed FeaturePython)
  Fuse = false
  Objects = -> [Clone2D004]
  Placement = pos=(530,-1157,0) rot=(0,0,1;0rad)
  Scale = (1,1,1)
FEATURE [Part::Part2DObjectPython] Clone2D007  label="stand_1"  # Draft 2D object (typed FeaturePython)
  Fuse = false
  Objects = -> [Sketch062]
  Placement = pos=(555,-1120,0) rot=(0,0,1;0rad)
  Scale = (1,1,1)
FEATURE [Part::Part2DObjectPython] Clone2D008  label="stand_2"  # Draft 2D object (typed FeaturePython)
  Fuse = false
  Objects = -> [Clone2D007]
  Placement = pos=(555,-1278,0) rot=(0,0,1;0rad)
  Scale = (1,1,1)
FEATURE [Part::Part2DObjectPython] Clone2D009  label="stand_3"  # Draft 2D object (typed FeaturePython)
  Fuse = false
  Objects = -> [Clone2D008]
  Placement = pos=(470,-1087,0) rot=(0,0,1;0rad)
  Scale = (1,1,1)
FEATURE [Part::Part2DObjectPython] Clone2D010  label="stand_4"  # Draft 2D object (typed FeaturePython)
  Fuse = false
  Objects = -> [Clone2D009]
  Placement = pos=(560,-1195,0) rot=(0,0,1;3.14159rad)
  Scale = (1,1,1)
FEATURE [Part::Part2DObjectPython] Clone2D011  label="stand_5"  # Draft 2D object (typed FeaturePython)
  Fuse = false
  Objects = -> [Clone2D010]
  Placement = pos=(560,-1353,0) rot=(0,0,1;3.14159rad)
  Scale = (1,1,1)
FEATURE [Part::Part2DObjectPython] Clone2D012  label="nutzen001"  # Draft 2D object (typed FeaturePython)
  Fuse = false
  Objects = -> [Sketch069]
  Placement = pos=(311,0,0) rot=(0,0,1;0rad)
  Scale = (1,1,1)
  expr: .Placement.Base.x = <<Dimensions>>.nutz_wid / 2
FEATURE [Part::Part2DObjectPython] Clone2D013  label="speakercarrier001"  # Draft 2D object (typed FeaturePython)
  Fuse = false
  Objects = -> [Sketch053]
  Placement = pos=(87,-1235.81,0) rot=(0,0,1;0rad)
  Scale = (1,1,1)
  expr: .Placement.Base.y = -1215.81 - 20
  expr: .Placement.Base.x = <<Dimensions>>.sc_wid / 2 + 30
FEATURE [Part::Part2DObjectPython] Clone2D014  label="Sketch056 (2D)"  # Draft 2D object (typed FeaturePython)
  Fuse = false
  Objects = -> [Sketch056]
  Placement = pos=(0,0,0) rot=(1,0,0;1.5708rad)
  Scale = (1,1,1)
FEATURE [PartDesign::Pad] Pad012
  Direction = (1,1,1)
  Length = 432.1
  Length2 = 100
  Placement = pos=(0,0,0) rot=(1,0,0;1.5708rad)
  Profile = -> Clone2D014
  Type = 0
  expr: Length = 3 * 140 + 2 * 6.05
FEATURE [PartDesign::Body] Body009  label="all-speaker-carriers"
  Group = -> [Clone2D014,Pad012]
  Origin = -> Origin010
  Placement = pos=(-561.887,-1094.68,0) rot=(0,0,1;0rad)
  Tip = -> Pad012
FEATURE [Sketcher::SketchObject] Sketch073  label="master_sc_piezo"
  FullyConstrained = true
  MapMode = 5
  Support = -> [XY_Plane011]
  expr: Constraints[111] = <<Dimensions>>.predrill_3_rad + <<Dimensions>>.sc_pz_grl_wid
  expr: Constraints[66] = <<Dimensions>>.ampcarrier_pre_dist
  expr: Constraints[9] = <<Dimensions>>.sc_len
  expr: Constraints[37] = <<Dimensions>>.drill_3_rad
  expr: Constraints[10] = <<Dimensions>>.sc_pz_wid
  expr: Constraints[20] = <<Dimensions>>.sc_pz_cut_rad
  expr: Constraints[42] = <<Dimensions>>.sc_pz_mnt_rad
  expr: Constraints[105] = <<Dimensions>>.sc_pz_grl_wid
  expr: Constraints[59] = <<Dimensions>>.predrill_3_rad
  expr: Constraints[65] = <<Dimensions>>.ampcarrier_pre_dist
  sketch-geometry (43):
    g0: LineSegment StartX=47.3 StartY=0 StartZ=0 EndX=-47.3 EndY=0 EndZ=0
    g1: LineSegment StartX=-47.3 StartY=0 StartZ=0 EndX=-47.3 EndY=140.4 EndZ=0
    g2: LineSegment StartX=-47.3 StartY=140.4 StartZ=0 EndX=47.3 EndY=140.4 EndZ=0
    g3: LineSegment StartX=47.3 StartY=140.4 StartZ=0 EndX=47.3 EndY=0 EndZ=0
    g4: LineSegment StartX=-3e-16 StartY=140.4 StartZ=0 EndX=-3e-16 EndY=0 EndZ=0
    g5: LineSegment StartX=-47.3 StartY=70.2 StartZ=0 EndX=47.3 EndY=70.2 EndZ=0
    g6: GeomPoint X=-3e-16 Y=70.2 Z=0
    g7: Circle CenterX=-3e-16 CenterY=70.2 CenterZ=0 NormalX=0 NormalY=0 NormalZ=1 AngleXU=0 Radius=35.5
    g8: LineSegment StartX=-30.4056 StartY=140.4 StartZ=0 EndX=-30.4056 EndY=0 EndZ=0
    g9: LineSegment StartX=30.4056 StartY=140.4 StartZ=0 EndX=30.4056 EndY=0 EndZ=0
    g10: LineSegment StartX=30.4056 StartY=130.4 StartZ=0 EndX=-30.4056 EndY=130.4 EndZ=0
    g11: LineSegment StartX=-30.4056 StartY=10 StartZ=0 EndX=30.4056 EndY=10 EndZ=0
    g12: Circle CenterX=-30.4056 CenterY=130.4 CenterZ=0 NormalX=0 NormalY=0 NormalZ=1 AngleXU=0 Radius=1.5
    g13: Circle CenterX=30.4056 CenterY=130.4 CenterZ=0 NormalX=0 NormalY=0 NormalZ=1 AngleXU=0 Radius=1.5
    g14: Circle CenterX=-30.4056 CenterY=10 CenterZ=0 NormalX=0 NormalY=0 NormalZ=1 AngleXU=0 Radius=1.5
    g15: Circle CenterX=30.4056 CenterY=10 CenterZ=0 NormalX=0 NormalY=0 NormalZ=1 AngleXU=0 Radius=1.5
    g16: Circle CenterX=-3e-16 CenterY=70.2 CenterZ=0 NormalX=0 NormalY=0 NormalZ=1 AngleXU=0 Radius=43
    g17: LineSegment StartX=-30.4056 StartY=100.606 StartZ=0 EndX=30.4056 EndY=100.606 EndZ=0
    g18: LineSegment StartX=30.4056 StartY=100.606 StartZ=0 EndX=30.4056 EndY=39.7944 EndZ=0
    g19: LineSegment StartX=30.4056 StartY=39.7944 StartZ=0 EndX=-30.4056 EndY=39.7944 EndZ=0
    g20: LineSegment StartX=-30.4056 StartY=39.7944 StartZ=0 EndX=-30.4056 EndY=100.606 EndZ=0
    g21: Circle CenterX=-30.4056 CenterY=100.606 CenterZ=0 NormalX=0 NormalY=0 NormalZ=1 AngleXU=0 Radius=1
    g22: Circle CenterX=30.4056 CenterY=100.606 CenterZ=0 NormalX=0 NormalY=0 NormalZ=1 AngleXU=0 Radius=1
    g23: Circle CenterX=30.4056 CenterY=39.7944 CenterZ=0 NormalX=0 NormalY=0 NormalZ=1 AngleXU=0 Radius=1
    g24: Circle CenterX=-30.4056 CenterY=39.7944 CenterZ=0 NormalX=0 NormalY=0 NormalZ=1 AngleXU=0 Radius=1
    g25: LineSegment StartX=-24.3852 StartY=95.9994 StartZ=0 EndX=-27.5772 EndY=99.1914 EndZ=0
    g26: LineSegment StartX=-27.5772 StartY=99.1914 StartZ=0 EndX=-28.9914 EndY=97.7772 EndZ=0
    g27: LineSegment StartX=-28.9914 StartY=97.7772 StartZ=0 EndX=-25.7994 EndY=94.5852 EndZ=0
    g28: LineSegment StartX=-30.4056 StartY=100.606 StartZ=0 EndX=30.4056 EndY=39.7944 EndZ=0
    g29: LineSegment StartX=30.4056 StartY=100.606 StartZ=0 EndX=-30.4056 EndY=39.7944 EndZ=0
    g30: GeomPoint X=-28.2843 Y=98.4843 Z=0
    g31: LineSegment StartX=-25.7994 StartY=45.8148 StartZ=0 EndX=-28.9914 EndY=42.6228 EndZ=0
    g32: LineSegment StartX=-28.9914 StartY=42.6228 StartZ=0 EndX=-27.5772 EndY=41.2086 EndZ=0
    g33: LineSegment StartX=-27.5772 StartY=41.2086 StartZ=0 EndX=-24.3852 EndY=44.4006 EndZ=0
    g34: GeomPoint X=-28.2843 Y=41.9157 Z=0
    g35: LineSegment StartX=25.7994 StartY=45.8148 StartZ=0 EndX=28.9914 EndY=42.6228 EndZ=0
    g36: LineSegment StartX=28.9914 StartY=42.6228 StartZ=0 EndX=27.5772 EndY=41.2086 EndZ=0
    g37: LineSegment StartX=27.5772 StartY=41.2086 StartZ=0 EndX=24.3852 EndY=44.4006 EndZ=0
    g38: GeomPoint X=28.2843 Y=41.9157 Z=0
    g39: LineSegment StartX=24.3852 StartY=95.9994 StartZ=0 EndX=27.5772 EndY=99.1914 EndZ=0
    g40: LineSegment StartX=27.5772 StartY=99.1914 StartZ=0 EndX=28.9914 EndY=97.7772 EndZ=0
    g41: LineSegment StartX=28.9914 StartY=97.7772 StartZ=0 EndX=25.7994 EndY=94.5852 EndZ=0
    g42: GeomPoint X=28.2843 Y=98.4843 Z=0
  constraints (113):
    c: Coincident(g0,g1)
    c: Coincident(g1,g2)
    c: Coincident(g2,g3)
    c: Coincident(g3,g0)
    c: Horizontal(g0)
    c: Horizontal(g2)
    c: Vertical(g1)
    c: Vertical(g3)
    c: Symmetric(g0,g0,g-1)
    c: DistanceY(g0,g1) = 140.4
    c: DistanceX(g1,g2) = 94.6
    c: PointOnObject(g4,g0)
    c: Vertical(g4)
    c: Symmetric(g1,g2,g4)
    c: PointOnObject(g5,g3)
    c: Horizontal(g5)
    c: Symmetric(g1,g0,g5)
    c: PointOnObject(g6,g5)
    c: PointOnObject(g6,g4)
    c: Coincident(g7,g6)
    c: Radius(g7) = 35.5
    c: PointOnObject(g8,g2)
    c: PointOnObject(g8,g0)
    c: Vertical(g8)
    c: PointOnObject(g9,g2)
    c: PointOnObject(g9,g0)
    c: Vertical(g9)
    c: PointOnObject(g10,g9)
    c: PointOnObject(g10,g8)
    c: Horizontal(g10)
    c: PointOnObject(g11,g8)
    c: PointOnObject(g11,g9)
    c: Horizontal(g11)
    c: Coincident(g12,g10)
    c: Coincident(g13,g10)
    c: Coincident(g14,g11)
    c: Coincident(g15,g11)
    c: Radius(g12) = 1.5
    c: Equal(g12,g13)
    c: Equal(g12,g15)
    c: Equal(g12,g14)
    c: Coincident(g16,g7)
    c: Radius(g16) = 43
    c: Coincident(g17,g18)
    c: Coincident(g18,g19)
    c: Coincident(g19,g20)
    c: Coincident(g20,g17)
    c: Horizontal(g17)
    c: Horizontal(g19)
    c: Vertical(g18)
    c: Vertical(g20)
    c: PointOnObject(g17,g16)
    c: PointOnObject(g18,g16)
    c: PointOnObject(g17,g16)
    c: Equal(g17,g20)
    c: Coincident(g21,g17)
    c: Coincident(g22,g17)
    c: Coincident(g23,g18)
    c: Coincident(g24,g19)
    c: Radius(g22) = 1
    c: Equal(g22,g21)
    c: Equal(g22,g24)
    c: Equal(g22,g23)
    c: PointOnObject(g21,g8)
    c: PointOnObject(g22,g9)
    c: DistanceY(g12,g8) = 10
    c: DistanceY(g8,g14) = 10
    c: PointOnObject(g25,g7)
    c: Coincident(g26,g25)
    c: Coincident(g27,g26)
    c: PointOnObject(g27,g7)
    c: Perpendicular(g25,g26)
    c: Coincident(g28,g21)
    c: Coincident(g28,g23)
    c: Coincident(g29,g22)
    c: Coincident(g29,g24)
    c: Parallel(g28,g27)
    c: Parallel(g27,g25)
    c: Symmetric(g25,g26,g30)
    c: PointOnObject(g30,g28)
    c: PointOnObject(g31,g7)
    c: Coincident(g32,g31)
    c: Coincident(g33,g32)
    c: PointOnObject(g33,g7)
    c: Parallel(g31,g29)
    c: Parallel(g29,g33)
    c: Equal(g31,g33)
    c: Symmetric(g31,g32,g34)
    c: PointOnObject(g34,g29)
    c: PointOnObject(g35,g7)
    c: Coincident(g36,g35)
    c: Coincident(g37,g36)
    c: PointOnObject(g37,g7)
    c: Symmetric(g35,g36,g38)
    c: Equal(g37,g35)
    c: Parallel(g35,g37)
    c: Parallel(g37,g28)
    c: PointOnObject(g39,g7)
    c: Coincident(g40,g39)
    c: Coincident(g41,g40)
    c: PointOnObject(g41,g7)
    c: Parallel(g41,g39)
    c: Parallel(g39,g29)
    c: Equal(g39,g41)
    c: Symmetric(g39,g40,g42)
    c: Distance(g26,g25) = 2
    c: Equal(g40,g26)
    c: Equal(g26,g32)
    c: Equal(g32,g36)
    c: Symmetric(g30,g38,g29)
    c: Symmetric(g34,g42,g28)
    c: Distance(g21,g30) = 3
    c: Equal(g25,g41)
FEATURE [PartDesign::Body] Body010  label="piezo-carrier"
  Group = -> [Sketch073]
  Origin = -> Origin011
  Placement = pos=(-236.425,-991.345,0) rot=(0,0,1;0rad)
FEATURE [Part::Part2DObjectPython] Clone2D015  label="sc_piezo_1"  # Draft 2D object (typed FeaturePython)
  Fuse = false
  Objects = -> [Sketch073]
  Placement = pos=(87,-1381.86,0) rot=(0,0,1;0rad)
  Scale = (1,1,1)
  expr: .Placement.Base.y = -1235.81 - 146.05
FEATURE [Part::Part2DObjectPython] Clone2D016  label="sc_piezo_2"  # Draft 2D object (typed FeaturePython)
  Fuse = false
  Objects = -> [Clone2D015]
  Placement = pos=(87,-1527.91,0) rot=(0,0,1;0rad)
  Scale = (1,1,1)
  expr: .Placement.Base.y = -1381.86 - 140 - 6.05
FEATURE [Part::Feature] path2
  shape: bbox 22.55 x 26.33 x 2e-07 mm, 0 faces, 0 solids (baked)
FEATURE [Part::Feature] path2001
  shape: bbox 37.01 x 76.81 x 2e-07 mm, 0 faces, 0 solids (baked)
FEATURE [Part::Feature] path4
  shape: bbox 12.92 x 13.07 x 2e-07 mm, 0 faces, 0 solids (baked)
FEATURE [Part::Feature] path8
  shape: bbox 12.92 x 13.07 x 2e-07 mm, 0 faces, 0 solids (baked)
FEATURE [App::LinkGroup] LinkGroup  label="Logo_76"
  ElementList = -> [path2,path2001,path4,path8]
  LinkMode = 0
  Placement = pos=(751.623,-1360.18,0) rot=(0,0,1;0rad)
FEATURE [Part::Mirroring] mirror  label="nutzen001 (mirrored)"
  Base = (-9.56418,-1386.81,-0.000190735)
  Normal = (-1,0,-1.19209e-07)
  Placement = pos=(-444.939,-1056.68,0) rot=(0,0,1;1.5708rad)
  Source = -> Clone2D012
FEATURE [Part::Mirroring] mirror001  label="top_xy (2D) (mirrored)"
  Base = (-9.56418,-1150.28,0)
  Normal = (-1,0,0)
  Placement = pos=(-444.939,-1056.68,0) rot=(0,0,1;1.5708rad)
  Source = -> Clone2D
FEATURE [PartDesign::FeatureBase] BaseFeature  label="nutzen_carriers"
  BaseFeature = -> mirror
FEATURE [App::Part] Part004  label="Job01"
  Group = -> [BaseFeature,Body009]
  Origin = -> Origin016
FEATURE [Sketcher::SketchObject] Sketch074  label="outer_3D"
  FullyConstrained = true
  MapMode = 5
  Placement = pos=(0,0,0) rot=(1,0,0;1.5708rad)
  Support = -> [XZ_Plane018]
  expr: Constraints[9] = <<Dimensions>>.shell_outer_rad
  expr: Constraints[14] = <<Dimensions>>.shellfix_thick
  expr: Constraints[7] = <<Dimensions>>.shellfix_thick_min
  sketch-geometry (6):
    g0: ArcOfCircle CenterX=70.4943 CenterY=134.1 CenterZ=0 NormalX=0 NormalY=0 NormalZ=1 AngleXU=0 Radius=151.5 StartAngle=4.22841 EndAngle=5.19637
    g1: LineSegment StartX=70.4943 StartY=-19.4 StartZ=0 EndX=70.4943 EndY=134.1 EndZ=0
    g2: LineSegment StartX=140.989 StartY=-19.4 StartZ=0 EndX=140.989 EndY=0 EndZ=0
    g3: LineSegment StartX=-4.26e-14 StartY=-19.4 StartZ=0 EndX=-4.26e-14 EndY=0 EndZ=0
    g4: GeomPoint X=70.4943 Y=-17.4 Z=0
    g5: LineSegment StartX=-4.26e-14 StartY=-19.4 StartZ=0 EndX=140.989 EndY=-19.4 EndZ=0
  constraints (16):
    c: Coincident(g1,g0)
    c: Vertical(g1)
    c: Coincident(g3,g0)
    c: Vertical(g3)
    c: Coincident(g0,g2)
    c: PointOnObject(g4,g0)
    c: PointOnObject(g4,g1)
    c: DistanceY(g1,g4) = 2
    c: Vertical(g2)
    c: Radius(g0) = 151.5
    c: Equal(g3,g2)
    c: Coincident(g5,g3)
    c: Coincident(g5,g2)
    c: Symmetric(g2,g3,g1)
    c: DistanceY(g3,g0) = 19.4
    c: Coincident(g0,g-1)
FEATURE [Sketcher::SketchObject] Sketch075  label="inner_3d"
  FullyConstrained = true
  MapMode = 5
  Placement = pos=(0,0,0) rot=(1,0,0;1.5708rad)
  Support = -> [XZ_Plane019]
  expr: Constraints[11] = <<Dimensions>>.shell_outer_rad - <<Dimensions>>.shell_thick
  expr: Constraints[15] = <<Dimensions>>.shellfix_thick
  expr: Constraints[10] = <<Dimensions>>.shellfix_thick_min
  sketch-geometry (6):
    g0: LineSegment StartX=2.84e-14 StartY=0 StartZ=0 EndX=137.894 EndY=0 EndZ=0
    g1: LineSegment StartX=137.894 StartY=0 StartZ=0 EndX=137.894 EndY=2 EndZ=0
    g2: LineSegment StartX=2.84e-14 StartY=0 StartZ=0 EndX=2.84e-14 EndY=2 EndZ=0
    g3: ArcOfCircle CenterX=68.9469 CenterY=-125.9 CenterZ=0 NormalX=0 NormalY=0 NormalZ=1 AngleXU=0 Radius=145.3 StartAngle=1.07638 EndAngle=2.06521
    g4: LineSegment StartX=68.9469 StartY=0 StartZ=0 EndX=68.9469 EndY=-125.9 EndZ=0
    g5: LineSegment StartX=68.9469 StartY=0 StartZ=0 EndX=68.9469 EndY=19.4 EndZ=0
  constraints (17):
    c: Horizontal(g0)
    c: Coincident(g1,g0)
    c: Vertical(g1)
    c: Coincident(g2,g0)
    c: Vertical(g2)
    c: Coincident(g4,g3)
    c: Vertical(g4)
    c: Symmetric(g0,g0,g4)
    c: Coincident(g3,g2)
    c: Coincident(g3,g1)
    c: DistanceY(g0,g1) = 2
    c: Radius(g3) = 145.3
    c: Vertical(g5)
    c: PointOnObject(g5,g3)
    c: Symmetric(g0,g0,g5)
    c: DistanceY(g4,g5) = 19.4
    c: Coincident(g0,g-1)
FEATURE [PartDesign::Pad] Pad013  label="outer_3D001"
  Direction = (1,1,1)
  Length = 150
  Length2 = 100
  Placement = pos=(0,0,0) rot=(1,0,0;1.5708rad)
  Profile = -> Sketch074
  Type = 0
  expr: Length = <<Dimensions>>.shell_hei + 2
FEATURE [Sketcher::SketchObject] Sketch076  label="outer_2D"
  ExternalGeometry = -> [Pad013]
  FullyConstrained = true
  MapMode = 5
  Support = -> [XY_Plane018]
  expr: Constraints[30] = <<Dimensions>>.shellfix_wid
  expr: Constraints[8] = <<Dimensions>>.shellfix_len
  expr: Constraints[23] = <<wasteplate_BL_0607>>#<<Dimensions>>.hammernut_sink_rad
  expr: Constraints[24] = wasteplate_BL_0607#<<Dimensions>>.hammernut_rad
  expr: Constraints[27] = <<wasteplate_BL_0607>>#<<Dimensions>>.hammernut_sink_rad * 2
  sketch-geometry (14):
    g0: LineSegment StartX=-91.5057 StartY=37 StartZ=0 EndX=232.494 EndY=37 EndZ=0
    g1: LineSegment StartX=232.494 StartY=37 StartZ=0 EndX=232.494 EndY=-187 EndZ=0
    g2: LineSegment StartX=232.494 StartY=-187 StartZ=0 EndX=-91.5057 EndY=-187 EndZ=0
    g3: LineSegment StartX=-91.5057 StartY=-187 StartZ=0 EndX=-91.5057 EndY=37 EndZ=0
    g4: LineSegment StartX=0 StartY=0 StartZ=0 EndX=140.989 EndY=-150 EndZ=0
    g5: GeomPoint X=70.4943 Y=-75 Z=0
    g6: Circle CenterX=70.4943 CenterY=19.8 CenterZ=0 NormalX=0 NormalY=0 NormalZ=1 AngleXU=0 Radius=8.6
    g7: Circle CenterX=70.4943 CenterY=-169.8 CenterZ=0 NormalX=0 NormalY=0 NormalZ=1 AngleXU=0 Radius=8.6
    g8: Circle CenterX=70.4943 CenterY=-169.8 CenterZ=0 NormalX=0 NormalY=0 NormalZ=1 AngleXU=0 Radius=3.1
    g9: Circle CenterX=70.4943 CenterY=19.8 CenterZ=0 NormalX=0 NormalY=0 NormalZ=1 AngleXU=0 Radius=3.1
    g10: LineSegment StartX=232.494 StartY=19.8 StartZ=0 EndX=-91.5057 EndY=19.8 EndZ=0
    g11: LineSegment StartX=-91.5057 StartY=-169.8 StartZ=0 EndX=232.494 EndY=-169.8 EndZ=0
    g12: GeomPoint X=-91.5057 Y=-75 Z=0
    g13: Circle CenterX=0 CenterY=-150 CenterZ=0 NormalX=0 NormalY=0 NormalZ=1 AngleXU=0 Radius=3
  constraints (32):
    c: Coincident(g0,g1)
    c: Coincident(g1,g2)
    c: Coincident(g2,g3)
    c: Coincident(g3,g0)
    c: Horizontal(g0)
    c: Horizontal(g2)
    c: Vertical(g1)
    c: Vertical(g3)
    c: DistanceY(g2,g0) = 224
    c: Coincident(g4,g-1)
    c: Coincident(g4,g-4)
    c: Symmetric(g-1,g4,g5)
    c: Symmetric(g0,g2,g5)
    c: Coincident(g8,g7)
    c: Coincident(g9,g6)
    c: PointOnObject(g10,g1)
    c: Horizontal(g10)
    c: PointOnObject(g11,g1)
    c: Horizontal(g11)
    c: Symmetric(g10,g10,g6)
    c: Symmetric(g0,g2,g12)
    c: Symmetric(g10,g11,g12)
    c: PointOnObject(g10,g3)
    c: Radius(g6) = 8.6
    c: Radius(g9) = 3.1
    c: Equal(g7,g6)
    c: Equal(g8,g9)
    c: DistanceY(g10,g0) = 17.2
    c: Coincident(g13,g-4)
    c: Radius(g13) = 3
    c: DistanceX(g0,g0) = 324
    c: Symmetric(g11,g11,g7)
FEATURE [PartDesign::Body] Body011  label="fixture_shell_outer"
  Group = -> [Sketch074,Pad013,Sketch076]
  Origin = -> Origin018
  Tip = -> Pad013
FEATURE [PartDesign::Pad] Pad014  label="inner_3D"
  Direction = (1,1,1)
  Length = 150
  Length2 = 100
  Placement = pos=(0,0,0) rot=(1,0,0;1.5708rad)
  Profile = -> Sketch075
  Type = 0
  expr: Length = <<Dimensions>>.shell_hei + 2
FEATURE [Sketcher::SketchObject] Sketch077  label="inner_2D"
  ExternalGeometry = -> [Pad014]
  FullyConstrained = true
  MapMode = 5
  Support = -> [XY_Plane019]
  expr: Constraints[3] = <<Dimensions>>.shellfix_len
  expr: Constraints[7] = wasteplate_BL_0607#<<Dimensions>>.hammernut_rad
  expr: Constraints[11] = <<wasteplate_BL_0607>>#<<Dimensions>>.hammernut_sink_rad * 2
  sketch-geometry (22):
    g0: LineSegment StartX=-11.0531 StartY=37 StartZ=0 EndX=148.947 EndY=37 EndZ=0
    g1: LineSegment StartX=148.947 StartY=-187 StartZ=0 EndX=-11.0531 EndY=-187 EndZ=0
    g2: GeomPoint X=68.9469 Y=-75 Z=0
    g3: LineSegment StartX=-11.0531 StartY=19.8 StartZ=0 EndX=148.947 EndY=19.8 EndZ=0
    g4: LineSegment StartX=-11.0531 StartY=-169.8 StartZ=0 EndX=148.947 EndY=-169.8 EndZ=0
    g5: Circle CenterX=68.9469 CenterY=19.8 CenterZ=0 NormalX=0 NormalY=0 NormalZ=1 AngleXU=0 Radius=3.1
    g6: Circle CenterX=68.9469 CenterY=-169.8 CenterZ=0 NormalX=0 NormalY=0 NormalZ=1 AngleXU=0 Radius=3.1
    g7: GeomPoint X=-11.0531 Y=-75 Z=0
    g8: Circle CenterX=0 CenterY=-150 CenterZ=0 NormalX=0 NormalY=0 NormalZ=1 AngleXU=0 Radius=3
    g9: GeomPoint X=68.9469 Y=-75 Z=0
    g10: LineSegment StartX=-11.0531 StartY=37 StartZ=0 EndX=-11.0531 EndY=0 EndZ=0
    g11: LineSegment StartX=148.947 StartY=37 StartZ=0 EndX=148.947 EndY=0 EndZ=0
    g12: LineSegment StartX=148.947 StartY=0 StartZ=0 EndX=137.894 EndY=0 EndZ=0
    g13: LineSegment StartX=137.894 StartY=0 StartZ=0 EndX=137.894 EndY=-150 EndZ=0
    g14: LineSegment StartX=137.894 StartY=-150 StartZ=0 EndX=148.947 EndY=-150 EndZ=0
    g15: LineSegment StartX=148.947 StartY=-150 StartZ=0 EndX=148.947 EndY=-187 EndZ=0
    g16: LineSegment StartX=-11.0531 StartY=0 StartZ=0 EndX=0 EndY=0 EndZ=0
    g17: LineSegment StartX=0 StartY=0 StartZ=0 EndX=0 EndY=-150 EndZ=0
    g18: LineSegment StartX=0 StartY=-150 StartZ=0 EndX=-11.0531 EndY=-150 EndZ=0
    g19: LineSegment StartX=-11.0531 StartY=-150 StartZ=0 EndX=-11.0531 EndY=-187 EndZ=0
    g20: LineSegment StartX=0 StartY=0 StartZ=0 EndX=137.894 EndY=0 EndZ=0
    g21: LineSegment StartX=0 StartY=-150 StartZ=0 EndX=137.894 EndY=-150 EndZ=0
  constraints (54):
    c: Horizontal(g0)
    c: Horizontal(g1)
    c: Symmetric(g-3,g-4,g2)
    c: DistanceY(g1,g0) = 224
    c: Horizontal(g3)
    c: Horizontal(g4)
    c: Equal(g5,g6)
    c: Radius(g5) = 3.1
    c: Symmetric(g3,g3,g5)
    c: Symmetric(g4,g4,g6)
    c: Symmetric(g3,g4,g7)
    c: DistanceY(g3,g0) = 17.2
    c: Coincident(g8,g-4)
    c: Radius(g8) = 3
    c: DistanceX(g0,g0) = 160
    c: Symmetric(g1,g0,g7)
    c: Symmetric(g0,g1,g9)
    c: Coincident(g10,g0)
    c: Vertical(g10)
    c: Coincident(g11,g0)
    c: Vertical(g11)
    c: Coincident(g12,g11)
    c: Coincident(g13,g12)
    c: Vertical(g13)
    c: Coincident(g14,g13)
    c: Coincident(g15,g14)
    c: Coincident(g15,g1)
    c: Vertical(g15)
    c: Coincident(g16,g10)
    c: Coincident(g17,g16)
    c: Coincident(g18,g17)
    c: Coincident(g19,g18)
    c: Coincident(g19,g1)
    c: Vertical(g19)
    c: Vertical(g17)
    c: Horizontal(g12)
    c: Equal(g16,g12)
    c: Equal(g12,g14)
    c: Equal(g14,g18)
    c: Equal(g17,g13)
    c: Horizontal(g14)
    c: Horizontal(g18)
    c: Horizontal(g16)
    c: PointOnObject(g3,g11)
    c: PointOnObject(g4,g15)
    c: Equal(g10,g11)
    c: Equal(g11,g15)
    c: Symmetric(g-4,g-1,g9)
    c: PointOnObject(g3,g10)
    c: Coincident(g16,g-1)
    c: Coincident(g20,g16)
    c: Coincident(g20,g12)
    c: Coincident(g21,g8)
    c: Coincident(g21,g13)
FEATURE [PartDesign::Body] Body012  label="fixture_shell_inner"
  Group = -> [Sketch075,Pad014,Sketch077]
  Origin = -> Origin019
  Tip = -> Pad014
FEATURE [Sketcher::SketchObject] Sketch080
  ExternalGeometry = -> [Sketch036]
  FullyConstrained = true
  MapMode = 2
  Support = -> [Pad004]
  sketch-geometry (1):
    g0: Circle CenterX=0 CenterY=100 CenterZ=0 NormalX=0 NormalY=0 NormalZ=1 AngleXU=0 Radius=37.95
  constraints (2):
    c: Equal(g0,g-3)
    c: Coincident(g0,g-3)
FEATURE [PartDesign::Pad] Pad016
  BaseFeature = -> Pad004
  Direction = (1,1,1)
  Length = 11.8
  Length2 = 100
  Profile = -> Sketch080
  Type = 0
  expr: Length = <<Dimensions>>.base_thick
FEATURE [Sketcher::SketchObject] Sketch081
  ExternalGeometry = -> [Sketch036]
  FullyConstrained = true
  MapMode = 5
  Placement = pos=(0,0,11.8) rot=(0,0,1;0rad)
  Support = -> [Pad016]
  sketch-geometry (5):
    g0: Circle CenterX=-16.1884 CenterY=123.395 CenterZ=0 NormalX=0 NormalY=0 NormalZ=1 AngleXU=0 Radius=5.5
    g1: Circle CenterX=-25.4304 CenterY=110.334 CenterZ=0 NormalX=0 NormalY=0 NormalZ=1 AngleXU=0 Radius=6.5
    g2: Circle CenterX=-23.9501 CenterY=91.3921 CenterZ=0 NormalX=0 NormalY=0 NormalZ=1 AngleXU=0 Radius=8.5
    g3: Circle CenterX=0 CenterY=80.05 CenterZ=0 NormalX=0 NormalY=0 NormalZ=1 AngleXU=0 Radius=14
    g4: Circle CenterX=14.2446 CenterY=110.922 CenterZ=0 NormalX=0 NormalY=0 NormalZ=1 AngleXU=0 Radius=16
  constraints (10):
    c: Coincident(g0,g-3)
    c: Coincident(g1,g-4)
    c: Coincident(g2,g-5)
    c: Coincident(g3,g-7)
    c: Coincident(g4,g-6)
    c: Equal(g4,g-6)
    c: Equal(g3,g-7)
    c: Equal(g2,g-5)
    c: Equal(g1,g-4)
    c: Equal(g0,g-3)
FEATURE [PartDesign::Pocket] Pocket007
  BaseFeature = -> Pad016
  Length = 8
  Length2 = 100
  Profile = -> Sketch081
  Type = 0
  expr: Length = <<Dimensions>>.bevel_thick
FEATURE [Sketcher::SketchObject] Sketch082
  ExternalGeometry = -> [Sketch036]
  FullyConstrained = true
  MapMode = 5
  Placement = pos=(0,0,11.8) rot=(0,0,1;0rad)
  Support = -> [Pocket007]
  sketch-geometry (10):
    g0: Circle CenterX=-38 CenterY=138 CenterZ=0 NormalX=0 NormalY=0 NormalZ=1 AngleXU=0 Radius=1.5
    g1: Circle CenterX=38 CenterY=138 CenterZ=0 NormalX=0 NormalY=0 NormalZ=1 AngleXU=0 Radius=1.5
    g2: Circle CenterX=14.2446 CenterY=110.922 CenterZ=0 NormalX=0 NormalY=0 NormalZ=1 AngleXU=0 Radius=4
    g3: Circle CenterX=3.04459 CenterY=110.922 CenterZ=0 NormalX=0 NormalY=0 NormalZ=1 AngleXU=0 Radius=2.4
    g4: Circle CenterX=-16.1884 CenterY=123.395 CenterZ=0 NormalX=0 NormalY=0 NormalZ=1 AngleXU=0 Radius=3
    g5: Circle CenterX=-25.4304 CenterY=110.334 CenterZ=0 NormalX=0 NormalY=0 NormalZ=1 AngleXU=0 Radius=4
    g6: Circle CenterX=-23.9501 CenterY=91.3921 CenterZ=0 NormalX=0 NormalY=0 NormalZ=1 AngleXU=0 Radius=6
    g7: Circle CenterX=0 CenterY=80.05 CenterZ=0 NormalX=0 NormalY=0 NormalZ=1 AngleXU=0 Radius=5
    g8: Circle CenterX=-38 CenterY=10 CenterZ=0 NormalX=0 NormalY=0 NormalZ=1 AngleXU=0 Radius=1.5
    g9: Circle CenterX=38 CenterY=10 CenterZ=0 NormalX=0 NormalY=0 NormalZ=1 AngleXU=0 Radius=1.5
  constraints (20):
    c: Coincident(g0,g-3)
    c: Coincident(g1,g-4)
    c: Coincident(g2,g-6)
    c: Coincident(g3,g-5)
    c: Coincident(g4,g-7)
    c: Coincident(g5,g-8)
    c: Coincident(g6,g-9)
    c: Coincident(g7,g-10)
    c: Coincident(g8,g-11)
    c: Coincident(g9,g-12)
    c: Equal(g8,g-11)
    c: Equal(g9,g-12)
    c: Equal(g-10,g7)
    c: Equal(g-9,g6)
    c: Equal(g-5,g3)
    c: Equal(g-6,g2)
    c: Equal(g-8,g5)
    c: Equal(g4,g-7)
    c: Equal(g-3,g0)
    c: Equal(g-4,g1)
FEATURE [PartDesign::Pocket] Pocket008
  BaseFeature = -> Pocket007
  Length = 5
  Length2 = 100
  Profile = -> Sketch082
  Type = 1
FEATURE [PartDesign::FeatureBase] Clone
  BaseFeature = -> Pocket008
FEATURE [PartDesign::Body] Body014  label="part_ampcarrier"
  BaseFeature = -> Pocket008
  Group = -> [Clone]
  Origin = -> Origin021
  Placement = pos=(422.549,-614.683,-254.092) rot=(0,0,1;0rad)
  Tip = -> Clone
FEATURE [App::Part] Part002  label="3D"
  Group = -> [Clone001,Clone002,Clone003,Clone004,Clone005,Body014]
  Origin = -> Origin013
FEATURE [Part::FeaturePython] Clone006  label="top_xy (2D) (mirrored)001"  # Draft clone (typed FeaturePython)
  AttacherType = Attacher::AttachEngine3D
  Fuse = false
  Objects = -> [mirror001]
  Placement = pos=(-444.939,-1056.68,0) rot=(0,0,1;1.5708rad)
  Scale = (1,1,1)
FEATURE [Part::FeaturePython] Clone007  label="nutzen001 (mirrored)001"  # Draft clone (typed FeaturePython)
  AttacherType = Attacher::AttachEngine3D
  Fuse = false
  Objects = -> [mirror]
  Placement = pos=(-444.939,-1056.68,0) rot=(0,0,1;1.5708rad)
  Scale = (1,1,1)
FEATURE [App::Part] Part005  label="Job03"
  Group = -> [path2001,path4,path8,path2,LinkGroup,Clone006,Clone007]
  Origin = -> Origin017
FEATURE [Sketcher::SketchObject] Sketch083  label="grille"
  ExternalGeometry = -> [Sketch009]
  FullyConstrained = false
  MapMode = 5
  Support = -> [XY_Plane002]
  sketch-geometry (45):
    g0: LineSegment StartX=-89.7 StartY=48.5583 StartZ=0 EndX=-89.7 EndY=-48.5583 EndZ=0
    g1: LineSegment StartX=-80.7 StartY=62.382 StartZ=0 EndX=-80.7 EndY=-62.382 EndZ=0
    g2: LineSegment StartX=-89.7 StartY=48.5583 StartZ=0 EndX=-80.7 EndY=62.382 EndZ=0
    g3: LineSegment StartX=-89.7 StartY=-48.5583 StartZ=0 EndX=-80.7 EndY=-62.382 EndZ=0
    g4: LineSegment StartX=-89.7 StartY=0 StartZ=0 EndX=-102 EndY=0 EndZ=0
    g5: LineSegment StartX=-68.4 StartY=75.6666 StartZ=0 EndX=-68.4 EndY=-75.6666 EndZ=0
    g6: LineSegment StartX=-59.4 StartY=82.9195 StartZ=0 EndX=-59.4 EndY=-82.9195 EndZ=0
    g7: LineSegment StartX=-68.4 StartY=75.6666 StartZ=0 EndX=-59.4 EndY=82.9195 EndZ=0
    g8: LineSegment StartX=-68.4 StartY=-75.6666 StartZ=0 EndX=-59.4 EndY=-82.9195 EndZ=0
    g9: LineSegment StartX=-68.4 StartY=656832 StartZ=0 EndX=-80.7 EndY=656832 EndZ=0
    g10: LineSegment StartX=-47.1 StartY=90.4743 StartZ=0 EndX=-47.1 EndY=-90.4743 EndZ=0
    g11: LineSegment StartX=-38.1 StartY=94.6171 StartZ=0 EndX=-38.1 EndY=-94.6171 EndZ=0
    g12: LineSegment StartX=-47.1 StartY=90.4743 StartZ=0 EndX=-38.1 EndY=94.6171 EndZ=0
    g13: LineSegment StartX=-47.1 StartY=-90.4743 StartZ=0 EndX=-38.1 EndY=-94.6171 EndZ=0
    g14: LineSegment StartX=-47.1 StartY=656838 StartZ=0 EndX=-59.4 EndY=656838 EndZ=0
    g15: LineSegment StartX=-25.8 StartY=98.6831 StartZ=0 EndX=-25.8 EndY=-98.6831 EndZ=0
    g16: LineSegment StartX=-16.8 StartY=100.607 StartZ=0 EndX=-16.8 EndY=-100.607 EndZ=0
    g17: LineSegment StartX=-25.8 StartY=98.6831 StartZ=0 EndX=-16.8 EndY=100.607 EndZ=0
    g18: LineSegment StartX=-25.8 StartY=-98.6831 StartZ=0 EndX=-16.8 EndY=-100.607 EndZ=0
    g19: LineSegment StartX=-25.8 StartY=656809 StartZ=0 EndX=-38.1 EndY=656809 EndZ=0
    g20: LineSegment StartX=-4.5 StartY=101.901 StartZ=0 EndX=-4.5 EndY=-101.901 EndZ=0
    g21: LineSegment StartX=4.5 StartY=101.901 StartZ=0 EndX=4.5 EndY=-101.901 EndZ=0
    g22: LineSegment StartX=-4.5 StartY=101.901 StartZ=0 EndX=4.5 EndY=101.901 EndZ=0
    g23: LineSegment StartX=-4.5 StartY=-101.901 StartZ=0 EndX=4.5 EndY=-101.901 EndZ=0
    g24: LineSegment StartX=-4.5 StartY=656802 StartZ=0 EndX=-16.8 EndY=656802 EndZ=0
    g25: LineSegment StartX=16.8 StartY=100.607 StartZ=0 EndX=16.8 EndY=-100.607 EndZ=0
    g26: LineSegment StartX=25.8 StartY=98.6831 StartZ=0 EndX=25.8 EndY=-98.6831 EndZ=0
    g27: LineSegment StartX=16.8 StartY=100.607 StartZ=0 EndX=25.8 EndY=98.6831 EndZ=0
    g28: LineSegment StartX=16.8 StartY=-100.607 StartZ=0 EndX=25.8 EndY=-98.6831 EndZ=0
    g29: LineSegment StartX=16.8 StartY=656795 StartZ=0 EndX=4.5 EndY=656795 EndZ=0
    g30: LineSegment StartX=38.1 StartY=94.6171 StartZ=0 EndX=38.1 EndY=-94.6171 EndZ=0
    g31: LineSegment StartX=47.1 StartY=90.4743 StartZ=0 EndX=47.1 EndY=-90.4743 EndZ=0
    g32: LineSegment StartX=38.1 StartY=94.6171 StartZ=0 EndX=47.1 EndY=90.4743 EndZ=0
    g33: LineSegment StartX=38.1 StartY=-94.6171 StartZ=0 EndX=47.1 EndY=-90.4743 EndZ=0
    g34: LineSegment StartX=38.1 StartY=656788 StartZ=0 EndX=25.8 EndY=656788 EndZ=0
    g35: LineSegment StartX=59.4 StartY=82.9195 StartZ=0 EndX=59.4 EndY=-82.9195 EndZ=0
    g36: LineSegment StartX=68.4 StartY=75.6666 StartZ=0 EndX=68.4 EndY=-75.6666 EndZ=0
    g37: LineSegment StartX=59.4 StartY=82.9195 StartZ=0 EndX=68.4 EndY=75.6666 EndZ=0
    g38: LineSegment StartX=59.4 StartY=-82.9195 StartZ=0 EndX=68.4 EndY=-75.6666 EndZ=0
    g39: LineSegment StartX=59.4 StartY=404035 StartZ=0 EndX=47.1 EndY=404035 EndZ=0
    g40: LineSegment StartX=80.7 StartY=62.382 StartZ=0 EndX=80.7 EndY=-62.382 EndZ=0
    g41: LineSegment StartX=89.7 StartY=48.5583 StartZ=0 EndX=89.7 EndY=-48.5583 EndZ=0
    g42: LineSegment StartX=80.7 StartY=62.382 StartZ=0 EndX=89.7 EndY=48.5583 EndZ=0
    g43: LineSegment StartX=80.7 StartY=-62.382 StartZ=0 EndX=89.7 EndY=-48.5583 EndZ=0
    g44: LineSegment StartX=80.7 StartY=404026 StartZ=0 EndX=68.4 EndY=404026 EndZ=0
  constraints (136):
    c: PointOnObject(g0,g-3)
    c: PointOnObject(g0,g-3)
    c: Vertical(g0)
    c: PointOnObject(g1,g-3)
    c: PointOnObject(g1,g-3)
    c: Vertical(g1)
    c: DistanceX(g0,g1) = 9
    c: Coincident(g2,g0)
    c: Coincident(g2,g1)
    c: Coincident(g3,g0)
    c: Coincident(g3,g1)
    c: PointOnObject(g4,g0)
    c: Horizontal(g4)
    c: Perpendicular(g-3,g4)
    c: DistanceX(g4,g4) = 12.3
    c: PointOnObject(g4,g-3)
    c: Vertical(g5)
    c: Vertical(g6)
    c: DistanceX(g5,g6) = 9
    c: Coincident(g7,g5)
    c: Coincident(g7,g6)
    c: Coincident(g8,g5)
    c: Coincident(g8,g6)
    c: PointOnObject(g9,g5)
    c: Horizontal(g9)
    c: Equal(g4,g9) = 9
    c: Vertical(g10)
    c: Vertical(g11)
    c: DistanceX(g10,g11) = 9
    c: Coincident(g12,g10)
    c: Coincident(g12,g11)
    c: Coincident(g13,g10)
    c: Coincident(g13,g11)
    c: PointOnObject(g14,g10)
    c: Horizontal(g14)
    c: Equal(g4,g14) = 9
    c: Vertical(g15)
    c: Vertical(g16)
    c: DistanceX(g15,g16) = 9
    c: Coincident(g17,g15)
    c: Coincident(g17,g16)
    c: Coincident(g18,g15)
    c: Coincident(g18,g16)
    c: PointOnObject(g19,g15)
    c: Horizontal(g19)
    c: Equal(g4,g19) = 9
    c: Vertical(g20)
    c: Vertical(g21)
    c: DistanceX(g20,g21) = 9
    c: Coincident(g22,g20)
    c: Coincident(g22,g21)
    c: Coincident(g23,g20)
    c: Coincident(g23,g21)
    c: PointOnObject(g24,g20)
    c: Horizontal(g24)
    c: Equal(g4,g24) = 9
    c: Vertical(g25)
    c: Vertical(g26)
    c: DistanceX(g25,g26) = 9
    c: Coincident(g27,g25)
    c: Coincident(g27,g26)
    c: Coincident(g28,g25)
    c: Coincident(g28,g26)
    c: PointOnObject(g29,g25)
    c: Horizontal(g29)
    c: Equal(g4,g29) = 9
    c: Vertical(g30)
    c: Vertical(g31)
    c: DistanceX(g30,g31) = 9
    c: Coincident(g32,g30)
    c: Coincident(g32,g31)
    c: Coincident(g33,g30)
    c: Coincident(g33,g31)
    c: PointOnObject(g34,g30)
    c: Horizontal(g34)
    c: Equal(g4,g34) = 9
    c: Vertical(g35)
    c: Vertical(g36)
    c: DistanceX(g35,g36) = 9
    c: Coincident(g37,g35)
    c: Coincident(g37,g36)
    c: Coincident(g38,g35)
    c: Coincident(g38,g36)
    c: PointOnObject(g39,g35)
    c: Horizontal(g39)
    c: Equal(g4,g39) = 9
    c: Vertical(g40)
    c: Vertical(g41)
    c: DistanceX(g40,g41) = 9
    c: Coincident(g42,g40)
    c: Coincident(g42,g41)
    c: Coincident(g43,g40)
    c: Coincident(g43,g41)
    c: PointOnObject(g44,g40)
    c: Horizontal(g44)
    c: Equal(g4,g44) = 9
    c: PointOnObject(g9,g1)
    c: PointOnObject(g5,g-3)
    c: PointOnObject(g6,g-3)
    c: PointOnObject(g5,g-3)
    c: PointOnObject(g6,g-3)
    c: PointOnObject(g10,g-3)
    c: PointOnObject(g11,g-3)
    c: PointOnObject(g14,g6)
    c: PointOnObject(g10,g-3)
    c: PointOnObject(g11,g-3)
    c: PointOnObject(g19,g11)
    c: PointOnObject(g24,g16)
    c: PointOnObject(g29,g21)
    c: PointOnObject(g34,g26)
    c: PointOnObject(g39,g31)
    c: PointOnObject(g44,g36)
    c: PointOnObject(g15,g-3)
    c: PointOnObject(g15,g-3)
    c: PointOnObject(g16,g-3)
    c: PointOnObject(g20,g-3)
    c: PointOnObject(g21,g-3)
    c: PointOnObject(g20,g-3)
    c: PointOnObject(g21,g-3)
    c: PointOnObject(g25,g-3)
    c: PointOnObject(g26,g-3)
    c: PointOnObject(g31,g-3)
    c: PointOnObject(g36,g-3)
    c: PointOnObject(g40,g-3)
    c: PointOnObject(g41,g-3)
    c: PointOnObject(g35,g-3)
    c: PointOnObject(g30,g-3)
    c: PointOnObject(g16,g-3)
    c: PointOnObject(g25,g-3)
    c: PointOnObject(g26,g-3)
    c: PointOnObject(g30,g-3)
    c: PointOnObject(g31,g-3)
    c: PointOnObject(g35,g-3)
    c: PointOnObject(g36,g-3)
    c: PointOnObject(g40,g-3)
    c: PointOnObject(g41,g-3)
FEATURE [PartDesign::Body] Body001  label="bottom"
  Group = -> [Sketch009,Sketch005,Sketch011,Sketch045,Pad006,Sketch046,Pad007,Sketch047,Pocket003,Sketch048,Pocket004,Sketch083]
  Origin = -> Origin002
  Placement = pos=(0,-332.88,0) rot=(0,0,1;0rad)
  Tip = -> Pocket004
FEATURE [Part::Part2DObjectPython] Clone2D017  label="grille (2D)"  # Draft 2D object (typed FeaturePython)
  Fuse = false
  Objects = -> [Sketch083]
  Placement = pos=(450,-1535,0) rot=(0,0,1;0rad)
  Scale = (1,1,1)
FEATURE [Sketcher::SketchObject] Sketch084
  FullyConstrained = true
  MapMode = 5
  Placement = pos=(0,0,0) rot=(1,0,0;1.5708rad)
  Support = -> [XZ_Plane020]
  expr: Constraints[12] = <<Dimensions>>.shellfix_thick_min
  expr: Constraints[13] = <<Dimensions>>.shellfix_thick
  expr: Constraints[14] = <<Dimensions>>.shell_outer_rad
  sketch-geometry (6):
    g0: LineSegment StartX=-70.4943 StartY=0 StartZ=0 EndX=70.4943 EndY=0 EndZ=0
    g1: LineSegment StartX=-70.4943 StartY=0 StartZ=0 EndX=-70.4943 EndY=19.4 EndZ=0
    g2: LineSegment StartX=70.4943 StartY=0 StartZ=0 EndX=70.4943 EndY=19.4 EndZ=0
    g3: ArcOfCircle CenterX=0 CenterY=153.5 CenterZ=0 NormalX=0 NormalY=0 NormalZ=1 AngleXU=0 Radius=151.5 StartAngle=4.22841 EndAngle=5.19637
    g4: LineSegment StartX=0 StartY=0 StartZ=0 EndX=0 EndY=153.5 EndZ=0
    g5: GeomPoint X=0 Y=2 Z=0
  constraints (16):
    c: Horizontal(g0)
    c: Coincident(g1,g0)
    c: Coincident(g2,g0)
    c: Vertical(g2)
    c: Vertical(g1)
    c: Coincident(g3,g1)
    c: Coincident(g3,g2)
    c: Vertical(g4)
    c: Coincident(g4,g3)
    c: Symmetric(g0,g0,g4)
    c: PointOnObject(g5,g4)
    c: PointOnObject(g5,g3)
    c: DistanceY(g4,g5) = 2
    c: DistanceY(g0,g1) = 19.4
    c: Radius(g3) = 151.5
    c: Coincident(g4,g-1)
FEATURE [Sketcher::SketchObject] Sketch078
  ExternalGeometry = -> [Sketch084]
  FullyConstrained = true
  MapMode = 5
  Support = -> [XY_Plane020]
  expr: Constraints[28] = <<wasteplate_BL_0607>>#<<Dimensions>>.sink_rad
  expr: Constraints[22] = wasteplate_BL_0607#<<Dimensions>>.hole_rad
  expr: Constraints[40] = <<Dimensions>>.shellfix_len
  sketch-geometry (22):
    g0: Circle CenterX=1e-16 CenterY=-7.21876 CenterZ=0 NormalX=0 NormalY=0 NormalZ=1 AngleXU=0 Radius=30
    g1: ArcOfCircle CenterX=1e-16 CenterY=-7.21876 CenterZ=0 NormalX=0 NormalY=0 NormalZ=1 AngleXU=0 Radius=80.5 StartAngle=5.32063 EndAngle=10.3873
    g2: LineSegment StartX=-46 StartY=-73.2812 StartZ=0 EndX=46 EndY=-73.2812 EndZ=0
    g3: Circle CenterX=1e-16 CenterY=-7.21876 CenterZ=0 NormalX=0 NormalY=0 NormalZ=1 AngleXU=0 Radius=67.5
    g4: Circle CenterX=67.122 CenterY=-14.3525 CenterZ=0 NormalX=0 NormalY=0 NormalZ=1 AngleXU=0 Radius=3.1
    g5: Circle CenterX=-39.739 CenterY=-61.7812 CenterZ=0 NormalX=0 NormalY=0 NormalZ=1 AngleXU=0 Radius=3.1
    g6: Circle CenterX=-27.383 CenterY=54.4774 CenterZ=0 NormalX=0 NormalY=0 NormalZ=1 AngleXU=0 Radius=3.1
    g7: LineSegment StartX=-27.383 StartY=54.4774 StartZ=0 EndX=-39.739 EndY=-61.7812 EndZ=0
    g8: LineSegment StartX=-39.739 StartY=-61.7812 StartZ=0 EndX=67.122 EndY=-14.3525 EndZ=0
    g9: LineSegment StartX=67.122 StartY=-14.3525 StartZ=0 EndX=-27.383 EndY=54.4774 EndZ=0
    g10: Circle CenterX=67.122 CenterY=-14.3525 CenterZ=0 NormalX=0 NormalY=0 NormalZ=1 AngleXU=0 Radius=8
    g11: Circle CenterX=-27.383 CenterY=54.4774 CenterZ=0 NormalX=0 NormalY=0 NormalZ=1 AngleXU=0 Radius=8
    g12: Circle CenterX=-39.739 CenterY=-61.7812 CenterZ=0 NormalX=0 NormalY=0 NormalZ=1 AngleXU=0 Radius=8
    g13: LineSegment StartX=-112 StartY=78 StartZ=0 EndX=112 EndY=78 EndZ=0
    g14: LineSegment StartX=112 StartY=78 StartZ=0 EndX=112 EndY=-78 EndZ=0
    g15: LineSegment StartX=112 StartY=-78 StartZ=0 EndX=-112 EndY=-78 EndZ=0
    g16: LineSegment StartX=-112 StartY=-78 StartZ=0 EndX=-112 EndY=78 EndZ=0
    g17: GeomPoint X=9e-16 Y=78 Z=0
    g18: Circle CenterX=-70.4943 CenterY=-78 CenterZ=0 NormalX=0 NormalY=0 NormalZ=1 AngleXU=0 Radius=3
    g19: LineSegment StartX=0 StartY=-73.2812 StartZ=0 EndX=0 EndY=73.2812 EndZ=0
    g20: GeomPoint X=0 Y=0 Z=0
    g21: LineSegment StartX=-70.4943 StartY=-4.3e-15 StartZ=0 EndX=-70.4943 EndY=-78 EndZ=0
  constraints (52):
    c: Radius(g0) = 30
    c: Coincident(g1,g0)
    c: Radius(g1) = 80.5
    c: Horizontal(g2)
    c: Coincident(g2,g1)
    c: Coincident(g2,g1)
    c: DistanceX(g1,g1) = 92
    c: Coincident(g3,g0)
    c: Radius(g3) = 67.5
    c: PointOnObject(g4,g3)
    c: PointOnObject(g5,g3)
    c: PointOnObject(g6,g3)
    c: Equal(g6,g5)
    c: Equal(g5,g4)
    c: Coincident(g7,g6)
    c: Coincident(g7,g5)
    c: Coincident(g8,g5)
    c: Coincident(g8,g4)
    c: Coincident(g9,g4)
    c: Coincident(g9,g6)
    c: Equal(g7,g9)
    c: Equal(g9,g8)
    c: Radius(g5) = 3.1
    c: Coincident(g10,g4)
    c: Coincident(g11,g6)
    c: Coincident(g12,g5)
    c: Equal(g11,g10)
    c: Equal(g10,g12)
    c: Radius(g12) = 8
    c: Coincident(g13,g14)
    c: Coincident(g14,g15)
    c: Coincident(g15,g16)
    c: Coincident(g16,g13)
    c: Horizontal(g13)
    c: Horizontal(g15)
    c: Vertical(g14)
    c: Vertical(g16)
    c: DistanceY(g16,g16) = 156
    c: Symmetric(g13,g13,g17)
    c: Radius(g18) = 3
    c: DistanceX(g13,g13) = 224
    c: PointOnObject(g19,g1)
    c: Vertical(g19)
    c: Symmetric(g1,g1,g19)
    c: Symmetric(g19,g19,g20)
    c: Symmetric(g13,g14,g20)
    c: Coincident(g20,g-1)
    c: PointOnObject(g18,g15)
    c: Coincident(g21,g-3)
    c: Vertical(g21)
    c: Coincident(g21,g18)
    c: DistanceY(g1,g5) = 11.5
FEATURE [PartDesign::Pad] Pad017
  Direction = (1,1,1)
  Length = 156
  Length2 = 100
  Midplane = true
  Placement = pos=(0,0,0) rot=(1,0,0;1.5708rad)
  Profile = -> Sketch084
  Type = 0
FEATURE [PartDesign::Body] Body013  label="fixture_shell_router"
  Group = -> [Sketch078,Sketch084,Pad017]
  Origin = -> Origin020
  Tip = -> Pad017
FEATURE [App::Part] Part001  label="Fixtures"
  Group = -> [Body007,Body011,Body012,Body013]
  Origin = -> Origin012
FEATURE [Sketcher::SketchObject] Sketch085  label="Icons"
  ExternalGeometry = -> [Sketch036]
  FullyConstrained = true
  MapMode = 5
  Support = -> [XY_Plane003]
  expr: Constraints[97] = 1.25 * <<Dimensions>>.predrill_3_rad
  sketch-geometry (44):
    g0: LineSegment StartX=15.3207 StartY=76.4001 StartZ=0 EndX=15.8207 EndY=76.4001 EndZ=0
    g1: LineSegment StartX=15.8207 StartY=76.4001 StartZ=0 EndX=15.8207 EndY=74.9001 EndZ=0
    g2: LineSegment StartX=15.8207 StartY=74.9001 StartZ=0 EndX=15.3207 EndY=74.9001 EndZ=0
    g3: LineSegment StartX=15.3207 StartY=74.9001 StartZ=0 EndX=15.3207 EndY=76.4001 EndZ=0
    g4: LineSegment StartX=15.8207 StartY=76.4001 StartZ=0 EndX=16.4207 EndY=76.8001 EndZ=0
    g5: LineSegment StartX=15.8207 StartY=74.9001 StartZ=0 EndX=16.4207 EndY=74.5001 EndZ=0
    g6: LineSegment StartX=16.4207 StartY=74.5001 StartZ=0 EndX=16.4207 EndY=76.8001 EndZ=0
    g7: LineSegment StartX=15.3207 StartY=75.6501 StartZ=0 EndX=16.4207 EndY=75.6501 EndZ=0
    g8: LineSegment StartX=15.8707 StartY=85.1999 StartZ=0 EndX=16.3707 EndY=85.1999 EndZ=0
    g9: LineSegment StartX=16.3707 StartY=85.1999 StartZ=0 EndX=16.3707 EndY=83.6999 EndZ=0
    g10: LineSegment StartX=16.3707 StartY=83.6999 StartZ=0 EndX=15.8707 EndY=83.6999 EndZ=0
    g11: LineSegment StartX=15.8707 StartY=83.6999 StartZ=0 EndX=15.8707 EndY=85.1999 EndZ=0
    g12: LineSegment StartX=16.3707 StartY=85.1999 StartZ=0 EndX=16.9707 EndY=85.5999 EndZ=0
    g13: LineSegment StartX=16.3707 StartY=83.6999 StartZ=0 EndX=16.9707 EndY=83.2999 EndZ=0
    g14: LineSegment StartX=16.9707 StartY=83.2999 StartZ=0 EndX=16.9707 EndY=85.5999 EndZ=0
    g15: LineSegment StartX=15.8707 StartY=84.4499 StartZ=0 EndX=16.9707 EndY=84.4499 EndZ=0
    g16: LineSegment StartX=10.9208 StartY=68.7792 StartZ=0 EndX=11.4208 EndY=68.7792 EndZ=0
    g17: LineSegment StartX=11.4208 StartY=68.7792 StartZ=0 EndX=11.4208 EndY=67.2792 EndZ=0
    g18: LineSegment StartX=11.4208 StartY=67.2792 StartZ=0 EndX=10.9208 EndY=67.2792 EndZ=0
    g19: LineSegment StartX=10.9208 StartY=67.2792 StartZ=0 EndX=10.9208 EndY=68.7792 EndZ=0
    g20: LineSegment StartX=11.4208 StartY=68.7792 StartZ=0 EndX=12.0208 EndY=69.1792 EndZ=0
    g21: LineSegment StartX=11.4208 StartY=67.2792 StartZ=0 EndX=12.0208 EndY=66.8792 EndZ=0
    g22: LineSegment StartX=12.0208 StartY=66.8792 StartZ=0 EndX=12.0208 EndY=69.1792 EndZ=0
    g23: LineSegment StartX=10.9208 StartY=68.0292 StartZ=0 EndX=12.0208 EndY=68.0292 EndZ=0
    g24: LineSegment StartX=17.5707 StartY=85.5999 StartZ=0 EndX=15.2707 EndY=83.2999 EndZ=0
    g25: LineSegment StartX=15.2707 StartY=85.5999 StartZ=0 EndX=17.5707 EndY=83.2999 EndZ=0
    g26: GeomPoint X=16.4207 Y=84.4499 Z=0
    g27: LineSegment StartX=15.2707 StartY=83.2999 StartZ=0 EndX=17.5707 EndY=83.2999 EndZ=0
    g28: LineSegment StartX=16.9707 StartY=85.5999 StartZ=0 EndX=17.5707 EndY=85.5999 EndZ=0
    g29: ArcOfCircle CenterX=15.3207 CenterY=75.6501 CenterZ=0 NormalX=0 NormalY=0 NormalZ=1 AngleXU=0 Radius=1.5 StartAngle=5.75959 EndAngle=6.80678
    g30: LineSegment StartX=16.6198 StartY=76.4001 StartZ=0 EndX=16.6198 EndY=74.9001 EndZ=0
    g31: ArcOfCircle CenterX=10.9208 CenterY=68.0292 CenterZ=0 NormalX=0 NormalY=0 NormalZ=1 AngleXU=0 Radius=1.5 StartAngle=5.75959 EndAngle=6.80678
    g32: ArcOfCircle CenterX=10.9208 CenterY=68.0292 CenterZ=0 NormalX=0 NormalY=0 NormalZ=1 AngleXU=0 Radius=2 StartAngle=5.75959 EndAngle=6.80678
    g33: ArcOfCircle CenterX=10.9208 CenterY=68.0292 CenterZ=0 NormalX=0 NormalY=0 NormalZ=1 AngleXU=0 Radius=2.5 StartAngle=5.75959 EndAngle=6.80678
    g34: LineSegment StartX=12.2199 StartY=68.7792 StartZ=0 EndX=12.2199 EndY=67.2792 EndZ=0
    g35: LineSegment StartX=10.9208 StartY=68.0292 StartZ=0 EndX=13.0859 EndY=69.2792 EndZ=0
    g36: LineSegment StartX=10.9208 StartY=68.0292 StartZ=0 EndX=13.0859 EndY=66.7792 EndZ=0
    g37: Circle CenterX=12.0208 CenterY=92.0708 CenterZ=0 NormalX=0 NormalY=0 NormalZ=1 AngleXU=0 Radius=1
    g38: LineSegment StartX=12.0208 StartY=93.3208 StartZ=0 EndX=12.0208 EndY=92.0708 EndZ=0
    g39: LineSegment StartX=12.0208 StartY=92.0708 StartZ=0 EndX=0 EndY=80.05 EndZ=0
    g40: LineSegment StartX=0 StartY=80.05 StartZ=0 EndX=16.4207 EndY=84.4499 EndZ=0
    g41: LineSegment StartX=12.0208 StartY=68.0292 StartZ=0 EndX=0 EndY=80.05 EndZ=0
    g42: LineSegment StartX=16.4207 StartY=75.6501 StartZ=0 EndX=0 EndY=80.05 EndZ=0
    g43: Circle CenterX=0 CenterY=80.05 CenterZ=0 NormalX=0 NormalY=0 NormalZ=1 AngleXU=0 Radius=17
  constraints (116):
    c: Coincident(g0,g1)
    c: Coincident(g1,g2)
    c: Coincident(g2,g3)
    c: Coincident(g3,g0)
    c: Horizontal(g0)
    c: Horizontal(g2)
    c: Vertical(g1)
    c: Vertical(g3)
    c: Coincident(g4,g0)
    c: Coincident(g5,g1)
    c: Coincident(g6,g5)
    c: Coincident(g6,g4)
    c: Horizontal(g7)
    c: Symmetric(g4,g5,g7)
    c: Symmetric(g0,g2,g7)
    c: Vertical(g6)
    c: DistanceX(g0,g0) = 0.5
    c: DistanceY(g3,g3) = 1.5
    c: DistanceY(g5,g4) = 2.3
    c: DistanceX(g7,g7) = 1.1
    c: Coincident(g8,g9)
    c: Coincident(g9,g10)
    c: Coincident(g10,g11)
    c: Coincident(g11,g8)
    c: Horizontal(g8)
    c: Horizontal(g10)
    c: Vertical(g9)
    c: Vertical(g11)
    c: Coincident(g12,g8)
    c: Coincident(g13,g9)
    c: Coincident(g14,g13)
    c: Coincident(g14,g12)
    c: Horizontal(g15)
    c: Symmetric(g12,g13,g15)
    c: Symmetric(g8,g10,g15)
    c: Vertical(g14)
    c: Equal(g0,g8) = 0.5
    c: Equal(g3,g11) = 1.5
    c: DistanceY(g13,g12) = 2.3
    c: Equal(g7,g15) = 1.1
    c: Coincident(g16,g17)
    c: Coincident(g17,g18)
    c: Coincident(g18,g19)
    c: Coincident(g19,g16)
    c: Horizontal(g16)
    c: Horizontal(g18)
    c: Vertical(g17)
    c: Vertical(g19)
    c: Coincident(g20,g16)
    c: Coincident(g21,g17)
    c: Coincident(g22,g21)
    c: Coincident(g22,g20)
    c: Horizontal(g23)
    c: Symmetric(g20,g21,g23)
    c: Symmetric(g16,g18,g23)
    c: Vertical(g22)
    c: DistanceY(g21,g20) = 2.3
    c: Perpendicular(g24,g25)
    c: Equal(g25,g24)
    c: Symmetric(g25,g25,g26)
    c: Symmetric(g24,g24,g26)
    c: Coincident(g27,g24)
    c: Coincident(g27,g25)
    c: Horizontal(g27)
    c: Symmetric(g15,g15,g26)
    c: Coincident(g28,g12)
    c: Coincident(g28,g24)
    c: Horizontal(g28)
    c: Coincident(g29,g7)
    c: Coincident(g30,g29)
    c: Coincident(g30,g29)
    c: Vertical(g30)
    c: Equal(g30,g1)
    c: Radius(g29) = 1.5
    c: Coincident(g31,g23)
    c: Coincident(g32,g31)
    c: Coincident(g33,g31)
    c: Coincident(g34,g31)
    c: Coincident(g34,g31)
    c: Vertical(g34)
    c: Coincident(g35,g31)
    c: Coincident(g35,g33)
    c: PointOnObject(g31,g35)
    c: Symmetric(g31,g33,g32)
    c: Coincident(g36,g31)
    c: Coincident(g36,g33)
    c: PointOnObject(g31,g36)
    c: PointOnObject(g32,g36)
    c: Equal(g16,g0)
    c: Equal(g20,g4)
    c: Radius(g31) = 1.5
    c: Equal(g19,g1)
    c: Distance(g33,g31) = 1
    c: Vertical(g38)
    c: Radius(g37) = 1
    c: Equal(g19,g34)
    c: Coincident(g38,g37)
    c: DistanceY(g37,g38) = 1.25
    c: Coincident(g39,g37)
    c: Coincident(g40,g39)
    c: Coincident(g40,g26)
    c: Coincident(g41,g23)
    c: Coincident(g41,g39)
    c: Coincident(g39,g-3)
    c: Coincident(g42,g39)
    c: Coincident(g42,g7)
    c: Coincident(g43,g39)
    c: PointOnObject(g37,g43)
    c: PointOnObject(g23,g43)
    c: PointOnObject(g7,g43)
    c: PointOnObject(g26,g43)
    c: Perpendicular(g41,g39)
    c: Angle(g41,g42) = 0.523599
    c: Angle(g42,g40) = 0.523599
    c: Angle(g-2,g41) = 0.785398
    c: Radius(g43) = 17
FEATURE [PartDesign::Body] Body002  label="ampcarrier"
  Group = -> [Sketch036,Sketch037,Sketch038,Sketch041,Pad004,Sketch080,Pad016,Sketch081,Pocket007,Sketch082,Pocket008,Sketch085]
  Origin = -> Origin003
  Placement = pos=(0,-800,0) rot=(0,0,1;0rad)
  Tip = -> Pocket008
FEATURE [Part::Part2DObjectPython] Clone2D019  label="Icons (2D)"  # Draft 2D object (typed FeaturePython)
  Fuse = false
  Objects = -> [Sketch085]
  Placement = pos=(228,-1550,0) rot=(0,0,1;0rad)
  Scale = (1,1,1)
FEATURE [PartDesign::Body] Body008  label="nutzen_bottom"
  Group = -> [Sketch069,Clone2D001,Clone2D002,Clone2D003,Clone2D004,Clone2D005,Clone2D006,Clone2D007,Clone2D008,Clone2D009,Clone2D019,Clone2D011,Clone2D013,Clone2D015,Clone2D016,Clone2D010]
  Origin = -> Origin009
FEATURE [App::Part] Part003  label="Job02"
  Group = -> [Body008,mirror001,Clone2D,mirror,Clone2D012,Clone2D017]
  Origin = -> Origin014
FEATURE [Sketcher::SketchObject] Sketch086  label="clampingOptions"
  FullyConstrained = false
  MapMode = 5
  Support = -> [XY_Plane025]
  sketch-geometry (31):
    g0: ArcOfCircle CenterX=0 CenterY=0 CenterZ=0 NormalX=0 NormalY=0 NormalZ=1 AngleXU=0 Radius=15 StartAngle=4.71239 EndAngle=6.28319
    g1: GeomPoint X=7.5 Y=-7.5 Z=0
    g2: LineSegment StartX=0 StartY=0 StartZ=0 EndX=10.6066 EndY=-10.6066 EndZ=0
    g3: Circle CenterX=10.6066 CenterY=-10.6066 CenterZ=0 NormalX=0 NormalY=0 NormalZ=1 AngleXU=0 Radius=3
    g4: ArcOfCircle CenterX=0 CenterY=0 CenterZ=0 NormalX=0 NormalY=0 NormalZ=1 AngleXU=0 Radius=100 StartAngle=4.71239 EndAngle=6.28319
    g5: LineSegment StartX=10.6066 StartY=-10.6066 StartZ=0 EndX=99.4359 EndY=-10.6066 EndZ=0
    g6: LineSegment StartX=10.6066 StartY=-10.6066 StartZ=0 EndX=10.6066 EndY=-99.4359 EndZ=0
    g7: LineSegment StartX=0 StartY=0 StartZ=0 EndX=90.1455 EndY=-43.2873 EndZ=0
    g8: LineSegment StartX=10.6066 StartY=-10.6066 StartZ=0 EndX=71.917 EndY=-69.4834 EndZ=0
    g9: LineSegment StartX=0 StartY=0 StartZ=0 EndX=44.8383 EndY=-89.3841 EndZ=0
    g10: LineSegment StartX=99.4359 StartY=-10.6066 StartZ=0 EndX=629.936 EndY=-10.6066 EndZ=0
    g11: LineSegment StartX=10.6066 StartY=-99.4359 StartZ=0 EndX=10.6066 EndY=-602.436 EndZ=0
    g12: LineSegment StartX=44.8383 StartY=-89.3841 StartZ=0 EndX=305.125 EndY=-608.259 EndZ=0
    g13: LineSegment StartX=71.917 StartY=-69.4834 StartZ=0 EndX=622.035 EndY=-597.765 EndZ=0
    g14: LineSegment StartX=90.1455 StartY=-43.2873 StartZ=0 EndX=634.895 EndY=-304.872 EndZ=0
    g15: Circle CenterX=197.297 CenterY=-10.6066 CenterZ=0 NormalX=0 NormalY=0 NormalZ=1 AngleXU=0 Radius=3
    g16: Circle CenterX=426.131 CenterY=-10.6066 CenterZ=0 NormalX=0 NormalY=0 NormalZ=1 AngleXU=0 Radius=3
    g17: Circle CenterX=159.976 CenterY=-154.047 CenterZ=0 NormalX=0 NormalY=0 NormalZ=1 AngleXU=0 Radius=3
    g18: Circle CenterX=158.635 CenterY=-316.235 CenterZ=0 NormalX=0 NormalY=0 NormalZ=1 AngleXU=0 Radius=3
    g19: Circle CenterX=340.522 CenterY=-327.427 CenterZ=0 NormalX=0 NormalY=0 NormalZ=1 AngleXU=0 Radius=3
    g20: Circle CenterX=489.034 CenterY=-234.831 CenterZ=0 NormalX=0 NormalY=0 NormalZ=1 AngleXU=0 Radius=3
    g21: Circle CenterX=583.933 CenterY=-561.175 CenterZ=0 NormalX=0 NormalY=0 NormalZ=1 AngleXU=0 Radius=3
    g22: Circle CenterX=10.6066 CenterY=-447.489 CenterZ=0 NormalX=0 NormalY=0 NormalZ=1 AngleXU=0 Radius=3
    g23: Circle CenterX=197.297 CenterY=-10.6066 CenterZ=0 NormalX=0 NormalY=0 NormalZ=1 AngleXU=0 Radius=8
    g24: Circle CenterX=426.131 CenterY=-10.6066 CenterZ=0 NormalX=0 NormalY=0 NormalZ=1 AngleXU=0 Radius=8
    g25: Circle CenterX=489.034 CenterY=-234.831 CenterZ=0 NormalX=0 NormalY=0 NormalZ=1 AngleXU=0 Radius=8
    g26: Circle CenterX=159.976 CenterY=-154.047 CenterZ=0 NormalX=0 NormalY=0 NormalZ=1 AngleXU=0 Radius=8
    g27: Circle CenterX=10.6066 CenterY=-447.489 CenterZ=0 NormalX=0 NormalY=0 NormalZ=1 AngleXU=0 Radius=8
    g28: Circle CenterX=583.933 CenterY=-561.175 CenterZ=0 NormalX=0 NormalY=0 NormalZ=1 AngleXU=0 Radius=8
    g29: Circle CenterX=340.522 CenterY=-327.427 CenterZ=0 NormalX=0 NormalY=0 NormalZ=1 AngleXU=0 Radius=8
    g30: Circle CenterX=158.635 CenterY=-316.235 CenterZ=0 NormalX=0 NormalY=0 NormalZ=1 AngleXU=0 Radius=8
  constraints (75):
    c: Coincident(g0,g-1)
    c: PointOnObject(g0,g-1)
    c: PointOnObject(g0,g-2)
    c: Symmetric(g0,g0,g1)
    c: Radius(g0) = 15
    c: Coincident(g2,g0)
    c: PointOnObject(g1,g2)
    c: Radius(g3) = 3
    c: Coincident(g4,g-1)
    c: PointOnObject(g4,g-1)
    c: PointOnObject(g4,g-2)
    c: Radius(g4) = 100
    c: Horizontal(g5)
    c: Vertical(g6)
    c: Coincident(g10,g5)
    c: Horizontal(g10)
    c: Coincident(g11,g6)
    c: Vertical(g11)
    c: PointOnObject(g9,g4)
    c: PointOnObject(g8,g4)
    c: PointOnObject(g7,g4)
    c: Angle(g7,g5) = 0.447677
    c: Angle(g8,g5) = 0.765152
    c: Angle(g9,g5) = 1.10584
    c: PointOnObject(g11,g4)
    c: PointOnObject(g10,g4)
    c: Coincident(g12,g9)
    c: Coincident(g13,g8)
    c: Coincident(g14,g7)
    c: Parallel(g8,g13)
    c: Parallel(g14,g7)
    c: Parallel(g12,g9)
    c: DistanceX(g10,g10) = 530.5
    c: Distance(g14,g14) = 604.3
    c: Distance(g13,g13) = 762.7
    c: Distance(g12,g12) = 580.5
    c: DistanceY(g11,g11) = 503
    c: PointOnObject(g15,g10)
    c: PointOnObject(g16,g10)
    c: PointOnObject(g17,g13)
    c: PointOnObject(g18,g12)
    c: PointOnObject(g19,g13)
    c: PointOnObject(g20,g14)
    c: PointOnObject(g21,g13)
    c: PointOnObject(g22,g11)
    c: Radius(g22) = 3
    c: Equal(g18,g19)
    c: Equal(g19,g21)
    c: Equal(g21,g15)
    c: Equal(g15,g16)
    c: Equal(g16,g20)
    c: Coincident(g23,g15)
    c: Coincident(g24,g16)
    c: Coincident(g25,g20)
    c: Coincident(g26,g17)
    c: Coincident(g27,g22)
    c: Coincident(g28,g21)
    c: Coincident(g29,g19)
    c: Radius(g27) = 8
    c: Equal(g29,g26)
    c: Equal(g26,g23)
    c: Equal(g23,g24)
    c: Equal(g24,g25)
    c: Equal(g25,g28)
    c: Equal(g17,g22)
    c: Coincident(g30,g18)
    c: Equal(g30,g27)
    c: PointOnObject(g3,g0)
    c: Coincident(g2,g3)
    c: Coincident(g-1,g7)
    c: Coincident(g9,g-1)
    c: Coincident(g6,g5)
    c: Coincident(g6,g8)
    c: Coincident(g6,g3)
    c: Equal(g26,g27)
FEATURE [Part::Part2DObjectPython] Clone2D020  label="master_nutzen (2D)"  # Draft 2D object (typed FeaturePython)
  Fuse = false
  Objects = -> [Sketch069]
  Placement = pos=(311,1075.81,0) rot=(0,0,1;0rad)
  Scale = (1,1,1)
FEATURE [PartDesign::Body] Body015
  Group = -> [Sketch086,Clone2D020]
  Origin = -> Origin025
FEATURE [App::Part] Part007  label="Job00"
  Group = -> [Body015]
  Origin = -> Origin024
  Placement = pos=(0,-1075.81,0) rot=(0,0,1;0rad)
FEATURE [PartDesign::Body] BaseFeatureBody
  Origin = -> Origin027
FEATURE [PartDesign::Body] Body016
  Origin = -> Origin028
FEATURE [App::Part] Part008
  Group = -> [BaseFeatureBody,Body016]
  Origin = -> Origin026
FEATURE [Sketcher::SketchObject] Sketch087
  FullyConstrained = false
  MapMode = 5
  Support = -> [XY_Plane029]
  expr: Constraints[22] = <<Dimensions>>.usb_board_len
  expr: Constraints[21] = <<Dimensions>>.usb_board_wid
  expr: Constraints[11] = <<Dimensions>>.usb_rec_wid
  expr: Constraints[10] = <<Dimensions>>.usb_rec_len
  expr: Constraints[6] = <<Dimensions>>.usb_part_rad
  sketch-geometry (11):
    g0: Circle CenterX=446.372 CenterY=122.302 CenterZ=0 NormalX=0 NormalY=0 NormalZ=1 AngleXU=0 Radius=10
    g1: ArcOfCircle CenterX=443.472 CenterY=122.302 CenterZ=0 NormalX=0 NormalY=0 NormalZ=1 AngleXU=0 Radius=1.6 StartAngle=1.5708 EndAngle=4.71239
    g2: ArcOfCircle CenterX=449.272 CenterY=122.302 CenterZ=0 NormalX=0 NormalY=0 NormalZ=1 AngleXU=0 Radius=1.6 StartAngle=4.71239 EndAngle=7.85398
    g3: LineSegment StartX=443.472 StartY=120.702 StartZ=0 EndX=449.272 EndY=120.702 EndZ=0
    g4: LineSegment StartX=443.472 StartY=123.902 StartZ=0 EndX=449.272 EndY=123.902 EndZ=0
    g5: LineSegment StartX=441.872 StartY=122.302 StartZ=0 EndX=450.872 EndY=122.302 EndZ=0
    g6: LineSegment StartX=453.872 StartY=120.702 StartZ=0 EndX=438.872 EndY=120.702 EndZ=0
    g7: LineSegment StartX=438.872 StartY=120.702 StartZ=0 EndX=438.872 EndY=119.702 EndZ=0
    g8: LineSegment StartX=438.872 StartY=119.702 StartZ=0 EndX=453.872 EndY=119.702 EndZ=0
    g9: LineSegment StartX=453.872 StartY=119.702 StartZ=0 EndX=453.872 EndY=120.702 EndZ=0
    g10: GeomPoint X=446.372 Y=120.702 Z=0
  constraints (26):
    c: Tangent(g1,g4) = 1.5708
    c: Tangent(g1,g3) = -1.5708
    c: Tangent(g3,g2) = -1.5708
    c: Tangent(g4,g2) = 1.5708
    c: Horizontal(g3)
    c: Equal(g1,g2)
    c: Radius(g0) = 10
    c: PointOnObject(g5,g1)
    c: Horizontal(g5)
    c: PointOnObject(g1,g5)
    c: DistanceX(g5,g5) = 9
    c: DistanceY(g1,g1) = 3.2
    c: PointOnObject(g5,g2)
    c: Coincident(g6,g7)
    c: Coincident(g7,g8)
    c: Coincident(g8,g9)
    c: Coincident(g9,g6)
    c: Horizontal(g6)
    c: Horizontal(g8)
    c: Vertical(g7)
    c: Vertical(g9)
    c: DistanceX(g7,g8) = 15
    c: DistanceY(g7,g6) = 1
    c: Symmetric(g6,g6,g10)
    c: Symmetric(g2,g1,g10)
    c: Symmetric(g1,g2,g0)
FEATURE [PartDesign::Body] Body017  label="usb-pd"
  Group = -> [Sketch087]
  Origin = -> Origin029
FEATURE [App::Part] Part  label="2D"
  Group = -> [Body,Body001,Body002,Body003,Body004,Body005,Body010,Body017]
  Origin = -> Origin
